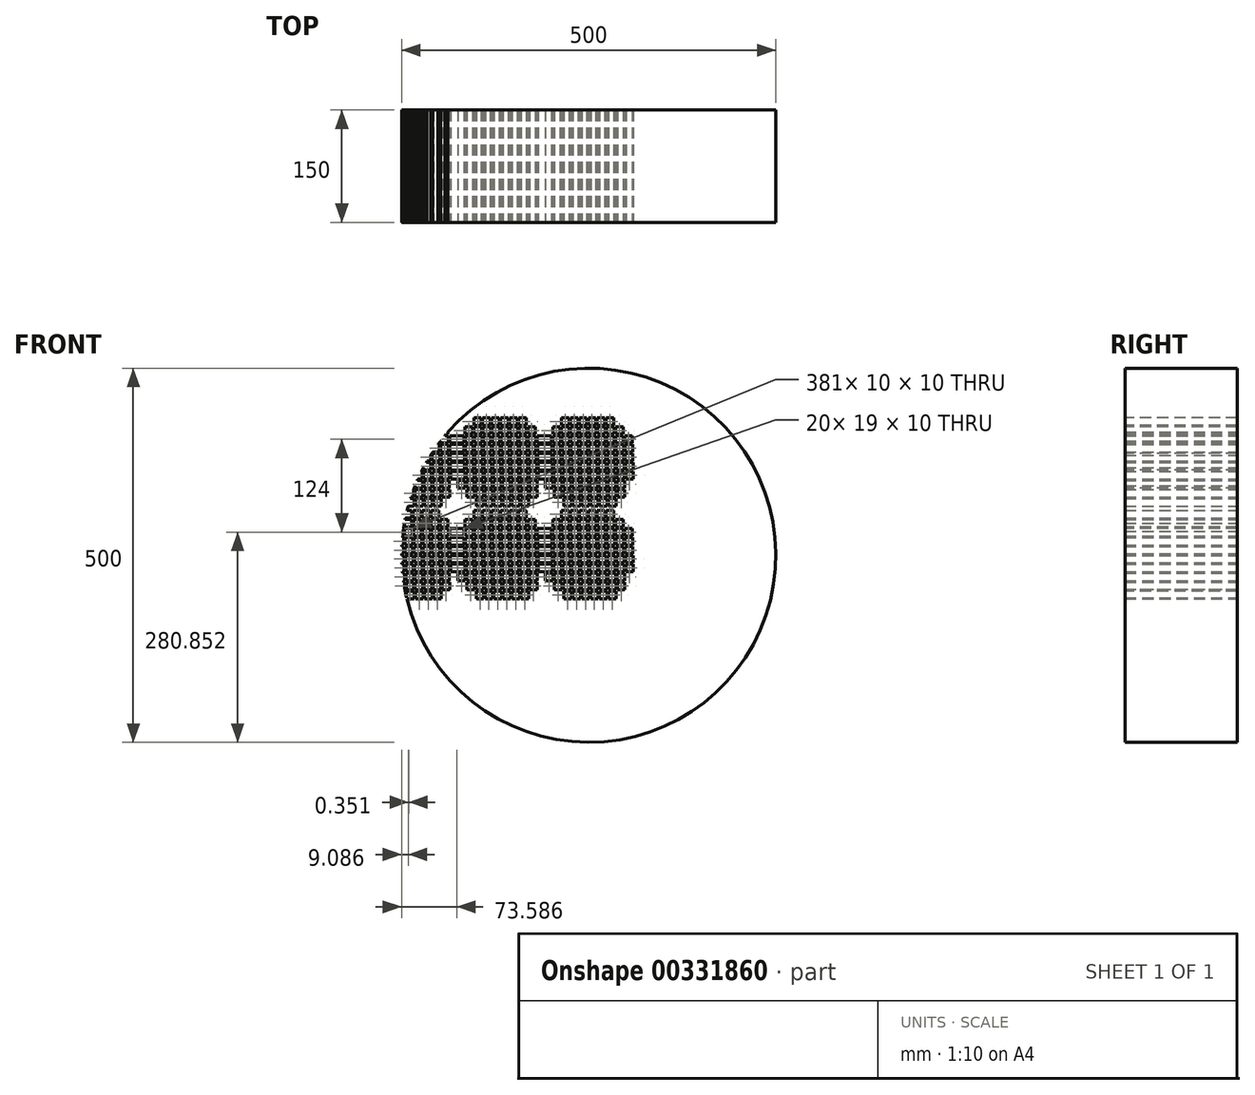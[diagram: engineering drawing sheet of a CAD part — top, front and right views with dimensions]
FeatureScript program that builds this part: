
annotation { "Feature Type Name" : "Feature", "Feature Type Description" : "" }
export const myFeature = defineFeature(function(context is Context, id is Id, definition is map)
    precondition{}
    {
        {
            var Q0;
            Q0=qCreatedBy(makeId("Front.planeOp"),FACE);
            var sketch = newSketch(context, id + "F0", { "sketchPlane" : qUnion([Q0])});
            skCircle(sketch, "E0", {"center": v(-42.34, 53.61) * mm, "radius": 250 * mm});
            skSolve(sketch);
        }
        {
            var Q0;
            Q0=makeQuery(id+"F0.imprint","IMPRINT",FACE,{"disambiguationData":[TD([[makeQuery(id+"F0.imprint","IMPRINT",EDGE,{"derivedFrom":sQuery(id+"F0.wireOp",EDGE,"E0")}),1.0]])]});
            extrude(context, id + "F1", {"entities" : qUnion([Q0]), "depth" : 150 * mm});
        }
        {
            var Q0;
            Q0=makeQuery(id+"F1.opExtrude","CAP_FACE",FACE,{"disambiguationData":[OSD([sQuery(id+"F0.wireOp",EDGE,"E0")])],"isStart":false});
            var sketch = newSketch(context, id + "F2", { "sketchPlane" : qUnion([Q0])});
            skLineSegment(sketch, "E1.0.2.0", {"start": v(-100.5, 19.49) * mm, "end": v(-90.5, 19.49) * mm});
            skLineSegment(sketch, "E1.0.2.1", {"start": v(-90.5, 19.49) * mm, "end": v(-90.5, 29.49) * mm});
            skLineSegment(sketch, "E1.0.2.2", {"start": v(-100.5, 29.49) * mm, "end": v(-90.5, 29.49) * mm});
            skLineSegment(sketch, "E1.0.2.3", {"start": v(-100.5, 19.49) * mm, "end": v(-100.5, 29.49) * mm});
            skLineSegment(sketch, "E1.0.3.0", {"start": v(-100.85, 31.48) * mm, "end": v(-90.85, 31.48) * mm});
            skLineSegment(sketch, "E1.0.3.1", {"start": v(-90.85, 31.48) * mm, "end": v(-90.85, 41.48) * mm});
            skLineSegment(sketch, "E1.0.3.2", {"start": v(-100.85, 41.48) * mm, "end": v(-90.85, 41.48) * mm});
            skLineSegment(sketch, "E1.0.3.3", {"start": v(-100.85, 31.48) * mm, "end": v(-100.85, 41.48) * mm});
            skLineSegment(sketch, "E1.0.4.0", {"start": v(-101.2, 43.48) * mm, "end": v(-91.2, 43.48) * mm});
            skLineSegment(sketch, "E1.0.4.1", {"start": v(-91.2, 43.48) * mm, "end": v(-91.2, 53.48) * mm});
            skLineSegment(sketch, "E1.0.4.2", {"start": v(-101.2, 53.48) * mm, "end": v(-91.2, 53.48) * mm});
            skLineSegment(sketch, "E1.0.4.3", {"start": v(-101.2, 43.48) * mm, "end": v(-101.2, 53.48) * mm});
            skLineSegment(sketch, "E1.0.5.0", {"start": v(-101.55, 55.47) * mm, "end": v(-91.55, 55.47) * mm});
            skLineSegment(sketch, "E1.0.5.1", {"start": v(-91.55, 55.47) * mm, "end": v(-91.55, 65.47) * mm});
            skLineSegment(sketch, "E1.0.5.2", {"start": v(-101.55, 65.47) * mm, "end": v(-91.55, 65.47) * mm});
            skLineSegment(sketch, "E1.0.5.3", {"start": v(-101.55, 55.47) * mm, "end": v(-101.55, 65.47) * mm});
            skLineSegment(sketch, "E1.0.6.0", {"start": v(-101.9, 67.47) * mm, "end": v(-91.9, 67.47) * mm});
            skLineSegment(sketch, "E1.0.6.1", {"start": v(-91.9, 67.47) * mm, "end": v(-91.9, 77.47) * mm});
            skLineSegment(sketch, "E1.0.6.2", {"start": v(-101.9, 77.47) * mm, "end": v(-91.9, 77.47) * mm});
            skLineSegment(sketch, "E1.0.6.3", {"start": v(-101.9, 67.47) * mm, "end": v(-101.9, 77.47) * mm});
            skLineSegment(sketch, "E1.0.7.0", {"start": v(-102.25, 79.46) * mm, "end": v(-92.25, 79.46) * mm});
            skLineSegment(sketch, "E1.0.7.1", {"start": v(-92.25, 79.46) * mm, "end": v(-92.25, 89.46) * mm});
            skLineSegment(sketch, "E1.0.7.2", {"start": v(-102.25, 89.46) * mm, "end": v(-92.25, 89.46) * mm});
            skLineSegment(sketch, "E1.0.7.3", {"start": v(-102.25, 79.46) * mm, "end": v(-102.25, 89.46) * mm});
            skLineSegment(sketch, "E1.1.1.0", {"start": v(-88.15, 7.5) * mm, "end": v(-78.15, 7.5) * mm});
            skLineSegment(sketch, "E1.1.1.1", {"start": v(-78.15, 7.5) * mm, "end": v(-78.15, 17.5) * mm});
            skLineSegment(sketch, "E1.1.1.2", {"start": v(-88.15, 17.5) * mm, "end": v(-78.15, 17.5) * mm});
            skLineSegment(sketch, "E1.1.1.3", {"start": v(-88.15, 7.5) * mm, "end": v(-88.15, 17.5) * mm});
            skLineSegment(sketch, "E1.1.2.0", {"start": v(-88.5, 19.49) * mm, "end": v(-78.5, 19.49) * mm});
            skLineSegment(sketch, "E1.1.2.1", {"start": v(-78.5, 19.49) * mm, "end": v(-78.5, 29.49) * mm});
            skLineSegment(sketch, "E1.1.2.2", {"start": v(-88.5, 29.49) * mm, "end": v(-78.5, 29.49) * mm});
            skLineSegment(sketch, "E1.1.2.3", {"start": v(-88.5, 19.49) * mm, "end": v(-88.5, 29.49) * mm});
            skLineSegment(sketch, "E1.1.3.0", {"start": v(-88.85, 31.48) * mm, "end": v(-78.85, 31.48) * mm});
            skLineSegment(sketch, "E1.1.3.1", {"start": v(-78.85, 31.48) * mm, "end": v(-78.85, 41.48) * mm});
            skLineSegment(sketch, "E1.1.3.2", {"start": v(-88.85, 41.48) * mm, "end": v(-78.85, 41.48) * mm});
            skLineSegment(sketch, "E1.1.3.3", {"start": v(-88.85, 31.48) * mm, "end": v(-88.85, 41.48) * mm});
            skLineSegment(sketch, "E1.1.4.0", {"start": v(-89.2, 43.48) * mm, "end": v(-79.2, 43.48) * mm});
            skLineSegment(sketch, "E1.1.4.1", {"start": v(-79.2, 43.48) * mm, "end": v(-79.2, 53.48) * mm});
            skLineSegment(sketch, "E1.1.4.2", {"start": v(-89.2, 53.48) * mm, "end": v(-79.2, 53.48) * mm});
            skLineSegment(sketch, "E1.1.4.3", {"start": v(-89.2, 43.48) * mm, "end": v(-89.2, 53.48) * mm});
            skLineSegment(sketch, "E1.1.5.0", {"start": v(-89.55, 55.47) * mm, "end": v(-79.55, 55.47) * mm});
            skLineSegment(sketch, "E1.1.5.1", {"start": v(-79.55, 55.47) * mm, "end": v(-79.55, 65.47) * mm});
            skLineSegment(sketch, "E1.1.5.2", {"start": v(-89.55, 65.47) * mm, "end": v(-79.55, 65.47) * mm});
            skLineSegment(sketch, "E1.1.5.3", {"start": v(-89.55, 55.47) * mm, "end": v(-89.55, 65.47) * mm});
            skLineSegment(sketch, "E1.1.6.0", {"start": v(-89.9, 67.47) * mm, "end": v(-79.9, 67.47) * mm});
            skLineSegment(sketch, "E1.1.6.1", {"start": v(-79.9, 67.47) * mm, "end": v(-79.9, 77.47) * mm});
            skLineSegment(sketch, "E1.1.6.2", {"start": v(-89.9, 77.47) * mm, "end": v(-79.9, 77.47) * mm});
            skLineSegment(sketch, "E1.1.6.3", {"start": v(-89.9, 67.47) * mm, "end": v(-89.9, 77.47) * mm});
            skLineSegment(sketch, "E1.1.7.0", {"start": v(-90.25, 79.46) * mm, "end": v(-80.25, 79.46) * mm});
            skLineSegment(sketch, "E1.1.7.1", {"start": v(-80.25, 79.46) * mm, "end": v(-80.25, 89.46) * mm});
            skLineSegment(sketch, "E1.1.7.2", {"start": v(-90.25, 89.46) * mm, "end": v(-80.25, 89.46) * mm});
            skLineSegment(sketch, "E1.1.7.3", {"start": v(-90.25, 79.46) * mm, "end": v(-90.25, 89.46) * mm});
            skLineSegment(sketch, "E1.1.8.0", {"start": v(-90.6, 91.46) * mm, "end": v(-80.6, 91.46) * mm});
            skLineSegment(sketch, "E1.1.8.1", {"start": v(-80.6, 91.46) * mm, "end": v(-80.6, 101.46) * mm});
            skLineSegment(sketch, "E1.1.8.2", {"start": v(-90.6, 101.46) * mm, "end": v(-80.6, 101.46) * mm});
            skLineSegment(sketch, "E1.1.8.3", {"start": v(-90.6, 91.46) * mm, "end": v(-90.6, 101.46) * mm});
            skLineSegment(sketch, "E1.2.0.0", {"start": v(-75.8, -4.5) * mm, "end": v(-65.8, -4.5) * mm});
            skLineSegment(sketch, "E1.2.0.1", {"start": v(-65.8, -4.5) * mm, "end": v(-65.8, 5.5) * mm});
            skLineSegment(sketch, "E1.2.0.2", {"start": v(-75.8, 5.5) * mm, "end": v(-65.8, 5.5) * mm});
            skLineSegment(sketch, "E1.2.0.3", {"start": v(-75.8, -4.5) * mm, "end": v(-75.8, 5.5) * mm});
            skLineSegment(sketch, "E1.2.1.0", {"start": v(-76.15, 7.5) * mm, "end": v(-66.15, 7.5) * mm});
            skLineSegment(sketch, "E1.2.1.1", {"start": v(-66.15, 7.5) * mm, "end": v(-66.15, 17.5) * mm});
            skLineSegment(sketch, "E1.2.1.2", {"start": v(-76.15, 17.5) * mm, "end": v(-66.15, 17.5) * mm});
            skLineSegment(sketch, "E1.2.1.3", {"start": v(-76.15, 7.5) * mm, "end": v(-76.15, 17.5) * mm});
            skLineSegment(sketch, "E1.2.2.0", {"start": v(-76.5, 19.49) * mm, "end": v(-66.5, 19.49) * mm});
            skLineSegment(sketch, "E1.2.2.1", {"start": v(-66.5, 19.49) * mm, "end": v(-66.5, 29.49) * mm});
            skLineSegment(sketch, "E1.2.2.2", {"start": v(-76.5, 29.49) * mm, "end": v(-66.5, 29.49) * mm});
            skLineSegment(sketch, "E1.2.2.3", {"start": v(-76.5, 19.49) * mm, "end": v(-76.5, 29.49) * mm});
            skLineSegment(sketch, "E1.2.3.0", {"start": v(-76.85, 31.48) * mm, "end": v(-66.85, 31.48) * mm});
            skLineSegment(sketch, "E1.2.3.1", {"start": v(-66.85, 31.48) * mm, "end": v(-66.85, 41.48) * mm});
            skLineSegment(sketch, "E1.2.3.2", {"start": v(-76.85, 41.48) * mm, "end": v(-66.85, 41.48) * mm});
            skLineSegment(sketch, "E1.2.3.3", {"start": v(-76.85, 31.48) * mm, "end": v(-76.85, 41.48) * mm});
            skLineSegment(sketch, "E1.2.4.0", {"start": v(-77.2, 43.48) * mm, "end": v(-67.2, 43.48) * mm});
            skLineSegment(sketch, "E1.2.4.1", {"start": v(-67.2, 43.48) * mm, "end": v(-67.2, 53.48) * mm});
            skLineSegment(sketch, "E1.2.4.2", {"start": v(-77.2, 53.48) * mm, "end": v(-67.2, 53.48) * mm});
            skLineSegment(sketch, "E1.2.4.3", {"start": v(-77.2, 43.48) * mm, "end": v(-77.2, 53.48) * mm});
            skLineSegment(sketch, "E1.2.5.0", {"start": v(-77.55, 55.47) * mm, "end": v(-67.55, 55.47) * mm});
            skLineSegment(sketch, "E1.2.5.1", {"start": v(-67.55, 55.47) * mm, "end": v(-67.55, 65.47) * mm});
            skLineSegment(sketch, "E1.2.5.2", {"start": v(-77.55, 65.47) * mm, "end": v(-67.55, 65.47) * mm});
            skLineSegment(sketch, "E1.2.5.3", {"start": v(-77.55, 55.47) * mm, "end": v(-77.55, 65.47) * mm});
            skLineSegment(sketch, "E1.2.6.0", {"start": v(-77.9, 67.47) * mm, "end": v(-67.9, 67.47) * mm});
            skLineSegment(sketch, "E1.2.6.1", {"start": v(-67.9, 67.47) * mm, "end": v(-67.9, 77.47) * mm});
            skLineSegment(sketch, "E1.2.6.2", {"start": v(-77.9, 77.47) * mm, "end": v(-67.9, 77.47) * mm});
            skLineSegment(sketch, "E1.2.6.3", {"start": v(-77.9, 67.47) * mm, "end": v(-77.9, 77.47) * mm});
            skLineSegment(sketch, "E1.2.7.0", {"start": v(-78.25, 79.46) * mm, "end": v(-68.25, 79.46) * mm});
            skLineSegment(sketch, "E1.2.7.1", {"start": v(-68.25, 79.46) * mm, "end": v(-68.25, 89.46) * mm});
            skLineSegment(sketch, "E1.2.7.2", {"start": v(-78.25, 89.46) * mm, "end": v(-68.25, 89.46) * mm});
            skLineSegment(sketch, "E1.2.7.3", {"start": v(-78.25, 79.46) * mm, "end": v(-78.25, 89.46) * mm});
            skLineSegment(sketch, "E1.2.8.0", {"start": v(-78.6, 91.46) * mm, "end": v(-68.6, 91.46) * mm});
            skLineSegment(sketch, "E1.2.8.1", {"start": v(-68.6, 91.46) * mm, "end": v(-68.6, 101.46) * mm});
            skLineSegment(sketch, "E1.2.8.2", {"start": v(-78.6, 101.46) * mm, "end": v(-68.6, 101.46) * mm});
            skLineSegment(sketch, "E1.2.8.3", {"start": v(-78.6, 91.46) * mm, "end": v(-78.6, 101.46) * mm});
            skLineSegment(sketch, "E1.2.9.0", {"start": v(-78.96, 103.45) * mm, "end": v(-68.96, 103.45) * mm});
            skLineSegment(sketch, "E1.2.9.1", {"start": v(-68.96, 103.45) * mm, "end": v(-68.96, 113.45) * mm});
            skLineSegment(sketch, "E1.2.9.2", {"start": v(-78.96, 113.45) * mm, "end": v(-68.96, 113.45) * mm});
            skLineSegment(sketch, "E1.2.9.3", {"start": v(-78.96, 103.45) * mm, "end": v(-78.96, 113.45) * mm});
            skLineSegment(sketch, "E1.3.0.0", {"start": v(-63.8, -4.5) * mm, "end": v(-53.8, -4.5) * mm});
            skLineSegment(sketch, "E1.3.0.1", {"start": v(-53.8, -4.5) * mm, "end": v(-53.8, 5.5) * mm});
            skLineSegment(sketch, "E1.3.0.2", {"start": v(-63.8, 5.5) * mm, "end": v(-53.8, 5.5) * mm});
            skLineSegment(sketch, "E1.3.0.3", {"start": v(-63.8, -4.5) * mm, "end": v(-63.8, 5.5) * mm});
            skLineSegment(sketch, "E1.3.1.0", {"start": v(-64.15, 7.5) * mm, "end": v(-54.15, 7.5) * mm});
            skLineSegment(sketch, "E1.3.1.1", {"start": v(-54.15, 7.5) * mm, "end": v(-54.15, 17.5) * mm});
            skLineSegment(sketch, "E1.3.1.2", {"start": v(-64.15, 17.5) * mm, "end": v(-54.15, 17.5) * mm});
            skLineSegment(sketch, "E1.3.1.3", {"start": v(-64.15, 7.5) * mm, "end": v(-64.15, 17.5) * mm});
            skLineSegment(sketch, "E1.3.2.0", {"start": v(-64.5, 19.49) * mm, "end": v(-54.5, 19.49) * mm});
            skLineSegment(sketch, "E1.3.2.1", {"start": v(-54.5, 19.49) * mm, "end": v(-54.5, 29.49) * mm});
            skLineSegment(sketch, "E1.3.2.2", {"start": v(-64.5, 29.49) * mm, "end": v(-54.5, 29.49) * mm});
            skLineSegment(sketch, "E1.3.2.3", {"start": v(-64.5, 19.49) * mm, "end": v(-64.5, 29.49) * mm});
            skLineSegment(sketch, "E1.3.3.0", {"start": v(-64.85, 31.48) * mm, "end": v(-54.85, 31.48) * mm});
            skLineSegment(sketch, "E1.3.3.1", {"start": v(-54.85, 31.48) * mm, "end": v(-54.85, 41.48) * mm});
            skLineSegment(sketch, "E1.3.3.2", {"start": v(-64.85, 41.48) * mm, "end": v(-54.85, 41.48) * mm});
            skLineSegment(sketch, "E1.3.3.3", {"start": v(-64.85, 31.48) * mm, "end": v(-64.85, 41.48) * mm});
            skLineSegment(sketch, "E1.3.4.0", {"start": v(-65.2, 43.48) * mm, "end": v(-55.2, 43.48) * mm});
            skLineSegment(sketch, "E1.3.4.1", {"start": v(-55.2, 43.48) * mm, "end": v(-55.2, 53.48) * mm});
            skLineSegment(sketch, "E1.3.4.2", {"start": v(-65.2, 53.48) * mm, "end": v(-55.2, 53.48) * mm});
            skLineSegment(sketch, "E1.3.4.3", {"start": v(-65.2, 43.48) * mm, "end": v(-65.2, 53.48) * mm});
            skLineSegment(sketch, "E1.3.5.0", {"start": v(-65.55, 55.47) * mm, "end": v(-55.55, 55.47) * mm});
            skLineSegment(sketch, "E1.3.5.1", {"start": v(-55.55, 55.47) * mm, "end": v(-55.55, 65.47) * mm});
            skLineSegment(sketch, "E1.3.5.2", {"start": v(-65.55, 65.47) * mm, "end": v(-55.55, 65.47) * mm});
            skLineSegment(sketch, "E1.3.5.3", {"start": v(-65.55, 55.47) * mm, "end": v(-65.55, 65.47) * mm});
            skLineSegment(sketch, "E1.3.6.0", {"start": v(-65.9, 67.47) * mm, "end": v(-55.9, 67.47) * mm});
            skLineSegment(sketch, "E1.3.6.1", {"start": v(-55.9, 67.47) * mm, "end": v(-55.9, 77.47) * mm});
            skLineSegment(sketch, "E1.3.6.2", {"start": v(-65.9, 77.47) * mm, "end": v(-55.9, 77.47) * mm});
            skLineSegment(sketch, "E1.3.6.3", {"start": v(-65.9, 67.47) * mm, "end": v(-65.9, 77.47) * mm});
            skLineSegment(sketch, "E1.3.7.0", {"start": v(-66.25, 79.46) * mm, "end": v(-56.25, 79.46) * mm});
            skLineSegment(sketch, "E1.3.7.1", {"start": v(-56.25, 79.46) * mm, "end": v(-56.25, 89.46) * mm});
            skLineSegment(sketch, "E1.3.7.2", {"start": v(-66.25, 89.46) * mm, "end": v(-56.25, 89.46) * mm});
            skLineSegment(sketch, "E1.3.7.3", {"start": v(-66.25, 79.46) * mm, "end": v(-66.25, 89.46) * mm});
            skLineSegment(sketch, "E1.3.8.0", {"start": v(-66.6, 91.46) * mm, "end": v(-56.6, 91.46) * mm});
            skLineSegment(sketch, "E1.3.8.1", {"start": v(-56.6, 91.46) * mm, "end": v(-56.6, 101.46) * mm});
            skLineSegment(sketch, "E1.3.8.2", {"start": v(-66.6, 101.46) * mm, "end": v(-56.6, 101.46) * mm});
            skLineSegment(sketch, "E1.3.8.3", {"start": v(-66.6, 91.46) * mm, "end": v(-66.6, 101.46) * mm});
            skLineSegment(sketch, "E1.3.9.0", {"start": v(-66.96, 103.45) * mm, "end": v(-56.96, 103.45) * mm});
            skLineSegment(sketch, "E1.3.9.1", {"start": v(-56.96, 103.45) * mm, "end": v(-56.96, 113.45) * mm});
            skLineSegment(sketch, "E1.3.9.2", {"start": v(-66.96, 113.45) * mm, "end": v(-56.96, 113.45) * mm});
            skLineSegment(sketch, "E1.3.9.3", {"start": v(-66.96, 103.45) * mm, "end": v(-66.96, 113.45) * mm});
            skLineSegment(sketch, "E1.4.0.0", {"start": v(-51.8, -4.5) * mm, "end": v(-41.8, -4.5) * mm});
            skLineSegment(sketch, "E1.4.0.1", {"start": v(-41.8, -4.5) * mm, "end": v(-41.8, 5.5) * mm});
            skLineSegment(sketch, "E1.4.0.2", {"start": v(-51.8, 5.5) * mm, "end": v(-41.8, 5.5) * mm});
            skLineSegment(sketch, "E1.4.0.3", {"start": v(-51.8, -4.5) * mm, "end": v(-51.8, 5.5) * mm});
            skLineSegment(sketch, "E1.4.1.0", {"start": v(-52.15, 7.5) * mm, "end": v(-42.15, 7.5) * mm});
            skLineSegment(sketch, "E1.4.1.1", {"start": v(-42.15, 7.5) * mm, "end": v(-42.15, 17.5) * mm});
            skLineSegment(sketch, "E1.4.1.2", {"start": v(-52.15, 17.5) * mm, "end": v(-42.15, 17.5) * mm});
            skLineSegment(sketch, "E1.4.1.3", {"start": v(-52.15, 7.5) * mm, "end": v(-52.15, 17.5) * mm});
            skLineSegment(sketch, "E1.4.2.0", {"start": v(-52.5, 19.49) * mm, "end": v(-42.5, 19.49) * mm});
            skLineSegment(sketch, "E1.4.2.1", {"start": v(-42.5, 19.49) * mm, "end": v(-42.5, 29.49) * mm});
            skLineSegment(sketch, "E1.4.2.2", {"start": v(-52.5, 29.49) * mm, "end": v(-42.5, 29.49) * mm});
            skLineSegment(sketch, "E1.4.2.3", {"start": v(-52.5, 19.49) * mm, "end": v(-52.5, 29.49) * mm});
            skLineSegment(sketch, "E1.4.3.0", {"start": v(-52.85, 31.48) * mm, "end": v(-42.85, 31.48) * mm});
            skLineSegment(sketch, "E1.4.3.1", {"start": v(-42.85, 31.48) * mm, "end": v(-42.85, 41.48) * mm});
            skLineSegment(sketch, "E1.4.3.2", {"start": v(-52.85, 41.48) * mm, "end": v(-42.85, 41.48) * mm});
            skLineSegment(sketch, "E1.4.3.3", {"start": v(-52.85, 31.48) * mm, "end": v(-52.85, 41.48) * mm});
            skLineSegment(sketch, "E1.4.4.0", {"start": v(-53.2, 43.48) * mm, "end": v(-43.2, 43.48) * mm});
            skLineSegment(sketch, "E1.4.4.1", {"start": v(-43.2, 43.48) * mm, "end": v(-43.2, 53.48) * mm});
            skLineSegment(sketch, "E1.4.4.2", {"start": v(-53.2, 53.48) * mm, "end": v(-43.2, 53.48) * mm});
            skLineSegment(sketch, "E1.4.4.3", {"start": v(-53.2, 43.48) * mm, "end": v(-53.2, 53.48) * mm});
            skLineSegment(sketch, "E1.4.5.0", {"start": v(-53.55, 55.47) * mm, "end": v(-43.55, 55.47) * mm});
            skLineSegment(sketch, "E1.4.5.1", {"start": v(-43.55, 55.47) * mm, "end": v(-43.55, 65.47) * mm});
            skLineSegment(sketch, "E1.4.5.2", {"start": v(-53.55, 65.47) * mm, "end": v(-43.55, 65.47) * mm});
            skLineSegment(sketch, "E1.4.5.3", {"start": v(-53.55, 55.47) * mm, "end": v(-53.55, 65.47) * mm});
            skLineSegment(sketch, "E1.4.6.0", {"start": v(-53.9, 67.47) * mm, "end": v(-43.9, 67.47) * mm});
            skLineSegment(sketch, "E1.4.6.1", {"start": v(-43.9, 67.47) * mm, "end": v(-43.9, 77.47) * mm});
            skLineSegment(sketch, "E1.4.6.2", {"start": v(-53.9, 77.47) * mm, "end": v(-43.9, 77.47) * mm});
            skLineSegment(sketch, "E1.4.6.3", {"start": v(-53.9, 67.47) * mm, "end": v(-53.9, 77.47) * mm});
            skLineSegment(sketch, "E1.4.7.0", {"start": v(-54.25, 79.46) * mm, "end": v(-44.25, 79.46) * mm});
            skLineSegment(sketch, "E1.4.7.1", {"start": v(-44.25, 79.46) * mm, "end": v(-44.25, 89.46) * mm});
            skLineSegment(sketch, "E1.4.7.2", {"start": v(-54.25, 89.46) * mm, "end": v(-44.25, 89.46) * mm});
            skLineSegment(sketch, "E1.4.7.3", {"start": v(-54.25, 79.46) * mm, "end": v(-54.25, 89.46) * mm});
            skLineSegment(sketch, "E1.4.8.0", {"start": v(-54.6, 91.46) * mm, "end": v(-44.6, 91.46) * mm});
            skLineSegment(sketch, "E1.4.8.1", {"start": v(-44.6, 91.46) * mm, "end": v(-44.6, 101.46) * mm});
            skLineSegment(sketch, "E1.4.8.2", {"start": v(-54.6, 101.46) * mm, "end": v(-44.6, 101.46) * mm});
            skLineSegment(sketch, "E1.4.8.3", {"start": v(-54.6, 91.46) * mm, "end": v(-54.6, 101.46) * mm});
            skLineSegment(sketch, "E1.4.9.0", {"start": v(-54.96, 103.45) * mm, "end": v(-44.96, 103.45) * mm});
            skLineSegment(sketch, "E1.4.9.1", {"start": v(-44.96, 103.45) * mm, "end": v(-44.96, 113.45) * mm});
            skLineSegment(sketch, "E1.4.9.2", {"start": v(-54.96, 113.45) * mm, "end": v(-44.96, 113.45) * mm});
            skLineSegment(sketch, "E1.4.9.3", {"start": v(-54.96, 103.45) * mm, "end": v(-54.96, 113.45) * mm});
            skLineSegment(sketch, "E1.5.0.0", {"start": v(-39.8, -4.5) * mm, "end": v(-29.8, -4.5) * mm});
            skLineSegment(sketch, "E1.5.0.1", {"start": v(-29.8, -4.5) * mm, "end": v(-29.8, 5.5) * mm});
            skLineSegment(sketch, "E1.5.0.2", {"start": v(-39.8, 5.5) * mm, "end": v(-29.8, 5.5) * mm});
            skLineSegment(sketch, "E1.5.0.3", {"start": v(-39.8, -4.5) * mm, "end": v(-39.8, 5.5) * mm});
            skLineSegment(sketch, "E1.5.1.0", {"start": v(-40.15, 7.5) * mm, "end": v(-30.15, 7.5) * mm});
            skLineSegment(sketch, "E1.5.1.1", {"start": v(-30.15, 7.5) * mm, "end": v(-30.15, 17.5) * mm});
            skLineSegment(sketch, "E1.5.1.2", {"start": v(-40.15, 17.5) * mm, "end": v(-30.15, 17.5) * mm});
            skLineSegment(sketch, "E1.5.1.3", {"start": v(-40.15, 7.5) * mm, "end": v(-40.15, 17.5) * mm});
            skLineSegment(sketch, "E1.5.2.0", {"start": v(-40.5, 19.49) * mm, "end": v(-30.5, 19.49) * mm});
            skLineSegment(sketch, "E1.5.2.1", {"start": v(-30.5, 19.49) * mm, "end": v(-30.5, 29.49) * mm});
            skLineSegment(sketch, "E1.5.2.2", {"start": v(-40.5, 29.49) * mm, "end": v(-30.5, 29.49) * mm});
            skLineSegment(sketch, "E1.5.2.3", {"start": v(-40.5, 19.49) * mm, "end": v(-40.5, 29.49) * mm});
            skLineSegment(sketch, "E1.5.3.0", {"start": v(-40.85, 31.48) * mm, "end": v(-30.85, 31.48) * mm});
            skLineSegment(sketch, "E1.5.3.1", {"start": v(-30.85, 31.48) * mm, "end": v(-30.85, 41.48) * mm});
            skLineSegment(sketch, "E1.5.3.2", {"start": v(-40.85, 41.48) * mm, "end": v(-30.85, 41.48) * mm});
            skLineSegment(sketch, "E1.5.3.3", {"start": v(-40.85, 31.48) * mm, "end": v(-40.85, 41.48) * mm});
            skLineSegment(sketch, "E1.5.4.0", {"start": v(-41.2, 43.48) * mm, "end": v(-31.2, 43.48) * mm});
            skLineSegment(sketch, "E1.5.4.1", {"start": v(-31.2, 43.48) * mm, "end": v(-31.2, 53.48) * mm});
            skLineSegment(sketch, "E1.5.4.2", {"start": v(-41.2, 53.48) * mm, "end": v(-31.2, 53.48) * mm});
            skLineSegment(sketch, "E1.5.4.3", {"start": v(-41.2, 43.48) * mm, "end": v(-41.2, 53.48) * mm});
            skLineSegment(sketch, "E1.5.5.0", {"start": v(-41.55, 55.47) * mm, "end": v(-31.55, 55.47) * mm});
            skLineSegment(sketch, "E1.5.5.1", {"start": v(-31.55, 55.47) * mm, "end": v(-31.55, 65.47) * mm});
            skLineSegment(sketch, "E1.5.5.2", {"start": v(-41.55, 65.47) * mm, "end": v(-31.55, 65.47) * mm});
            skLineSegment(sketch, "E1.5.5.3", {"start": v(-41.55, 55.47) * mm, "end": v(-41.55, 65.47) * mm});
            skLineSegment(sketch, "E1.5.6.0", {"start": v(-41.9, 67.47) * mm, "end": v(-31.9, 67.47) * mm});
            skLineSegment(sketch, "E1.5.6.1", {"start": v(-31.9, 67.47) * mm, "end": v(-31.9, 77.47) * mm});
            skLineSegment(sketch, "E1.5.6.2", {"start": v(-41.9, 77.47) * mm, "end": v(-31.9, 77.47) * mm});
            skLineSegment(sketch, "E1.5.6.3", {"start": v(-41.9, 67.47) * mm, "end": v(-41.9, 77.47) * mm});
            skLineSegment(sketch, "E1.5.7.0", {"start": v(-42.25, 79.46) * mm, "end": v(-32.25, 79.46) * mm});
            skLineSegment(sketch, "E1.5.7.1", {"start": v(-32.25, 79.46) * mm, "end": v(-32.25, 89.46) * mm});
            skLineSegment(sketch, "E1.5.7.2", {"start": v(-42.25, 89.46) * mm, "end": v(-32.25, 89.46) * mm});
            skLineSegment(sketch, "E1.5.7.3", {"start": v(-42.25, 79.46) * mm, "end": v(-42.25, 89.46) * mm});
            skLineSegment(sketch, "E1.5.8.0", {"start": v(-42.6, 91.46) * mm, "end": v(-32.6, 91.46) * mm});
            skLineSegment(sketch, "E1.5.8.1", {"start": v(-32.6, 91.46) * mm, "end": v(-32.6, 101.46) * mm});
            skLineSegment(sketch, "E1.5.8.2", {"start": v(-42.6, 101.46) * mm, "end": v(-32.6, 101.46) * mm});
            skLineSegment(sketch, "E1.5.8.3", {"start": v(-42.6, 91.46) * mm, "end": v(-42.6, 101.46) * mm});
            skLineSegment(sketch, "E1.5.9.0", {"start": v(-42.96, 103.45) * mm, "end": v(-32.96, 103.45) * mm});
            skLineSegment(sketch, "E1.5.9.1", {"start": v(-32.96, 103.45) * mm, "end": v(-32.96, 113.45) * mm});
            skLineSegment(sketch, "E1.5.9.2", {"start": v(-42.96, 113.45) * mm, "end": v(-32.96, 113.45) * mm});
            skLineSegment(sketch, "E1.5.9.3", {"start": v(-42.96, 103.45) * mm, "end": v(-42.96, 113.45) * mm});
            skLineSegment(sketch, "E1.6.0.0", {"start": v(-27.8, -4.5) * mm, "end": v(-17.8, -4.5) * mm});
            skLineSegment(sketch, "E1.6.0.1", {"start": v(-17.8, -4.5) * mm, "end": v(-17.8, 5.5) * mm});
            skLineSegment(sketch, "E1.6.0.2", {"start": v(-27.8, 5.5) * mm, "end": v(-17.8, 5.5) * mm});
            skLineSegment(sketch, "E1.6.0.3", {"start": v(-27.8, -4.5) * mm, "end": v(-27.8, 5.5) * mm});
            skLineSegment(sketch, "E1.6.1.0", {"start": v(-28.15, 7.5) * mm, "end": v(-18.15, 7.5) * mm});
            skLineSegment(sketch, "E1.6.1.1", {"start": v(-18.15, 7.5) * mm, "end": v(-18.15, 17.5) * mm});
            skLineSegment(sketch, "E1.6.1.2", {"start": v(-28.15, 17.5) * mm, "end": v(-18.15, 17.5) * mm});
            skLineSegment(sketch, "E1.6.1.3", {"start": v(-28.15, 7.5) * mm, "end": v(-28.15, 17.5) * mm});
            skLineSegment(sketch, "E1.6.2.0", {"start": v(-28.5, 19.49) * mm, "end": v(-18.5, 19.49) * mm});
            skLineSegment(sketch, "E1.6.2.1", {"start": v(-18.5, 19.49) * mm, "end": v(-18.5, 29.49) * mm});
            skLineSegment(sketch, "E1.6.2.2", {"start": v(-28.5, 29.49) * mm, "end": v(-18.5, 29.49) * mm});
            skLineSegment(sketch, "E1.6.2.3", {"start": v(-28.5, 19.49) * mm, "end": v(-28.5, 29.49) * mm});
            skLineSegment(sketch, "E1.6.3.0", {"start": v(-28.85, 31.48) * mm, "end": v(-18.85, 31.48) * mm});
            skLineSegment(sketch, "E1.6.3.1", {"start": v(-18.85, 31.48) * mm, "end": v(-18.85, 41.48) * mm});
            skLineSegment(sketch, "E1.6.3.2", {"start": v(-28.85, 41.48) * mm, "end": v(-18.85, 41.48) * mm});
            skLineSegment(sketch, "E1.6.3.3", {"start": v(-28.85, 31.48) * mm, "end": v(-28.85, 41.48) * mm});
            skLineSegment(sketch, "E1.6.4.0", {"start": v(-29.2, 43.48) * mm, "end": v(-19.2, 43.48) * mm});
            skLineSegment(sketch, "E1.6.4.1", {"start": v(-19.2, 43.48) * mm, "end": v(-19.2, 53.48) * mm});
            skLineSegment(sketch, "E1.6.4.2", {"start": v(-29.2, 53.48) * mm, "end": v(-19.2, 53.48) * mm});
            skLineSegment(sketch, "E1.6.4.3", {"start": v(-29.2, 43.48) * mm, "end": v(-29.2, 53.48) * mm});
            skLineSegment(sketch, "E1.6.5.0", {"start": v(-29.55, 55.47) * mm, "end": v(-19.55, 55.47) * mm});
            skLineSegment(sketch, "E1.6.5.1", {"start": v(-19.55, 55.47) * mm, "end": v(-19.55, 65.47) * mm});
            skLineSegment(sketch, "E1.6.5.2", {"start": v(-29.55, 65.47) * mm, "end": v(-19.55, 65.47) * mm});
            skLineSegment(sketch, "E1.6.5.3", {"start": v(-29.55, 55.47) * mm, "end": v(-29.55, 65.47) * mm});
            skLineSegment(sketch, "E1.6.6.0", {"start": v(-29.9, 67.47) * mm, "end": v(-19.9, 67.47) * mm});
            skLineSegment(sketch, "E1.6.6.1", {"start": v(-19.9, 67.47) * mm, "end": v(-19.9, 77.47) * mm});
            skLineSegment(sketch, "E1.6.6.2", {"start": v(-29.9, 77.47) * mm, "end": v(-19.9, 77.47) * mm});
            skLineSegment(sketch, "E1.6.6.3", {"start": v(-29.9, 67.47) * mm, "end": v(-29.9, 77.47) * mm});
            skLineSegment(sketch, "E1.6.7.0", {"start": v(-30.25, 79.46) * mm, "end": v(-20.25, 79.46) * mm});
            skLineSegment(sketch, "E1.6.7.1", {"start": v(-20.25, 79.46) * mm, "end": v(-20.25, 89.46) * mm});
            skLineSegment(sketch, "E1.6.7.2", {"start": v(-30.25, 89.46) * mm, "end": v(-20.25, 89.46) * mm});
            skLineSegment(sketch, "E1.6.7.3", {"start": v(-30.25, 79.46) * mm, "end": v(-30.25, 89.46) * mm});
            skLineSegment(sketch, "E1.6.8.0", {"start": v(-30.6, 91.46) * mm, "end": v(-20.6, 91.46) * mm});
            skLineSegment(sketch, "E1.6.8.1", {"start": v(-20.6, 91.46) * mm, "end": v(-20.6, 101.46) * mm});
            skLineSegment(sketch, "E1.6.8.2", {"start": v(-30.6, 101.46) * mm, "end": v(-20.6, 101.46) * mm});
            skLineSegment(sketch, "E1.6.8.3", {"start": v(-30.6, 91.46) * mm, "end": v(-30.6, 101.46) * mm});
            skLineSegment(sketch, "E1.6.9.0", {"start": v(-30.96, 103.45) * mm, "end": v(-20.96, 103.45) * mm});
            skLineSegment(sketch, "E1.6.9.1", {"start": v(-20.96, 103.45) * mm, "end": v(-20.96, 113.45) * mm});
            skLineSegment(sketch, "E1.6.9.2", {"start": v(-30.96, 113.45) * mm, "end": v(-20.96, 113.45) * mm});
            skLineSegment(sketch, "E1.6.9.3", {"start": v(-30.96, 103.45) * mm, "end": v(-30.96, 113.45) * mm});
            skLineSegment(sketch, "E1.7.0.0", {"start": v(-15.8, -4.5) * mm, "end": v(-5.8, -4.5) * mm});
            skLineSegment(sketch, "E1.7.0.1", {"start": v(-5.8, -4.5) * mm, "end": v(-5.8, 5.5) * mm});
            skLineSegment(sketch, "E1.7.0.2", {"start": v(-15.8, 5.5) * mm, "end": v(-5.8, 5.5) * mm});
            skLineSegment(sketch, "E1.7.0.3", {"start": v(-15.8, -4.5) * mm, "end": v(-15.8, 5.5) * mm});
            skLineSegment(sketch, "E1.7.1.0", {"start": v(-16.15, 7.5) * mm, "end": v(-6.15, 7.5) * mm});
            skLineSegment(sketch, "E1.7.1.1", {"start": v(-6.15, 7.5) * mm, "end": v(-6.15, 17.5) * mm});
            skLineSegment(sketch, "E1.7.1.2", {"start": v(-16.15, 17.5) * mm, "end": v(-6.15, 17.5) * mm});
            skLineSegment(sketch, "E1.7.1.3", {"start": v(-16.15, 7.5) * mm, "end": v(-16.15, 17.5) * mm});
            skLineSegment(sketch, "E1.7.2.0", {"start": v(-16.5, 19.49) * mm, "end": v(-6.5, 19.49) * mm});
            skLineSegment(sketch, "E1.7.2.1", {"start": v(-6.5, 19.49) * mm, "end": v(-6.5, 29.49) * mm});
            skLineSegment(sketch, "E1.7.2.2", {"start": v(-16.5, 29.49) * mm, "end": v(-6.5, 29.49) * mm});
            skLineSegment(sketch, "E1.7.2.3", {"start": v(-16.5, 19.49) * mm, "end": v(-16.5, 29.49) * mm});
            skLineSegment(sketch, "E1.7.3.0", {"start": v(-16.85, 31.48) * mm, "end": v(-6.85, 31.48) * mm});
            skLineSegment(sketch, "E1.7.3.1", {"start": v(-6.85, 31.48) * mm, "end": v(-6.85, 41.48) * mm});
            skLineSegment(sketch, "E1.7.3.2", {"start": v(-16.85, 41.48) * mm, "end": v(-6.85, 41.48) * mm});
            skLineSegment(sketch, "E1.7.3.3", {"start": v(-16.85, 31.48) * mm, "end": v(-16.85, 41.48) * mm});
            skLineSegment(sketch, "E1.7.4.0", {"start": v(-17.2, 43.48) * mm, "end": v(-7.2, 43.48) * mm});
            skLineSegment(sketch, "E1.7.4.1", {"start": v(-7.2, 43.48) * mm, "end": v(-7.2, 53.48) * mm});
            skLineSegment(sketch, "E1.7.4.2", {"start": v(-17.2, 53.48) * mm, "end": v(-7.2, 53.48) * mm});
            skLineSegment(sketch, "E1.7.4.3", {"start": v(-17.2, 43.48) * mm, "end": v(-17.2, 53.48) * mm});
            skLineSegment(sketch, "E1.7.5.0", {"start": v(-17.55, 55.47) * mm, "end": v(-7.55, 55.47) * mm});
            skLineSegment(sketch, "E1.7.5.1", {"start": v(-7.55, 55.47) * mm, "end": v(-7.55, 65.47) * mm});
            skLineSegment(sketch, "E1.7.5.2", {"start": v(-17.55, 65.47) * mm, "end": v(-7.55, 65.47) * mm});
            skLineSegment(sketch, "E1.7.5.3", {"start": v(-17.55, 55.47) * mm, "end": v(-17.55, 65.47) * mm});
            skLineSegment(sketch, "E1.7.6.0", {"start": v(-17.9, 67.47) * mm, "end": v(-7.9, 67.47) * mm});
            skLineSegment(sketch, "E1.7.6.1", {"start": v(-7.9, 67.47) * mm, "end": v(-7.9, 77.47) * mm});
            skLineSegment(sketch, "E1.7.6.2", {"start": v(-17.9, 77.47) * mm, "end": v(-7.9, 77.47) * mm});
            skLineSegment(sketch, "E1.7.6.3", {"start": v(-17.9, 67.47) * mm, "end": v(-17.9, 77.47) * mm});
            skLineSegment(sketch, "E1.7.7.0", {"start": v(-18.25, 79.46) * mm, "end": v(-8.25, 79.46) * mm});
            skLineSegment(sketch, "E1.7.7.1", {"start": v(-8.25, 79.46) * mm, "end": v(-8.25, 89.46) * mm});
            skLineSegment(sketch, "E1.7.7.2", {"start": v(-18.25, 89.46) * mm, "end": v(-8.25, 89.46) * mm});
            skLineSegment(sketch, "E1.7.7.3", {"start": v(-18.25, 79.46) * mm, "end": v(-18.25, 89.46) * mm});
            skLineSegment(sketch, "E1.7.8.0", {"start": v(-18.6, 91.46) * mm, "end": v(-8.6, 91.46) * mm});
            skLineSegment(sketch, "E1.7.8.1", {"start": v(-8.6, 91.46) * mm, "end": v(-8.6, 101.46) * mm});
            skLineSegment(sketch, "E1.7.8.2", {"start": v(-18.6, 101.46) * mm, "end": v(-8.6, 101.46) * mm});
            skLineSegment(sketch, "E1.7.8.3", {"start": v(-18.6, 91.46) * mm, "end": v(-18.6, 101.46) * mm});
            skLineSegment(sketch, "E1.7.9.0", {"start": v(-18.96, 103.45) * mm, "end": v(-8.96, 103.45) * mm});
            skLineSegment(sketch, "E1.7.9.1", {"start": v(-8.96, 103.45) * mm, "end": v(-8.96, 113.45) * mm});
            skLineSegment(sketch, "E1.7.9.2", {"start": v(-18.96, 113.45) * mm, "end": v(-8.96, 113.45) * mm});
            skLineSegment(sketch, "E1.7.9.3", {"start": v(-18.96, 103.45) * mm, "end": v(-18.96, 113.45) * mm});
            skLineSegment(sketch, "E1.8.1.0", {"start": v(-4.15, 7.5) * mm, "end": v(5.85, 7.5) * mm});
            skLineSegment(sketch, "E1.8.1.1", {"start": v(5.85, 7.5) * mm, "end": v(5.85, 17.5) * mm});
            skLineSegment(sketch, "E1.8.1.2", {"start": v(-4.15, 17.5) * mm, "end": v(5.85, 17.5) * mm});
            skLineSegment(sketch, "E1.8.1.3", {"start": v(-4.15, 7.5) * mm, "end": v(-4.15, 17.5) * mm});
            skLineSegment(sketch, "E1.8.2.0", {"start": v(-4.5, 19.49) * mm, "end": v(5.5, 19.49) * mm});
            skLineSegment(sketch, "E1.8.2.1", {"start": v(5.5, 19.49) * mm, "end": v(5.5, 29.49) * mm});
            skLineSegment(sketch, "E1.8.2.2", {"start": v(-4.5, 29.49) * mm, "end": v(5.5, 29.49) * mm});
            skLineSegment(sketch, "E1.8.2.3", {"start": v(-4.5, 19.49) * mm, "end": v(-4.5, 29.49) * mm});
            skLineSegment(sketch, "E1.8.3.0", {"start": v(-4.85, 31.48) * mm, "end": v(5.15, 31.48) * mm});
            skLineSegment(sketch, "E1.8.3.1", {"start": v(5.15, 31.48) * mm, "end": v(5.15, 41.48) * mm});
            skLineSegment(sketch, "E1.8.3.2", {"start": v(-4.85, 41.48) * mm, "end": v(5.15, 41.48) * mm});
            skLineSegment(sketch, "E1.8.3.3", {"start": v(-4.85, 31.48) * mm, "end": v(-4.85, 41.48) * mm});
            skLineSegment(sketch, "E1.8.4.0", {"start": v(-5.2, 43.48) * mm, "end": v(4.8, 43.48) * mm});
            skLineSegment(sketch, "E1.8.4.1", {"start": v(4.8, 43.48) * mm, "end": v(4.8, 53.48) * mm});
            skLineSegment(sketch, "E1.8.4.2", {"start": v(-5.2, 53.48) * mm, "end": v(4.8, 53.48) * mm});
            skLineSegment(sketch, "E1.8.4.3", {"start": v(-5.2, 43.48) * mm, "end": v(-5.2, 53.48) * mm});
            skLineSegment(sketch, "E1.8.5.0", {"start": v(-5.55, 55.47) * mm, "end": v(4.45, 55.47) * mm});
            skLineSegment(sketch, "E1.8.5.1", {"start": v(4.45, 55.47) * mm, "end": v(4.45, 65.47) * mm});
            skLineSegment(sketch, "E1.8.5.2", {"start": v(-5.55, 65.47) * mm, "end": v(4.45, 65.47) * mm});
            skLineSegment(sketch, "E1.8.5.3", {"start": v(-5.55, 55.47) * mm, "end": v(-5.55, 65.47) * mm});
            skLineSegment(sketch, "E1.8.6.0", {"start": v(-5.9, 67.47) * mm, "end": v(4.1, 67.47) * mm});
            skLineSegment(sketch, "E1.8.6.1", {"start": v(4.1, 67.47) * mm, "end": v(4.1, 77.47) * mm});
            skLineSegment(sketch, "E1.8.6.2", {"start": v(-5.9, 77.47) * mm, "end": v(4.1, 77.47) * mm});
            skLineSegment(sketch, "E1.8.6.3", {"start": v(-5.9, 67.47) * mm, "end": v(-5.9, 77.47) * mm});
            skLineSegment(sketch, "E1.8.7.0", {"start": v(-6.25, 79.46) * mm, "end": v(3.75, 79.46) * mm});
            skLineSegment(sketch, "E1.8.7.1", {"start": v(3.75, 79.46) * mm, "end": v(3.75, 89.46) * mm});
            skLineSegment(sketch, "E1.8.7.2", {"start": v(-6.25, 89.46) * mm, "end": v(3.75, 89.46) * mm});
            skLineSegment(sketch, "E1.8.7.3", {"start": v(-6.25, 79.46) * mm, "end": v(-6.25, 89.46) * mm});
            skLineSegment(sketch, "E1.8.8.0", {"start": v(-6.6, 91.46) * mm, "end": v(3.4, 91.46) * mm});
            skLineSegment(sketch, "E1.8.8.1", {"start": v(3.4, 91.46) * mm, "end": v(3.4, 101.46) * mm});
            skLineSegment(sketch, "E1.8.8.2", {"start": v(-6.6, 101.46) * mm, "end": v(3.4, 101.46) * mm});
            skLineSegment(sketch, "E1.8.8.3", {"start": v(-6.6, 91.46) * mm, "end": v(-6.6, 101.46) * mm});
            skLineSegment(sketch, "E1.9.3.0", {"start": v(7.15, 31.48) * mm, "end": v(17.15, 31.48) * mm});
            skLineSegment(sketch, "E1.9.3.1", {"start": v(17.15, 31.48) * mm, "end": v(17.15, 41.48) * mm});
            skLineSegment(sketch, "E1.9.3.2", {"start": v(7.15, 41.48) * mm, "end": v(17.15, 41.48) * mm});
            skLineSegment(sketch, "E1.9.3.3", {"start": v(7.15, 31.48) * mm, "end": v(7.15, 41.48) * mm});
            skLineSegment(sketch, "E1.9.4.0", {"start": v(6.8, 43.48) * mm, "end": v(16.8, 43.48) * mm});
            skLineSegment(sketch, "E1.9.4.1", {"start": v(16.8, 43.48) * mm, "end": v(16.8, 53.48) * mm});
            skLineSegment(sketch, "E1.9.4.2", {"start": v(6.8, 53.48) * mm, "end": v(16.8, 53.48) * mm});
            skLineSegment(sketch, "E1.9.4.3", {"start": v(6.8, 43.48) * mm, "end": v(6.8, 53.48) * mm});
            skLineSegment(sketch, "E1.9.5.0", {"start": v(6.45, 55.47) * mm, "end": v(16.45, 55.47) * mm});
            skLineSegment(sketch, "E1.9.5.1", {"start": v(16.45, 55.47) * mm, "end": v(16.45, 65.47) * mm});
            skLineSegment(sketch, "E1.9.5.2", {"start": v(6.45, 65.47) * mm, "end": v(16.45, 65.47) * mm});
            skLineSegment(sketch, "E1.9.5.3", {"start": v(6.45, 55.47) * mm, "end": v(6.45, 65.47) * mm});
            skLineSegment(sketch, "E1.9.6.0", {"start": v(6.1, 67.47) * mm, "end": v(16.1, 67.47) * mm});
            skLineSegment(sketch, "E1.9.6.1", {"start": v(16.1, 67.47) * mm, "end": v(16.1, 77.47) * mm});
            skLineSegment(sketch, "E1.9.6.2", {"start": v(6.1, 77.47) * mm, "end": v(16.1, 77.47) * mm});
            skLineSegment(sketch, "E1.9.6.3", {"start": v(6.1, 67.47) * mm, "end": v(6.1, 77.47) * mm});
            skLineSegment(sketch, "E1.9.7.0", {"start": v(5.75, 79.46) * mm, "end": v(15.75, 79.46) * mm});
            skLineSegment(sketch, "E1.9.7.1", {"start": v(15.75, 79.46) * mm, "end": v(15.75, 89.46) * mm});
            skLineSegment(sketch, "E1.9.7.2", {"start": v(5.75, 89.46) * mm, "end": v(15.75, 89.46) * mm});
            skLineSegment(sketch, "E1.9.7.3", {"start": v(5.75, 79.46) * mm, "end": v(5.75, 89.46) * mm});
            skLineSegment(sketch, "E2.0.0.1", {"start": v(-101.55, 179.47) * mm, "end": v(-101.55, 189.47) * mm});
            skLineSegment(sketch, "E2.1.0.1", {"start": v(-91.55, 179.47) * mm, "end": v(-91.55, 189.47) * mm});
            skLineSegment(sketch, "E2.2.0.1", {"start": v(-101.55, 189.47) * mm, "end": v(-91.55, 189.47) * mm});
            skLineSegment(sketch, "E2.3.0.1", {"start": v(-100.5, 143.49) * mm, "end": v(-90.5, 143.49) * mm});
            skLineSegment(sketch, "E2.4.0.1", {"start": v(-90.5, 143.49) * mm, "end": v(-90.5, 153.49) * mm});
            skLineSegment(sketch, "E2.5.0.1", {"start": v(-100.5, 153.49) * mm, "end": v(-90.5, 153.49) * mm});
            skLineSegment(sketch, "E2.6.0.1", {"start": v(-100.5, 143.49) * mm, "end": v(-100.5, 153.49) * mm});
            skLineSegment(sketch, "E2.7.0.1", {"start": v(-100.85, 155.48) * mm, "end": v(-90.85, 155.48) * mm});
            skLineSegment(sketch, "E2.8.0.1", {"start": v(-90.85, 155.48) * mm, "end": v(-90.85, 165.48) * mm});
            skLineSegment(sketch, "E2.9.0.1", {"start": v(-100.85, 165.48) * mm, "end": v(-90.85, 165.48) * mm});
            skLineSegment(sketch, "E2.10.0.1", {"start": v(-100.85, 155.48) * mm, "end": v(-100.85, 165.48) * mm});
            skLineSegment(sketch, "E2.11.0.1", {"start": v(-101.2, 167.48) * mm, "end": v(-91.2, 167.48) * mm});
            skLineSegment(sketch, "E2.12.0.1", {"start": v(-91.2, 167.48) * mm, "end": v(-91.2, 177.48) * mm});
            skLineSegment(sketch, "E2.13.0.1", {"start": v(-101.2, 177.48) * mm, "end": v(-91.2, 177.48) * mm});
            skLineSegment(sketch, "E2.14.0.1", {"start": v(-101.2, 167.48) * mm, "end": v(-101.2, 177.48) * mm});
            skLineSegment(sketch, "E2.15.0.1", {"start": v(-101.55, 179.47) * mm, "end": v(-91.55, 179.47) * mm});
            skLineSegment(sketch, "E2.16.0.1", {"start": v(-88.5, 143.49) * mm, "end": v(-88.5, 153.49) * mm});
            skLineSegment(sketch, "E2.17.0.1", {"start": v(-89.9, 191.47) * mm, "end": v(-89.9, 201.47) * mm});
            skLineSegment(sketch, "E2.18.0.1", {"start": v(-76.15, 131.5) * mm, "end": v(-76.15, 141.5) * mm});
            skLineSegment(sketch, "E2.19.0.1", {"start": v(-77.55, 179.47) * mm, "end": v(-77.55, 189.47) * mm});
            skLineSegment(sketch, "E2.20.0.1", {"start": v(-78.96, 227.45) * mm, "end": v(-78.96, 237.45) * mm});
            skLineSegment(sketch, "E2.21.0.1", {"start": v(-64.85, 155.48) * mm, "end": v(-64.85, 165.48) * mm});
            skLineSegment(sketch, "E2.22.0.1", {"start": v(-66.25, 203.46) * mm, "end": v(-66.25, 213.46) * mm});
            skLineSegment(sketch, "E2.23.0.1", {"start": v(-52.15, 131.5) * mm, "end": v(-52.15, 141.5) * mm});
            skLineSegment(sketch, "E2.24.0.1", {"start": v(-53.55, 179.47) * mm, "end": v(-53.55, 189.47) * mm});
            skLineSegment(sketch, "E2.25.0.1", {"start": v(-54.96, 227.45) * mm, "end": v(-54.96, 237.45) * mm});
            skLineSegment(sketch, "E2.26.0.1", {"start": v(-40.85, 155.48) * mm, "end": v(-40.85, 165.48) * mm});
            skLineSegment(sketch, "E2.27.0.1", {"start": v(-42.25, 203.46) * mm, "end": v(-42.25, 213.46) * mm});
            skLineSegment(sketch, "E2.28.0.1", {"start": v(-28.15, 131.5) * mm, "end": v(-28.15, 141.5) * mm});
            skLineSegment(sketch, "E2.29.0.1", {"start": v(-29.55, 179.47) * mm, "end": v(-29.55, 189.47) * mm});
            skLineSegment(sketch, "E2.30.0.1", {"start": v(-30.96, 227.45) * mm, "end": v(-30.96, 237.45) * mm});
            skLineSegment(sketch, "E2.31.0.1", {"start": v(-16.85, 155.48) * mm, "end": v(-16.85, 165.48) * mm});
            skLineSegment(sketch, "E2.32.0.1", {"start": v(-18.25, 203.46) * mm, "end": v(-18.25, 213.46) * mm});
            skLineSegment(sketch, "E2.33.0.1", {"start": v(-4.5, 143.49) * mm, "end": v(-4.5, 153.49) * mm});
            skLineSegment(sketch, "E2.34.0.1", {"start": v(-5.9, 191.47) * mm, "end": v(-5.9, 201.47) * mm});
            skLineSegment(sketch, "E2.35.0.1", {"start": v(6.8, 167.48) * mm, "end": v(6.8, 177.48) * mm});
            skLineSegment(sketch, "E2.36.0.1", {"start": v(-78.5, 143.49) * mm, "end": v(-78.5, 153.49) * mm});
            skLineSegment(sketch, "E2.37.0.1", {"start": v(-79.9, 191.47) * mm, "end": v(-79.9, 201.47) * mm});
            skLineSegment(sketch, "E2.38.0.1", {"start": v(-66.15, 131.5) * mm, "end": v(-66.15, 141.5) * mm});
            skLineSegment(sketch, "E2.39.0.1", {"start": v(-67.55, 179.47) * mm, "end": v(-67.55, 189.47) * mm});
            skLineSegment(sketch, "E2.40.0.1", {"start": v(-68.96, 227.45) * mm, "end": v(-68.96, 237.45) * mm});
            skLineSegment(sketch, "E2.41.0.1", {"start": v(-54.85, 155.48) * mm, "end": v(-54.85, 165.48) * mm});
            skLineSegment(sketch, "E2.42.0.1", {"start": v(-56.25, 203.46) * mm, "end": v(-56.25, 213.46) * mm});
            skLineSegment(sketch, "E2.43.0.1", {"start": v(-42.15, 131.5) * mm, "end": v(-42.15, 141.5) * mm});
            skLineSegment(sketch, "E2.44.0.1", {"start": v(-43.55, 179.47) * mm, "end": v(-43.55, 189.47) * mm});
            skLineSegment(sketch, "E2.45.0.1", {"start": v(-44.96, 227.45) * mm, "end": v(-44.96, 237.45) * mm});
            skLineSegment(sketch, "E2.46.0.1", {"start": v(-30.85, 155.48) * mm, "end": v(-30.85, 165.48) * mm});
            skLineSegment(sketch, "E2.47.0.1", {"start": v(-32.25, 203.46) * mm, "end": v(-32.25, 213.46) * mm});
            skLineSegment(sketch, "E2.48.0.1", {"start": v(-18.15, 131.5) * mm, "end": v(-18.15, 141.5) * mm});
            skLineSegment(sketch, "E2.49.0.1", {"start": v(-19.55, 179.47) * mm, "end": v(-19.55, 189.47) * mm});
            skLineSegment(sketch, "E2.50.0.1", {"start": v(-20.96, 227.45) * mm, "end": v(-20.96, 237.45) * mm});
            skLineSegment(sketch, "E2.51.0.1", {"start": v(-6.85, 155.48) * mm, "end": v(-6.85, 165.48) * mm});
            skLineSegment(sketch, "E2.52.0.1", {"start": v(-8.25, 203.46) * mm, "end": v(-8.25, 213.46) * mm});
            skLineSegment(sketch, "E2.53.0.1", {"start": v(5.5, 143.49) * mm, "end": v(5.5, 153.49) * mm});
            skLineSegment(sketch, "E2.54.0.1", {"start": v(4.1, 191.47) * mm, "end": v(4.1, 201.47) * mm});
            skLineSegment(sketch, "E2.55.0.1", {"start": v(16.8, 167.48) * mm, "end": v(16.8, 177.48) * mm});
            skLineSegment(sketch, "E2.56.0.1", {"start": v(-88.5, 153.49) * mm, "end": v(-78.5, 153.49) * mm});
            skLineSegment(sketch, "E2.57.0.1", {"start": v(-89.9, 201.47) * mm, "end": v(-79.9, 201.47) * mm});
            skLineSegment(sketch, "E2.58.0.1", {"start": v(-76.15, 141.5) * mm, "end": v(-66.15, 141.5) * mm});
            skLineSegment(sketch, "E2.59.0.1", {"start": v(-77.55, 189.47) * mm, "end": v(-67.55, 189.47) * mm});
            skLineSegment(sketch, "E2.60.0.1", {"start": v(-78.96, 237.45) * mm, "end": v(-68.96, 237.45) * mm});
            skLineSegment(sketch, "E2.61.0.1", {"start": v(-64.85, 165.48) * mm, "end": v(-54.85, 165.48) * mm});
            skLineSegment(sketch, "E2.62.0.1", {"start": v(-66.25, 213.46) * mm, "end": v(-56.25, 213.46) * mm});
            skLineSegment(sketch, "E2.63.0.1", {"start": v(-52.15, 141.5) * mm, "end": v(-42.15, 141.5) * mm});
            skLineSegment(sketch, "E2.64.0.1", {"start": v(-53.55, 189.47) * mm, "end": v(-43.55, 189.47) * mm});
            skLineSegment(sketch, "E2.65.0.1", {"start": v(-54.96, 237.45) * mm, "end": v(-44.96, 237.45) * mm});
            skLineSegment(sketch, "E2.66.0.1", {"start": v(-40.85, 165.48) * mm, "end": v(-30.85, 165.48) * mm});
            skLineSegment(sketch, "E2.67.0.1", {"start": v(-42.25, 213.46) * mm, "end": v(-32.25, 213.46) * mm});
            skLineSegment(sketch, "E2.68.0.1", {"start": v(-28.15, 141.5) * mm, "end": v(-18.15, 141.5) * mm});
            skLineSegment(sketch, "E2.69.0.1", {"start": v(-29.55, 189.47) * mm, "end": v(-19.55, 189.47) * mm});
            skLineSegment(sketch, "E2.70.0.1", {"start": v(-30.96, 237.45) * mm, "end": v(-20.96, 237.45) * mm});
            skLineSegment(sketch, "E2.71.0.1", {"start": v(-18.25, 213.46) * mm, "end": v(-8.25, 213.46) * mm});
            skLineSegment(sketch, "E2.72.0.1", {"start": v(-4.5, 153.49) * mm, "end": v(5.5, 153.49) * mm});
            skLineSegment(sketch, "E2.73.0.1", {"start": v(-5.9, 201.47) * mm, "end": v(4.1, 201.47) * mm});
            skLineSegment(sketch, "E2.74.0.1", {"start": v(6.8, 177.48) * mm, "end": v(16.8, 177.48) * mm});
            skLineSegment(sketch, "E2.75.0.1", {"start": v(-101.9, 191.47) * mm, "end": v(-91.9, 191.47) * mm});
            skLineSegment(sketch, "E2.76.0.1", {"start": v(-88.85, 155.48) * mm, "end": v(-78.85, 155.48) * mm});
            skLineSegment(sketch, "E2.77.0.1", {"start": v(-90.25, 203.46) * mm, "end": v(-80.25, 203.46) * mm});
            skLineSegment(sketch, "E2.78.0.1", {"start": v(-76.5, 143.49) * mm, "end": v(-66.5, 143.49) * mm});
            skLineSegment(sketch, "E2.79.0.1", {"start": v(-77.9, 191.47) * mm, "end": v(-67.9, 191.47) * mm});
            skLineSegment(sketch, "E2.80.0.1", {"start": v(-63.8, 119.5) * mm, "end": v(-53.8, 119.5) * mm});
            skLineSegment(sketch, "E2.81.0.1", {"start": v(-65.2, 167.48) * mm, "end": v(-55.2, 167.48) * mm});
            skLineSegment(sketch, "E2.82.0.1", {"start": v(-66.6, 215.46) * mm, "end": v(-56.6, 215.46) * mm});
            skLineSegment(sketch, "E2.83.0.1", {"start": v(-52.5, 143.49) * mm, "end": v(-42.5, 143.49) * mm});
            skLineSegment(sketch, "E2.84.0.1", {"start": v(-53.9, 191.47) * mm, "end": v(-43.9, 191.47) * mm});
            skLineSegment(sketch, "E2.85.0.1", {"start": v(-39.8, 119.5) * mm, "end": v(-29.8, 119.5) * mm});
            skLineSegment(sketch, "E2.86.0.1", {"start": v(-41.2, 167.48) * mm, "end": v(-31.2, 167.48) * mm});
            skLineSegment(sketch, "E2.87.0.1", {"start": v(-42.6, 215.46) * mm, "end": v(-32.6, 215.46) * mm});
            skLineSegment(sketch, "E2.88.0.1", {"start": v(-28.5, 143.49) * mm, "end": v(-18.5, 143.49) * mm});
            skLineSegment(sketch, "E2.89.0.1", {"start": v(-29.9, 191.47) * mm, "end": v(-19.9, 191.47) * mm});
            skLineSegment(sketch, "E2.90.0.1", {"start": v(-15.8, 119.5) * mm, "end": v(-5.8, 119.5) * mm});
            skLineSegment(sketch, "E2.91.0.1", {"start": v(-18.6, 215.46) * mm, "end": v(-8.6, 215.46) * mm});
            skLineSegment(sketch, "E2.92.0.1", {"start": v(-4.85, 155.48) * mm, "end": v(5.15, 155.48) * mm});
            skLineSegment(sketch, "E2.93.0.1", {"start": v(-6.25, 203.46) * mm, "end": v(3.75, 203.46) * mm});
            skLineSegment(sketch, "E2.94.0.1", {"start": v(6.45, 179.47) * mm, "end": v(16.45, 179.47) * mm});
            skLineSegment(sketch, "E2.95.0.1", {"start": v(-91.9, 191.47) * mm, "end": v(-91.9, 201.47) * mm});
            skLineSegment(sketch, "E2.96.0.1", {"start": v(-78.85, 155.48) * mm, "end": v(-78.85, 165.48) * mm});
            skLineSegment(sketch, "E2.97.0.1", {"start": v(-80.25, 203.46) * mm, "end": v(-80.25, 213.46) * mm});
            skLineSegment(sketch, "E2.98.0.1", {"start": v(-66.5, 143.49) * mm, "end": v(-66.5, 153.49) * mm});
            skLineSegment(sketch, "E2.99.0.1", {"start": v(-67.9, 191.47) * mm, "end": v(-67.9, 201.47) * mm});
            skLineSegment(sketch, "E2.100.0.1", {"start": v(-53.8, 119.5) * mm, "end": v(-53.8, 129.5) * mm});
            skLineSegment(sketch, "E2.101.0.1", {"start": v(-55.2, 167.48) * mm, "end": v(-55.2, 177.48) * mm});
            skLineSegment(sketch, "E2.102.0.1", {"start": v(-56.6, 215.46) * mm, "end": v(-56.6, 225.46) * mm});
            skLineSegment(sketch, "E2.103.0.1", {"start": v(-42.5, 143.49) * mm, "end": v(-42.5, 153.49) * mm});
            skLineSegment(sketch, "E2.104.0.1", {"start": v(-43.9, 191.47) * mm, "end": v(-43.9, 201.47) * mm});
            skLineSegment(sketch, "E2.105.0.1", {"start": v(-29.8, 119.5) * mm, "end": v(-29.8, 129.5) * mm});
            skLineSegment(sketch, "E2.106.0.1", {"start": v(-31.2, 167.48) * mm, "end": v(-31.2, 177.48) * mm});
            skLineSegment(sketch, "E2.107.0.1", {"start": v(-32.6, 215.46) * mm, "end": v(-32.6, 225.46) * mm});
            skLineSegment(sketch, "E2.108.0.1", {"start": v(-18.5, 143.49) * mm, "end": v(-18.5, 153.49) * mm});
            skLineSegment(sketch, "E2.109.0.1", {"start": v(-19.9, 191.47) * mm, "end": v(-19.9, 201.47) * mm});
            skLineSegment(sketch, "E2.110.0.1", {"start": v(-5.8, 119.5) * mm, "end": v(-5.8, 129.5) * mm});
            skLineSegment(sketch, "E2.111.0.1", {"start": v(-7.2, 167.48) * mm, "end": v(-7.2, 177.48) * mm});
            skLineSegment(sketch, "E2.112.0.1", {"start": v(-8.6, 215.46) * mm, "end": v(-8.6, 225.46) * mm});
            skLineSegment(sketch, "E2.113.0.1", {"start": v(5.15, 155.48) * mm, "end": v(5.15, 165.48) * mm});
            skLineSegment(sketch, "E2.114.0.1", {"start": v(3.75, 203.46) * mm, "end": v(3.75, 213.46) * mm});
            skLineSegment(sketch, "E2.115.0.1", {"start": v(16.45, 179.47) * mm, "end": v(16.45, 189.47) * mm});
            skLineSegment(sketch, "E2.116.0.1", {"start": v(-101.9, 201.47) * mm, "end": v(-91.9, 201.47) * mm});
            skLineSegment(sketch, "E2.117.0.1", {"start": v(-88.85, 165.48) * mm, "end": v(-78.85, 165.48) * mm});
            skLineSegment(sketch, "E2.118.0.1", {"start": v(-90.25, 213.46) * mm, "end": v(-80.25, 213.46) * mm});
            skLineSegment(sketch, "E2.119.0.1", {"start": v(-76.5, 153.49) * mm, "end": v(-66.5, 153.49) * mm});
            skLineSegment(sketch, "E2.120.0.1", {"start": v(-77.9, 201.47) * mm, "end": v(-67.9, 201.47) * mm});
            skLineSegment(sketch, "E2.121.0.1", {"start": v(-63.8, 129.5) * mm, "end": v(-53.8, 129.5) * mm});
            skLineSegment(sketch, "E2.122.0.1", {"start": v(-65.2, 177.48) * mm, "end": v(-55.2, 177.48) * mm});
            skLineSegment(sketch, "E2.123.0.1", {"start": v(-66.6, 225.46) * mm, "end": v(-56.6, 225.46) * mm});
            skLineSegment(sketch, "E2.124.0.1", {"start": v(-52.5, 153.49) * mm, "end": v(-42.5, 153.49) * mm});
            skLineSegment(sketch, "E2.125.0.1", {"start": v(-53.9, 201.47) * mm, "end": v(-43.9, 201.47) * mm});
            skLineSegment(sketch, "E2.126.0.1", {"start": v(-39.8, 129.5) * mm, "end": v(-29.8, 129.5) * mm});
            skLineSegment(sketch, "E2.127.0.1", {"start": v(-41.2, 177.48) * mm, "end": v(-31.2, 177.48) * mm});
            skLineSegment(sketch, "E2.128.0.1", {"start": v(-42.6, 225.46) * mm, "end": v(-32.6, 225.46) * mm});
            skLineSegment(sketch, "E2.129.0.1", {"start": v(-28.5, 153.49) * mm, "end": v(-18.5, 153.49) * mm});
            skLineSegment(sketch, "E2.130.0.1", {"start": v(-29.9, 201.47) * mm, "end": v(-19.9, 201.47) * mm});
            skLineSegment(sketch, "E2.131.0.1", {"start": v(-15.8, 129.5) * mm, "end": v(-5.8, 129.5) * mm});
            skLineSegment(sketch, "E2.132.0.1", {"start": v(-17.2, 177.48) * mm, "end": v(-7.2, 177.48) * mm});
            skLineSegment(sketch, "E2.133.0.1", {"start": v(-18.6, 225.46) * mm, "end": v(-8.6, 225.46) * mm});
            skLineSegment(sketch, "E2.134.0.1", {"start": v(-4.85, 165.48) * mm, "end": v(5.15, 165.48) * mm});
            skLineSegment(sketch, "E2.135.0.1", {"start": v(-6.25, 213.46) * mm, "end": v(3.75, 213.46) * mm});
            skLineSegment(sketch, "E2.136.0.1", {"start": v(6.45, 189.47) * mm, "end": v(16.45, 189.47) * mm});
            skLineSegment(sketch, "E2.137.0.1", {"start": v(-101.9, 191.47) * mm, "end": v(-101.9, 201.47) * mm});
            skLineSegment(sketch, "E2.138.0.1", {"start": v(-88.85, 155.48) * mm, "end": v(-88.85, 165.48) * mm});
            skLineSegment(sketch, "E2.139.0.1", {"start": v(-90.25, 203.46) * mm, "end": v(-90.25, 213.46) * mm});
            skLineSegment(sketch, "E2.140.0.1", {"start": v(-76.5, 143.49) * mm, "end": v(-76.5, 153.49) * mm});
            skLineSegment(sketch, "E2.141.0.1", {"start": v(-77.9, 191.47) * mm, "end": v(-77.9, 201.47) * mm});
            skLineSegment(sketch, "E2.142.0.1", {"start": v(-63.8, 119.5) * mm, "end": v(-63.8, 129.5) * mm});
            skLineSegment(sketch, "E2.143.0.1", {"start": v(-65.2, 167.48) * mm, "end": v(-65.2, 177.48) * mm});
            skLineSegment(sketch, "E2.144.0.1", {"start": v(-66.6, 215.46) * mm, "end": v(-66.6, 225.46) * mm});
            skLineSegment(sketch, "E2.145.0.1", {"start": v(-52.5, 143.49) * mm, "end": v(-52.5, 153.49) * mm});
            skLineSegment(sketch, "E2.146.0.1", {"start": v(-53.9, 191.47) * mm, "end": v(-53.9, 201.47) * mm});
            skLineSegment(sketch, "E2.147.0.1", {"start": v(-39.8, 119.5) * mm, "end": v(-39.8, 129.5) * mm});
            skLineSegment(sketch, "E2.148.0.1", {"start": v(-41.2, 167.48) * mm, "end": v(-41.2, 177.48) * mm});
            skLineSegment(sketch, "E2.149.0.1", {"start": v(-42.6, 215.46) * mm, "end": v(-42.6, 225.46) * mm});
            skLineSegment(sketch, "E2.150.0.1", {"start": v(-28.5, 143.49) * mm, "end": v(-28.5, 153.49) * mm});
            skLineSegment(sketch, "E2.151.0.1", {"start": v(-29.9, 191.47) * mm, "end": v(-29.9, 201.47) * mm});
            skLineSegment(sketch, "E2.152.0.1", {"start": v(-15.8, 119.5) * mm, "end": v(-15.8, 129.5) * mm});
            skLineSegment(sketch, "E2.153.0.1", {"start": v(-17.2, 167.48) * mm, "end": v(-17.2, 177.48) * mm});
            skLineSegment(sketch, "E2.154.0.1", {"start": v(-18.6, 215.46) * mm, "end": v(-18.6, 225.46) * mm});
            skLineSegment(sketch, "E2.155.0.1", {"start": v(-4.85, 155.48) * mm, "end": v(-4.85, 165.48) * mm});
            skLineSegment(sketch, "E2.156.0.1", {"start": v(-6.25, 203.46) * mm, "end": v(-6.25, 213.46) * mm});
            skLineSegment(sketch, "E2.157.0.1", {"start": v(6.45, 179.47) * mm, "end": v(6.45, 189.47) * mm});
            skLineSegment(sketch, "E2.158.0.1", {"start": v(-102.25, 203.46) * mm, "end": v(-92.25, 203.46) * mm});
            skLineSegment(sketch, "E2.159.0.1", {"start": v(-89.2, 167.48) * mm, "end": v(-79.2, 167.48) * mm});
            skLineSegment(sketch, "E2.160.0.1", {"start": v(-90.6, 215.46) * mm, "end": v(-80.6, 215.46) * mm});
            skLineSegment(sketch, "E2.161.0.1", {"start": v(-76.85, 155.48) * mm, "end": v(-66.85, 155.48) * mm});
            skLineSegment(sketch, "E2.162.0.1", {"start": v(-78.25, 203.46) * mm, "end": v(-68.25, 203.46) * mm});
            skLineSegment(sketch, "E2.163.0.1", {"start": v(-64.15, 131.5) * mm, "end": v(-54.15, 131.5) * mm});
            skLineSegment(sketch, "E2.164.0.1", {"start": v(-65.55, 179.47) * mm, "end": v(-55.55, 179.47) * mm});
            skLineSegment(sketch, "E2.165.0.1", {"start": v(-66.96, 227.45) * mm, "end": v(-56.96, 227.45) * mm});
            skLineSegment(sketch, "E2.166.0.1", {"start": v(-52.85, 155.48) * mm, "end": v(-42.85, 155.48) * mm});
            skLineSegment(sketch, "E2.167.0.1", {"start": v(-54.25, 203.46) * mm, "end": v(-44.25, 203.46) * mm});
            skLineSegment(sketch, "E2.168.0.1", {"start": v(-40.15, 131.5) * mm, "end": v(-30.15, 131.5) * mm});
            skLineSegment(sketch, "E2.169.0.1", {"start": v(-41.55, 179.47) * mm, "end": v(-31.55, 179.47) * mm});
            skLineSegment(sketch, "E2.170.0.1", {"start": v(-42.96, 227.45) * mm, "end": v(-32.96, 227.45) * mm});
            skLineSegment(sketch, "E2.171.0.1", {"start": v(-28.85, 155.48) * mm, "end": v(-18.85, 155.48) * mm});
            skLineSegment(sketch, "E2.172.0.1", {"start": v(-30.25, 203.46) * mm, "end": v(-20.25, 203.46) * mm});
            skLineSegment(sketch, "E2.173.0.1", {"start": v(-16.15, 131.5) * mm, "end": v(-6.15, 131.5) * mm});
            skLineSegment(sketch, "E2.174.0.1", {"start": v(-17.55, 179.47) * mm, "end": v(-7.55, 179.47) * mm});
            skLineSegment(sketch, "E2.175.0.1", {"start": v(-18.96, 227.45) * mm, "end": v(-8.96, 227.45) * mm});
            skLineSegment(sketch, "E2.176.0.1", {"start": v(-5.2, 167.48) * mm, "end": v(4.8, 167.48) * mm});
            skLineSegment(sketch, "E2.177.0.1", {"start": v(-6.6, 215.46) * mm, "end": v(3.4, 215.46) * mm});
            skLineSegment(sketch, "E2.178.0.1", {"start": v(6.1, 191.47) * mm, "end": v(16.1, 191.47) * mm});
            skLineSegment(sketch, "E2.179.0.1", {"start": v(-92.25, 203.46) * mm, "end": v(-92.25, 213.46) * mm});
            skLineSegment(sketch, "E2.180.0.1", {"start": v(-79.2, 167.48) * mm, "end": v(-79.2, 177.48) * mm});
            skLineSegment(sketch, "E2.181.0.1", {"start": v(-80.6, 215.46) * mm, "end": v(-80.6, 225.46) * mm});
            skLineSegment(sketch, "E2.182.0.1", {"start": v(-66.85, 155.48) * mm, "end": v(-66.85, 165.48) * mm});
            skLineSegment(sketch, "E2.183.0.1", {"start": v(-68.25, 203.46) * mm, "end": v(-68.25, 213.46) * mm});
            skLineSegment(sketch, "E2.184.0.1", {"start": v(-54.15, 131.5) * mm, "end": v(-54.15, 141.5) * mm});
            skLineSegment(sketch, "E2.185.0.1", {"start": v(-55.55, 179.47) * mm, "end": v(-55.55, 189.47) * mm});
            skLineSegment(sketch, "E2.186.0.1", {"start": v(-56.96, 227.45) * mm, "end": v(-56.96, 237.45) * mm});
            skLineSegment(sketch, "E2.187.0.1", {"start": v(-42.85, 155.48) * mm, "end": v(-42.85, 165.48) * mm});
            skLineSegment(sketch, "E2.188.0.1", {"start": v(-44.25, 203.46) * mm, "end": v(-44.25, 213.46) * mm});
            skLineSegment(sketch, "E2.189.0.1", {"start": v(-30.15, 131.5) * mm, "end": v(-30.15, 141.5) * mm});
            skLineSegment(sketch, "E2.190.0.1", {"start": v(-31.55, 179.47) * mm, "end": v(-31.55, 189.47) * mm});
            skLineSegment(sketch, "E2.191.0.1", {"start": v(-32.96, 227.45) * mm, "end": v(-32.96, 237.45) * mm});
            skLineSegment(sketch, "E2.192.0.1", {"start": v(-18.85, 155.48) * mm, "end": v(-18.85, 165.48) * mm});
            skLineSegment(sketch, "E2.193.0.1", {"start": v(-20.25, 203.46) * mm, "end": v(-20.25, 213.46) * mm});
            skLineSegment(sketch, "E2.194.0.1", {"start": v(-6.15, 131.5) * mm, "end": v(-6.15, 141.5) * mm});
            skLineSegment(sketch, "E2.195.0.1", {"start": v(-7.55, 179.47) * mm, "end": v(-7.55, 189.47) * mm});
            skLineSegment(sketch, "E2.196.0.1", {"start": v(-8.96, 227.45) * mm, "end": v(-8.96, 237.45) * mm});
            skLineSegment(sketch, "E2.197.0.1", {"start": v(4.8, 167.48) * mm, "end": v(4.8, 177.48) * mm});
            skLineSegment(sketch, "E2.198.0.1", {"start": v(3.4, 215.46) * mm, "end": v(3.4, 225.46) * mm});
            skLineSegment(sketch, "E2.199.0.1", {"start": v(16.1, 191.47) * mm, "end": v(16.1, 201.47) * mm});
            skLineSegment(sketch, "E2.200.0.1", {"start": v(-102.25, 213.46) * mm, "end": v(-92.25, 213.46) * mm});
            skLineSegment(sketch, "E2.201.0.1", {"start": v(-89.2, 177.48) * mm, "end": v(-79.2, 177.48) * mm});
            skLineSegment(sketch, "E2.202.0.1", {"start": v(-90.6, 225.46) * mm, "end": v(-80.6, 225.46) * mm});
            skLineSegment(sketch, "E2.203.0.1", {"start": v(-76.85, 165.48) * mm, "end": v(-66.85, 165.48) * mm});
            skLineSegment(sketch, "E2.204.0.1", {"start": v(-78.25, 213.46) * mm, "end": v(-68.25, 213.46) * mm});
            skLineSegment(sketch, "E2.205.0.1", {"start": v(-64.15, 141.5) * mm, "end": v(-54.15, 141.5) * mm});
            skLineSegment(sketch, "E2.206.0.1", {"start": v(-65.55, 189.47) * mm, "end": v(-55.55, 189.47) * mm});
            skLineSegment(sketch, "E2.207.0.1", {"start": v(-66.96, 237.45) * mm, "end": v(-56.96, 237.45) * mm});
            skLineSegment(sketch, "E2.208.0.1", {"start": v(-52.85, 165.48) * mm, "end": v(-42.85, 165.48) * mm});
            skLineSegment(sketch, "E2.209.0.1", {"start": v(-54.25, 213.46) * mm, "end": v(-44.25, 213.46) * mm});
            skLineSegment(sketch, "E2.210.0.1", {"start": v(-40.15, 141.5) * mm, "end": v(-30.15, 141.5) * mm});
            skLineSegment(sketch, "E2.211.0.1", {"start": v(-41.55, 189.47) * mm, "end": v(-31.55, 189.47) * mm});
            skLineSegment(sketch, "E2.212.0.1", {"start": v(-42.96, 237.45) * mm, "end": v(-32.96, 237.45) * mm});
            skLineSegment(sketch, "E2.213.0.1", {"start": v(-28.85, 165.48) * mm, "end": v(-18.85, 165.48) * mm});
            skLineSegment(sketch, "E2.214.0.1", {"start": v(-30.25, 213.46) * mm, "end": v(-20.25, 213.46) * mm});
            skLineSegment(sketch, "E2.215.0.1", {"start": v(-16.15, 141.5) * mm, "end": v(-6.15, 141.5) * mm});
            skLineSegment(sketch, "E2.216.0.1", {"start": v(-17.55, 189.47) * mm, "end": v(-7.55, 189.47) * mm});
            skLineSegment(sketch, "E2.217.0.1", {"start": v(-18.96, 237.45) * mm, "end": v(-8.96, 237.45) * mm});
            skLineSegment(sketch, "E2.218.0.1", {"start": v(-5.2, 177.48) * mm, "end": v(4.8, 177.48) * mm});
            skLineSegment(sketch, "E2.219.0.1", {"start": v(-6.6, 225.46) * mm, "end": v(3.4, 225.46) * mm});
            skLineSegment(sketch, "E2.220.0.1", {"start": v(6.1, 201.47) * mm, "end": v(16.1, 201.47) * mm});
            skLineSegment(sketch, "E2.221.0.1", {"start": v(-102.25, 203.46) * mm, "end": v(-102.25, 213.46) * mm});
            skLineSegment(sketch, "E2.222.0.1", {"start": v(-89.2, 167.48) * mm, "end": v(-89.2, 177.48) * mm});
            skLineSegment(sketch, "E2.223.0.1", {"start": v(-90.6, 215.46) * mm, "end": v(-90.6, 225.46) * mm});
            skLineSegment(sketch, "E2.224.0.1", {"start": v(-76.85, 155.48) * mm, "end": v(-76.85, 165.48) * mm});
            skLineSegment(sketch, "E2.225.0.1", {"start": v(-78.25, 203.46) * mm, "end": v(-78.25, 213.46) * mm});
            skLineSegment(sketch, "E2.226.0.1", {"start": v(-64.15, 131.5) * mm, "end": v(-64.15, 141.5) * mm});
            skLineSegment(sketch, "E2.227.0.1", {"start": v(-65.55, 179.47) * mm, "end": v(-65.55, 189.47) * mm});
            skLineSegment(sketch, "E2.228.0.1", {"start": v(-66.96, 227.45) * mm, "end": v(-66.96, 237.45) * mm});
            skLineSegment(sketch, "E2.229.0.1", {"start": v(-52.85, 155.48) * mm, "end": v(-52.85, 165.48) * mm});
            skLineSegment(sketch, "E2.230.0.1", {"start": v(-54.25, 203.46) * mm, "end": v(-54.25, 213.46) * mm});
            skLineSegment(sketch, "E2.231.0.1", {"start": v(-40.15, 131.5) * mm, "end": v(-40.15, 141.5) * mm});
            skLineSegment(sketch, "E2.232.0.1", {"start": v(-41.55, 179.47) * mm, "end": v(-41.55, 189.47) * mm});
            skLineSegment(sketch, "E2.233.0.1", {"start": v(-42.96, 227.45) * mm, "end": v(-42.96, 237.45) * mm});
            skLineSegment(sketch, "E2.234.0.1", {"start": v(-28.85, 155.48) * mm, "end": v(-28.85, 165.48) * mm});
            skLineSegment(sketch, "E2.235.0.1", {"start": v(-30.25, 203.46) * mm, "end": v(-30.25, 213.46) * mm});
            skLineSegment(sketch, "E2.236.0.1", {"start": v(-16.15, 131.5) * mm, "end": v(-16.15, 141.5) * mm});
            skLineSegment(sketch, "E2.237.0.1", {"start": v(-17.55, 179.47) * mm, "end": v(-17.55, 189.47) * mm});
            skLineSegment(sketch, "E2.238.0.1", {"start": v(-18.96, 227.45) * mm, "end": v(-18.96, 237.45) * mm});
            skLineSegment(sketch, "E2.239.0.1", {"start": v(-5.2, 167.48) * mm, "end": v(-5.2, 177.48) * mm});
            skLineSegment(sketch, "E2.240.0.1", {"start": v(-6.6, 215.46) * mm, "end": v(-6.6, 225.46) * mm});
            skLineSegment(sketch, "E2.241.0.1", {"start": v(6.1, 191.47) * mm, "end": v(6.1, 201.47) * mm});
            skLineSegment(sketch, "E2.242.0.1", {"start": v(-88.15, 131.5) * mm, "end": v(-78.15, 131.5) * mm});
            skLineSegment(sketch, "E2.243.0.1", {"start": v(-89.55, 179.47) * mm, "end": v(-79.55, 179.47) * mm});
            skLineSegment(sketch, "E2.244.0.1", {"start": v(-75.8, 119.5) * mm, "end": v(-65.8, 119.5) * mm});
            skLineSegment(sketch, "E2.245.0.1", {"start": v(-77.2, 167.48) * mm, "end": v(-67.2, 167.48) * mm});
            skLineSegment(sketch, "E2.246.0.1", {"start": v(-78.6, 215.46) * mm, "end": v(-68.6, 215.46) * mm});
            skLineSegment(sketch, "E2.247.0.1", {"start": v(-64.5, 143.49) * mm, "end": v(-54.5, 143.49) * mm});
            skLineSegment(sketch, "E2.248.0.1", {"start": v(-65.9, 191.47) * mm, "end": v(-55.9, 191.47) * mm});
            skLineSegment(sketch, "E2.249.0.1", {"start": v(-51.8, 119.5) * mm, "end": v(-41.8, 119.5) * mm});
            skLineSegment(sketch, "E2.250.0.1", {"start": v(-53.2, 167.48) * mm, "end": v(-43.2, 167.48) * mm});
            skLineSegment(sketch, "E2.251.0.1", {"start": v(-54.6, 215.46) * mm, "end": v(-44.6, 215.46) * mm});
            skLineSegment(sketch, "E2.252.0.1", {"start": v(-40.5, 143.49) * mm, "end": v(-30.5, 143.49) * mm});
            skLineSegment(sketch, "E2.253.0.1", {"start": v(-41.9, 191.47) * mm, "end": v(-31.9, 191.47) * mm});
            skLineSegment(sketch, "E2.254.0.1", {"start": v(-27.8, 119.5) * mm, "end": v(-17.8, 119.5) * mm});
            skLineSegment(sketch, "E2.255.0.1", {"start": v(-29.2, 167.48) * mm, "end": v(-19.2, 167.48) * mm});
            skLineSegment(sketch, "E2.256.0.1", {"start": v(-30.6, 215.46) * mm, "end": v(-20.6, 215.46) * mm});
            skLineSegment(sketch, "E2.257.0.1", {"start": v(-16.5, 143.49) * mm, "end": v(-6.5, 143.49) * mm});
            skLineSegment(sketch, "E2.258.0.1", {"start": v(-17.9, 191.47) * mm, "end": v(-7.9, 191.47) * mm});
            skLineSegment(sketch, "E2.259.0.1", {"start": v(-4.15, 131.5) * mm, "end": v(5.85, 131.5) * mm});
            skLineSegment(sketch, "E2.260.0.1", {"start": v(-5.55, 179.47) * mm, "end": v(4.45, 179.47) * mm});
            skLineSegment(sketch, "E2.261.0.1", {"start": v(7.15, 155.48) * mm, "end": v(17.15, 155.48) * mm});
            skLineSegment(sketch, "E2.262.0.1", {"start": v(5.75, 203.46) * mm, "end": v(15.75, 203.46) * mm});
            skLineSegment(sketch, "E2.263.0.1", {"start": v(-78.15, 131.5) * mm, "end": v(-78.15, 141.5) * mm});
            skLineSegment(sketch, "E2.264.0.1", {"start": v(-79.55, 179.47) * mm, "end": v(-79.55, 189.47) * mm});
            skLineSegment(sketch, "E2.265.0.1", {"start": v(-65.8, 119.5) * mm, "end": v(-65.8, 129.5) * mm});
            skLineSegment(sketch, "E2.266.0.1", {"start": v(-67.2, 167.48) * mm, "end": v(-67.2, 177.48) * mm});
            skLineSegment(sketch, "E2.267.0.1", {"start": v(-68.6, 215.46) * mm, "end": v(-68.6, 225.46) * mm});
            skLineSegment(sketch, "E2.268.0.1", {"start": v(-54.5, 143.49) * mm, "end": v(-54.5, 153.49) * mm});
            skLineSegment(sketch, "E2.269.0.1", {"start": v(-55.9, 191.47) * mm, "end": v(-55.9, 201.47) * mm});
            skLineSegment(sketch, "E2.270.0.1", {"start": v(-41.8, 119.5) * mm, "end": v(-41.8, 129.5) * mm});
            skLineSegment(sketch, "E2.271.0.1", {"start": v(-43.2, 167.48) * mm, "end": v(-43.2, 177.48) * mm});
            skLineSegment(sketch, "E2.272.0.1", {"start": v(-44.6, 215.46) * mm, "end": v(-44.6, 225.46) * mm});
            skLineSegment(sketch, "E2.273.0.1", {"start": v(-30.5, 143.49) * mm, "end": v(-30.5, 153.49) * mm});
            skLineSegment(sketch, "E2.274.0.1", {"start": v(-31.9, 191.47) * mm, "end": v(-31.9, 201.47) * mm});
            skLineSegment(sketch, "E2.275.0.1", {"start": v(-17.8, 119.5) * mm, "end": v(-17.8, 129.5) * mm});
            skLineSegment(sketch, "E2.276.0.1", {"start": v(-19.2, 167.48) * mm, "end": v(-19.2, 177.48) * mm});
            skLineSegment(sketch, "E2.277.0.1", {"start": v(-20.6, 215.46) * mm, "end": v(-20.6, 225.46) * mm});
            skLineSegment(sketch, "E2.278.0.1", {"start": v(-6.5, 143.49) * mm, "end": v(-6.5, 153.49) * mm});
            skLineSegment(sketch, "E2.279.0.1", {"start": v(-7.9, 191.47) * mm, "end": v(-7.9, 201.47) * mm});
            skLineSegment(sketch, "E2.280.0.1", {"start": v(5.85, 131.5) * mm, "end": v(5.85, 141.5) * mm});
            skLineSegment(sketch, "E2.281.0.1", {"start": v(4.45, 179.47) * mm, "end": v(4.45, 189.47) * mm});
            skLineSegment(sketch, "E2.282.0.1", {"start": v(17.15, 155.48) * mm, "end": v(17.15, 165.48) * mm});
            skLineSegment(sketch, "E2.283.0.1", {"start": v(15.75, 203.46) * mm, "end": v(15.75, 213.46) * mm});
            skLineSegment(sketch, "E2.284.0.1", {"start": v(-88.15, 141.5) * mm, "end": v(-78.15, 141.5) * mm});
            skLineSegment(sketch, "E2.285.0.1", {"start": v(-89.55, 189.47) * mm, "end": v(-79.55, 189.47) * mm});
            skLineSegment(sketch, "E2.286.0.1", {"start": v(-75.8, 129.5) * mm, "end": v(-65.8, 129.5) * mm});
            skLineSegment(sketch, "E2.287.0.1", {"start": v(-77.2, 177.48) * mm, "end": v(-67.2, 177.48) * mm});
            skLineSegment(sketch, "E2.288.0.1", {"start": v(-78.6, 225.46) * mm, "end": v(-68.6, 225.46) * mm});
            skLineSegment(sketch, "E2.289.0.1", {"start": v(-64.5, 153.49) * mm, "end": v(-54.5, 153.49) * mm});
            skLineSegment(sketch, "E2.290.0.1", {"start": v(-65.9, 201.47) * mm, "end": v(-55.9, 201.47) * mm});
            skLineSegment(sketch, "E2.291.0.1", {"start": v(-51.8, 129.5) * mm, "end": v(-41.8, 129.5) * mm});
            skLineSegment(sketch, "E2.292.0.1", {"start": v(-53.2, 177.48) * mm, "end": v(-43.2, 177.48) * mm});
            skLineSegment(sketch, "E2.293.0.1", {"start": v(-54.6, 225.46) * mm, "end": v(-44.6, 225.46) * mm});
            skLineSegment(sketch, "E2.294.0.1", {"start": v(-40.5, 153.49) * mm, "end": v(-30.5, 153.49) * mm});
            skLineSegment(sketch, "E2.295.0.1", {"start": v(-41.9, 201.47) * mm, "end": v(-31.9, 201.47) * mm});
            skLineSegment(sketch, "E2.296.0.1", {"start": v(-27.8, 129.5) * mm, "end": v(-17.8, 129.5) * mm});
            skLineSegment(sketch, "E2.297.0.1", {"start": v(-29.2, 177.48) * mm, "end": v(-19.2, 177.48) * mm});
            skLineSegment(sketch, "E2.298.0.1", {"start": v(-30.6, 225.46) * mm, "end": v(-20.6, 225.46) * mm});
            skLineSegment(sketch, "E2.299.0.1", {"start": v(-16.5, 153.49) * mm, "end": v(-6.5, 153.49) * mm});
            skLineSegment(sketch, "E2.300.0.1", {"start": v(-17.9, 201.47) * mm, "end": v(-7.9, 201.47) * mm});
            skLineSegment(sketch, "E2.301.0.1", {"start": v(-4.15, 141.5) * mm, "end": v(5.85, 141.5) * mm});
            skLineSegment(sketch, "E2.302.0.1", {"start": v(-5.55, 189.47) * mm, "end": v(4.45, 189.47) * mm});
            skLineSegment(sketch, "E2.303.0.1", {"start": v(7.15, 165.48) * mm, "end": v(17.15, 165.48) * mm});
            skLineSegment(sketch, "E2.304.0.1", {"start": v(5.75, 213.46) * mm, "end": v(15.75, 213.46) * mm});
            skLineSegment(sketch, "E2.305.0.1", {"start": v(-88.15, 131.5) * mm, "end": v(-88.15, 141.5) * mm});
            skLineSegment(sketch, "E2.306.0.1", {"start": v(-89.55, 179.47) * mm, "end": v(-89.55, 189.47) * mm});
            skLineSegment(sketch, "E2.307.0.1", {"start": v(-75.8, 119.5) * mm, "end": v(-75.8, 129.5) * mm});
            skLineSegment(sketch, "E2.308.0.1", {"start": v(-77.2, 167.48) * mm, "end": v(-77.2, 177.48) * mm});
            skLineSegment(sketch, "E2.309.0.1", {"start": v(-78.6, 215.46) * mm, "end": v(-78.6, 225.46) * mm});
            skLineSegment(sketch, "E2.310.0.1", {"start": v(-64.5, 143.49) * mm, "end": v(-64.5, 153.49) * mm});
            skLineSegment(sketch, "E2.311.0.1", {"start": v(-65.9, 191.47) * mm, "end": v(-65.9, 201.47) * mm});
            skLineSegment(sketch, "E2.312.0.1", {"start": v(-51.8, 119.5) * mm, "end": v(-51.8, 129.5) * mm});
            skLineSegment(sketch, "E2.313.0.1", {"start": v(-53.2, 167.48) * mm, "end": v(-53.2, 177.48) * mm});
            skLineSegment(sketch, "E2.314.0.1", {"start": v(-54.6, 215.46) * mm, "end": v(-54.6, 225.46) * mm});
            skLineSegment(sketch, "E2.315.0.1", {"start": v(-40.5, 143.49) * mm, "end": v(-40.5, 153.49) * mm});
            skLineSegment(sketch, "E2.316.0.1", {"start": v(-41.9, 191.47) * mm, "end": v(-41.9, 201.47) * mm});
            skLineSegment(sketch, "E2.317.0.1", {"start": v(-27.8, 119.5) * mm, "end": v(-27.8, 129.5) * mm});
            skLineSegment(sketch, "E2.318.0.1", {"start": v(-29.2, 167.48) * mm, "end": v(-29.2, 177.48) * mm});
            skLineSegment(sketch, "E2.319.0.1", {"start": v(-30.6, 215.46) * mm, "end": v(-30.6, 225.46) * mm});
            skLineSegment(sketch, "E2.320.0.1", {"start": v(-16.5, 143.49) * mm, "end": v(-16.5, 153.49) * mm});
            skLineSegment(sketch, "E2.321.0.1", {"start": v(-17.9, 191.47) * mm, "end": v(-17.9, 201.47) * mm});
            skLineSegment(sketch, "E2.322.0.1", {"start": v(-4.15, 131.5) * mm, "end": v(-4.15, 141.5) * mm});
            skLineSegment(sketch, "E2.323.0.1", {"start": v(-5.55, 179.47) * mm, "end": v(-5.55, 189.47) * mm});
            skLineSegment(sketch, "E2.324.0.1", {"start": v(7.15, 155.48) * mm, "end": v(7.15, 165.48) * mm});
            skLineSegment(sketch, "E2.325.0.1", {"start": v(5.75, 203.46) * mm, "end": v(5.75, 213.46) * mm});
            skLineSegment(sketch, "E2.326.0.1", {"start": v(-88.5, 143.49) * mm, "end": v(-78.5, 143.49) * mm});
            skLineSegment(sketch, "E2.327.0.1", {"start": v(-89.9, 191.47) * mm, "end": v(-79.9, 191.47) * mm});
            skLineSegment(sketch, "E2.328.0.1", {"start": v(-76.15, 131.5) * mm, "end": v(-66.15, 131.5) * mm});
            skLineSegment(sketch, "E2.329.0.1", {"start": v(-77.55, 179.47) * mm, "end": v(-67.55, 179.47) * mm});
            skLineSegment(sketch, "E2.330.0.1", {"start": v(-78.96, 227.45) * mm, "end": v(-68.96, 227.45) * mm});
            skLineSegment(sketch, "E2.331.0.1", {"start": v(-64.85, 155.48) * mm, "end": v(-54.85, 155.48) * mm});
            skLineSegment(sketch, "E2.332.0.1", {"start": v(-66.25, 203.46) * mm, "end": v(-56.25, 203.46) * mm});
            skLineSegment(sketch, "E2.333.0.1", {"start": v(-52.15, 131.5) * mm, "end": v(-42.15, 131.5) * mm});
            skLineSegment(sketch, "E2.334.0.1", {"start": v(-53.55, 179.47) * mm, "end": v(-43.55, 179.47) * mm});
            skLineSegment(sketch, "E2.335.0.1", {"start": v(-54.96, 227.45) * mm, "end": v(-44.96, 227.45) * mm});
            skLineSegment(sketch, "E2.336.0.1", {"start": v(-40.85, 155.48) * mm, "end": v(-30.85, 155.48) * mm});
            skLineSegment(sketch, "E2.337.0.1", {"start": v(-42.25, 203.46) * mm, "end": v(-32.25, 203.46) * mm});
            skLineSegment(sketch, "E2.338.0.1", {"start": v(-28.15, 131.5) * mm, "end": v(-18.15, 131.5) * mm});
            skLineSegment(sketch, "E2.339.0.1", {"start": v(-29.55, 179.47) * mm, "end": v(-19.55, 179.47) * mm});
            skLineSegment(sketch, "E2.340.0.1", {"start": v(-30.96, 227.45) * mm, "end": v(-20.96, 227.45) * mm});
            skLineSegment(sketch, "E2.341.0.1", {"start": v(-16.85, 155.48) * mm, "end": v(-6.85, 155.48) * mm});
            skLineSegment(sketch, "E2.342.0.1", {"start": v(-18.25, 203.46) * mm, "end": v(-8.25, 203.46) * mm});
            skLineSegment(sketch, "E2.343.0.1", {"start": v(-4.5, 143.49) * mm, "end": v(5.5, 143.49) * mm});
            skLineSegment(sketch, "E2.344.0.1", {"start": v(-5.9, 191.47) * mm, "end": v(4.1, 191.47) * mm});
            skLineSegment(sketch, "E2.345.0.1", {"start": v(6.8, 167.48) * mm, "end": v(16.8, 167.48) * mm});
            skLineSegment(sketch, "E2.346.0.1", {"start": v(-16.85, 165.48) * mm, "end": v(-6.85, 165.48) * mm});
            skLineSegment(sketch, "E2.347.0.1", {"start": v(-17.2, 167.48) * mm, "end": v(-7.2, 167.48) * mm});
            skLineSegment(sketch, "E2.0.1.0", {"start": v(-218.55, 55.47) * mm, "end": v(-218.55, 65.47) * mm});
            skLineSegment(sketch, "E2.1.1.0", {"start": v(-208.55, 55.47) * mm, "end": v(-208.55, 65.47) * mm});
            skLineSegment(sketch, "E2.2.1.0", {"start": v(-218.55, 65.47) * mm, "end": v(-208.55, 65.47) * mm});
            skLineSegment(sketch, "E2.3.1.0", {"start": v(-217.5, 19.49) * mm, "end": v(-207.5, 19.49) * mm});
            skLineSegment(sketch, "E2.4.1.0", {"start": v(-207.5, 19.49) * mm, "end": v(-207.5, 29.49) * mm});
            skLineSegment(sketch, "E2.5.1.0", {"start": v(-217.5, 29.49) * mm, "end": v(-207.5, 29.49) * mm});
            skLineSegment(sketch, "E2.6.1.0", {"start": v(-217.5, 19.49) * mm, "end": v(-217.5, 29.49) * mm});
            skLineSegment(sketch, "E2.7.1.0", {"start": v(-217.85, 31.48) * mm, "end": v(-207.85, 31.48) * mm});
            skLineSegment(sketch, "E2.8.1.0", {"start": v(-207.85, 31.48) * mm, "end": v(-207.85, 41.48) * mm});
            skLineSegment(sketch, "E2.9.1.0", {"start": v(-217.85, 41.48) * mm, "end": v(-207.85, 41.48) * mm});
            skLineSegment(sketch, "E2.10.1.0", {"start": v(-217.85, 31.48) * mm, "end": v(-217.85, 41.48) * mm});
            skLineSegment(sketch, "E2.11.1.0", {"start": v(-218.2, 43.48) * mm, "end": v(-208.2, 43.48) * mm});
            skLineSegment(sketch, "E2.12.1.0", {"start": v(-208.2, 43.48) * mm, "end": v(-208.2, 53.48) * mm});
            skLineSegment(sketch, "E2.13.1.0", {"start": v(-218.2, 53.48) * mm, "end": v(-208.2, 53.48) * mm});
            skLineSegment(sketch, "E2.14.1.0", {"start": v(-218.2, 43.48) * mm, "end": v(-218.2, 53.48) * mm});
            skLineSegment(sketch, "E2.15.1.0", {"start": v(-218.55, 55.47) * mm, "end": v(-208.55, 55.47) * mm});
            skLineSegment(sketch, "E2.16.1.0", {"start": v(-205.5, 19.49) * mm, "end": v(-205.5, 29.49) * mm});
            skLineSegment(sketch, "E2.17.1.0", {"start": v(-206.9, 67.47) * mm, "end": v(-206.9, 77.47) * mm});
            skLineSegment(sketch, "E2.18.1.0", {"start": v(-193.15, 7.5) * mm, "end": v(-193.15, 17.5) * mm});
            skLineSegment(sketch, "E2.19.1.0", {"start": v(-194.55, 55.47) * mm, "end": v(-194.55, 65.47) * mm});
            skLineSegment(sketch, "E2.20.1.0", {"start": v(-195.96, 103.45) * mm, "end": v(-195.96, 113.45) * mm});
            skLineSegment(sketch, "E2.21.1.0", {"start": v(-181.85, 31.48) * mm, "end": v(-181.85, 41.48) * mm});
            skLineSegment(sketch, "E2.22.1.0", {"start": v(-183.25, 79.46) * mm, "end": v(-183.25, 89.46) * mm});
            skLineSegment(sketch, "E2.23.1.0", {"start": v(-169.15, 7.5) * mm, "end": v(-169.15, 17.5) * mm});
            skLineSegment(sketch, "E2.24.1.0", {"start": v(-170.55, 55.47) * mm, "end": v(-170.55, 65.47) * mm});
            skLineSegment(sketch, "E2.25.1.0", {"start": v(-171.96, 103.45) * mm, "end": v(-171.96, 113.45) * mm});
            skLineSegment(sketch, "E2.26.1.0", {"start": v(-157.85, 31.48) * mm, "end": v(-157.85, 41.48) * mm});
            skLineSegment(sketch, "E2.27.1.0", {"start": v(-159.25, 79.46) * mm, "end": v(-159.25, 89.46) * mm});
            skLineSegment(sketch, "E2.28.1.0", {"start": v(-145.15, 7.5) * mm, "end": v(-145.15, 17.5) * mm});
            skLineSegment(sketch, "E2.29.1.0", {"start": v(-146.55, 55.47) * mm, "end": v(-146.55, 65.47) * mm});
            skLineSegment(sketch, "E2.30.1.0", {"start": v(-147.96, 103.45) * mm, "end": v(-147.96, 113.45) * mm});
            skLineSegment(sketch, "E2.31.1.0", {"start": v(-133.85, 31.48) * mm, "end": v(-133.85, 41.48) * mm});
            skLineSegment(sketch, "E2.32.1.0", {"start": v(-135.25, 79.46) * mm, "end": v(-135.25, 89.46) * mm});
            skLineSegment(sketch, "E2.33.1.0", {"start": v(-121.5, 19.49) * mm, "end": v(-121.5, 29.49) * mm});
            skLineSegment(sketch, "E2.34.1.0", {"start": v(-122.9, 67.47) * mm, "end": v(-122.9, 77.47) * mm});
            skLineSegment(sketch, "E2.35.1.0", {"start": v(-110.2, 43.48) * mm, "end": v(-110.2, 53.48) * mm});
            skLineSegment(sketch, "E2.36.1.0", {"start": v(-195.5, 19.49) * mm, "end": v(-195.5, 29.49) * mm});
            skLineSegment(sketch, "E2.37.1.0", {"start": v(-196.9, 67.47) * mm, "end": v(-196.9, 77.47) * mm});
            skLineSegment(sketch, "E2.38.1.0", {"start": v(-183.15, 7.5) * mm, "end": v(-183.15, 17.5) * mm});
            skLineSegment(sketch, "E2.39.1.0", {"start": v(-184.55, 55.47) * mm, "end": v(-184.55, 65.47) * mm});
            skLineSegment(sketch, "E2.40.1.0", {"start": v(-185.96, 103.45) * mm, "end": v(-185.96, 113.45) * mm});
            skLineSegment(sketch, "E2.41.1.0", {"start": v(-171.85, 31.48) * mm, "end": v(-171.85, 41.48) * mm});
            skLineSegment(sketch, "E2.42.1.0", {"start": v(-173.25, 79.46) * mm, "end": v(-173.25, 89.46) * mm});
            skLineSegment(sketch, "E2.43.1.0", {"start": v(-159.15, 7.5) * mm, "end": v(-159.15, 17.5) * mm});
            skLineSegment(sketch, "E2.44.1.0", {"start": v(-160.55, 55.47) * mm, "end": v(-160.55, 65.47) * mm});
            skLineSegment(sketch, "E2.45.1.0", {"start": v(-161.96, 103.45) * mm, "end": v(-161.96, 113.45) * mm});
            skLineSegment(sketch, "E2.46.1.0", {"start": v(-147.85, 31.48) * mm, "end": v(-147.85, 41.48) * mm});
            skLineSegment(sketch, "E2.47.1.0", {"start": v(-149.25, 79.46) * mm, "end": v(-149.25, 89.46) * mm});
            skLineSegment(sketch, "E2.48.1.0", {"start": v(-135.15, 7.5) * mm, "end": v(-135.15, 17.5) * mm});
            skLineSegment(sketch, "E2.49.1.0", {"start": v(-136.55, 55.47) * mm, "end": v(-136.55, 65.47) * mm});
            skLineSegment(sketch, "E2.50.1.0", {"start": v(-137.96, 103.45) * mm, "end": v(-137.96, 113.45) * mm});
            skLineSegment(sketch, "E2.51.1.0", {"start": v(-123.85, 31.48) * mm, "end": v(-123.85, 41.48) * mm});
            skLineSegment(sketch, "E2.52.1.0", {"start": v(-125.25, 79.46) * mm, "end": v(-125.25, 89.46) * mm});
            skLineSegment(sketch, "E2.53.1.0", {"start": v(-111.5, 19.49) * mm, "end": v(-111.5, 29.49) * mm});
            skLineSegment(sketch, "E2.54.1.0", {"start": v(-112.9, 67.47) * mm, "end": v(-112.9, 77.47) * mm});
            skLineSegment(sketch, "E2.55.1.0", {"start": v(-100.2, 43.48) * mm, "end": v(-100.2, 53.48) * mm});
            skLineSegment(sketch, "E2.56.1.0", {"start": v(-205.5, 29.49) * mm, "end": v(-195.5, 29.49) * mm});
            skLineSegment(sketch, "E2.57.1.0", {"start": v(-206.9, 77.47) * mm, "end": v(-196.9, 77.47) * mm});
            skLineSegment(sketch, "E2.58.1.0", {"start": v(-193.15, 17.5) * mm, "end": v(-183.15, 17.5) * mm});
            skLineSegment(sketch, "E2.59.1.0", {"start": v(-194.55, 65.47) * mm, "end": v(-184.55, 65.47) * mm});
            skLineSegment(sketch, "E2.60.1.0", {"start": v(-195.96, 113.45) * mm, "end": v(-185.96, 113.45) * mm});
            skLineSegment(sketch, "E2.61.1.0", {"start": v(-181.85, 41.48) * mm, "end": v(-171.85, 41.48) * mm});
            skLineSegment(sketch, "E2.62.1.0", {"start": v(-183.25, 89.46) * mm, "end": v(-173.25, 89.46) * mm});
            skLineSegment(sketch, "E2.63.1.0", {"start": v(-169.15, 17.5) * mm, "end": v(-159.15, 17.5) * mm});
            skLineSegment(sketch, "E2.64.1.0", {"start": v(-170.55, 65.47) * mm, "end": v(-160.55, 65.47) * mm});
            skLineSegment(sketch, "E2.65.1.0", {"start": v(-171.96, 113.45) * mm, "end": v(-161.96, 113.45) * mm});
            skLineSegment(sketch, "E2.66.1.0", {"start": v(-157.85, 41.48) * mm, "end": v(-147.85, 41.48) * mm});
            skLineSegment(sketch, "E2.67.1.0", {"start": v(-159.25, 89.46) * mm, "end": v(-149.25, 89.46) * mm});
            skLineSegment(sketch, "E2.68.1.0", {"start": v(-145.15, 17.5) * mm, "end": v(-135.15, 17.5) * mm});
            skLineSegment(sketch, "E2.69.1.0", {"start": v(-146.55, 65.47) * mm, "end": v(-136.55, 65.47) * mm});
            skLineSegment(sketch, "E2.70.1.0", {"start": v(-147.96, 113.45) * mm, "end": v(-137.96, 113.45) * mm});
            skLineSegment(sketch, "E2.71.1.0", {"start": v(-135.25, 89.46) * mm, "end": v(-125.25, 89.46) * mm});
            skLineSegment(sketch, "E2.72.1.0", {"start": v(-121.5, 29.49) * mm, "end": v(-111.5, 29.49) * mm});
            skLineSegment(sketch, "E2.73.1.0", {"start": v(-122.9, 77.47) * mm, "end": v(-112.9, 77.47) * mm});
            skLineSegment(sketch, "E2.74.1.0", {"start": v(-110.2, 53.48) * mm, "end": v(-100.2, 53.48) * mm});
            skLineSegment(sketch, "E2.75.1.0", {"start": v(-218.9, 67.47) * mm, "end": v(-208.9, 67.47) * mm});
            skLineSegment(sketch, "E2.76.1.0", {"start": v(-205.85, 31.48) * mm, "end": v(-195.85, 31.48) * mm});
            skLineSegment(sketch, "E2.77.1.0", {"start": v(-207.25, 79.46) * mm, "end": v(-197.25, 79.46) * mm});
            skLineSegment(sketch, "E2.78.1.0", {"start": v(-193.5, 19.49) * mm, "end": v(-183.5, 19.49) * mm});
            skLineSegment(sketch, "E2.79.1.0", {"start": v(-194.9, 67.47) * mm, "end": v(-184.9, 67.47) * mm});
            skLineSegment(sketch, "E2.80.1.0", {"start": v(-180.8, -4.5) * mm, "end": v(-170.8, -4.5) * mm});
            skLineSegment(sketch, "E2.81.1.0", {"start": v(-182.2, 43.48) * mm, "end": v(-172.2, 43.48) * mm});
            skLineSegment(sketch, "E2.82.1.0", {"start": v(-183.6, 91.46) * mm, "end": v(-173.6, 91.46) * mm});
            skLineSegment(sketch, "E2.83.1.0", {"start": v(-169.5, 19.49) * mm, "end": v(-159.5, 19.49) * mm});
            skLineSegment(sketch, "E2.84.1.0", {"start": v(-170.9, 67.47) * mm, "end": v(-160.9, 67.47) * mm});
            skLineSegment(sketch, "E2.85.1.0", {"start": v(-156.8, -4.5) * mm, "end": v(-146.8, -4.5) * mm});
            skLineSegment(sketch, "E2.86.1.0", {"start": v(-158.2, 43.48) * mm, "end": v(-148.2, 43.48) * mm});
            skLineSegment(sketch, "E2.87.1.0", {"start": v(-159.6, 91.46) * mm, "end": v(-149.6, 91.46) * mm});
            skLineSegment(sketch, "E2.88.1.0", {"start": v(-145.5, 19.49) * mm, "end": v(-135.5, 19.49) * mm});
            skLineSegment(sketch, "E2.89.1.0", {"start": v(-146.9, 67.47) * mm, "end": v(-136.9, 67.47) * mm});
            skLineSegment(sketch, "E2.90.1.0", {"start": v(-132.8, -4.5) * mm, "end": v(-122.8, -4.5) * mm});
            skLineSegment(sketch, "E2.91.1.0", {"start": v(-135.6, 91.46) * mm, "end": v(-125.6, 91.46) * mm});
            skLineSegment(sketch, "E2.92.1.0", {"start": v(-121.85, 31.48) * mm, "end": v(-111.85, 31.48) * mm});
            skLineSegment(sketch, "E2.93.1.0", {"start": v(-123.25, 79.46) * mm, "end": v(-113.25, 79.46) * mm});
            skLineSegment(sketch, "E2.94.1.0", {"start": v(-110.55, 55.47) * mm, "end": v(-100.55, 55.47) * mm});
            skLineSegment(sketch, "E2.95.1.0", {"start": v(-208.9, 67.47) * mm, "end": v(-208.9, 77.47) * mm});
            skLineSegment(sketch, "E2.96.1.0", {"start": v(-195.85, 31.48) * mm, "end": v(-195.85, 41.48) * mm});
            skLineSegment(sketch, "E2.97.1.0", {"start": v(-197.25, 79.46) * mm, "end": v(-197.25, 89.46) * mm});
            skLineSegment(sketch, "E2.98.1.0", {"start": v(-183.5, 19.49) * mm, "end": v(-183.5, 29.49) * mm});
            skLineSegment(sketch, "E2.99.1.0", {"start": v(-184.9, 67.47) * mm, "end": v(-184.9, 77.47) * mm});
            skLineSegment(sketch, "E2.100.1.0", {"start": v(-170.8, -4.5) * mm, "end": v(-170.8, 5.5) * mm});
            skLineSegment(sketch, "E2.101.1.0", {"start": v(-172.2, 43.48) * mm, "end": v(-172.2, 53.48) * mm});
            skLineSegment(sketch, "E2.102.1.0", {"start": v(-173.6, 91.46) * mm, "end": v(-173.6, 101.46) * mm});
            skLineSegment(sketch, "E2.103.1.0", {"start": v(-159.5, 19.49) * mm, "end": v(-159.5, 29.49) * mm});
            skLineSegment(sketch, "E2.104.1.0", {"start": v(-160.9, 67.47) * mm, "end": v(-160.9, 77.47) * mm});
            skLineSegment(sketch, "E2.105.1.0", {"start": v(-146.8, -4.5) * mm, "end": v(-146.8, 5.5) * mm});
            skLineSegment(sketch, "E2.106.1.0", {"start": v(-148.2, 43.48) * mm, "end": v(-148.2, 53.48) * mm});
            skLineSegment(sketch, "E2.107.1.0", {"start": v(-149.6, 91.46) * mm, "end": v(-149.6, 101.46) * mm});
            skLineSegment(sketch, "E2.108.1.0", {"start": v(-135.5, 19.49) * mm, "end": v(-135.5, 29.49) * mm});
            skLineSegment(sketch, "E2.109.1.0", {"start": v(-136.9, 67.47) * mm, "end": v(-136.9, 77.47) * mm});
            skLineSegment(sketch, "E2.110.1.0", {"start": v(-122.8, -4.5) * mm, "end": v(-122.8, 5.5) * mm});
            skLineSegment(sketch, "E2.111.1.0", {"start": v(-124.2, 43.48) * mm, "end": v(-124.2, 53.48) * mm});
            skLineSegment(sketch, "E2.112.1.0", {"start": v(-125.6, 91.46) * mm, "end": v(-125.6, 101.46) * mm});
            skLineSegment(sketch, "E2.113.1.0", {"start": v(-111.85, 31.48) * mm, "end": v(-111.85, 41.48) * mm});
            skLineSegment(sketch, "E2.114.1.0", {"start": v(-113.25, 79.46) * mm, "end": v(-113.25, 89.46) * mm});
            skLineSegment(sketch, "E2.115.1.0", {"start": v(-100.55, 55.47) * mm, "end": v(-100.55, 65.47) * mm});
            skLineSegment(sketch, "E2.116.1.0", {"start": v(-218.9, 77.47) * mm, "end": v(-208.9, 77.47) * mm});
            skLineSegment(sketch, "E2.117.1.0", {"start": v(-205.85, 41.48) * mm, "end": v(-195.85, 41.48) * mm});
            skLineSegment(sketch, "E2.118.1.0", {"start": v(-207.25, 89.46) * mm, "end": v(-197.25, 89.46) * mm});
            skLineSegment(sketch, "E2.119.1.0", {"start": v(-193.5, 29.49) * mm, "end": v(-183.5, 29.49) * mm});
            skLineSegment(sketch, "E2.120.1.0", {"start": v(-194.9, 77.47) * mm, "end": v(-184.9, 77.47) * mm});
            skLineSegment(sketch, "E2.121.1.0", {"start": v(-180.8, 5.5) * mm, "end": v(-170.8, 5.5) * mm});
            skLineSegment(sketch, "E2.122.1.0", {"start": v(-182.2, 53.48) * mm, "end": v(-172.2, 53.48) * mm});
            skLineSegment(sketch, "E2.123.1.0", {"start": v(-183.6, 101.46) * mm, "end": v(-173.6, 101.46) * mm});
            skLineSegment(sketch, "E2.124.1.0", {"start": v(-169.5, 29.49) * mm, "end": v(-159.5, 29.49) * mm});
            skLineSegment(sketch, "E2.125.1.0", {"start": v(-170.9, 77.47) * mm, "end": v(-160.9, 77.47) * mm});
            skLineSegment(sketch, "E2.126.1.0", {"start": v(-156.8, 5.5) * mm, "end": v(-146.8, 5.5) * mm});
            skLineSegment(sketch, "E2.127.1.0", {"start": v(-158.2, 53.48) * mm, "end": v(-148.2, 53.48) * mm});
            skLineSegment(sketch, "E2.128.1.0", {"start": v(-159.6, 101.46) * mm, "end": v(-149.6, 101.46) * mm});
            skLineSegment(sketch, "E2.129.1.0", {"start": v(-145.5, 29.49) * mm, "end": v(-135.5, 29.49) * mm});
            skLineSegment(sketch, "E2.130.1.0", {"start": v(-146.9, 77.47) * mm, "end": v(-136.9, 77.47) * mm});
            skLineSegment(sketch, "E2.131.1.0", {"start": v(-132.8, 5.5) * mm, "end": v(-122.8, 5.5) * mm});
            skLineSegment(sketch, "E2.132.1.0", {"start": v(-134.2, 53.48) * mm, "end": v(-124.2, 53.48) * mm});
            skLineSegment(sketch, "E2.133.1.0", {"start": v(-135.6, 101.46) * mm, "end": v(-125.6, 101.46) * mm});
            skLineSegment(sketch, "E2.134.1.0", {"start": v(-121.85, 41.48) * mm, "end": v(-111.85, 41.48) * mm});
            skLineSegment(sketch, "E2.135.1.0", {"start": v(-123.25, 89.46) * mm, "end": v(-113.25, 89.46) * mm});
            skLineSegment(sketch, "E2.136.1.0", {"start": v(-110.55, 65.47) * mm, "end": v(-100.55, 65.47) * mm});
            skLineSegment(sketch, "E2.137.1.0", {"start": v(-218.9, 67.47) * mm, "end": v(-218.9, 77.47) * mm});
            skLineSegment(sketch, "E2.138.1.0", {"start": v(-205.85, 31.48) * mm, "end": v(-205.85, 41.48) * mm});
            skLineSegment(sketch, "E2.139.1.0", {"start": v(-207.25, 79.46) * mm, "end": v(-207.25, 89.46) * mm});
            skLineSegment(sketch, "E2.140.1.0", {"start": v(-193.5, 19.49) * mm, "end": v(-193.5, 29.49) * mm});
            skLineSegment(sketch, "E2.141.1.0", {"start": v(-194.9, 67.47) * mm, "end": v(-194.9, 77.47) * mm});
            skLineSegment(sketch, "E2.142.1.0", {"start": v(-180.8, -4.5) * mm, "end": v(-180.8, 5.5) * mm});
            skLineSegment(sketch, "E2.143.1.0", {"start": v(-182.2, 43.48) * mm, "end": v(-182.2, 53.48) * mm});
            skLineSegment(sketch, "E2.144.1.0", {"start": v(-183.6, 91.46) * mm, "end": v(-183.6, 101.46) * mm});
            skLineSegment(sketch, "E2.145.1.0", {"start": v(-169.5, 19.49) * mm, "end": v(-169.5, 29.49) * mm});
            skLineSegment(sketch, "E2.146.1.0", {"start": v(-170.9, 67.47) * mm, "end": v(-170.9, 77.47) * mm});
            skLineSegment(sketch, "E2.147.1.0", {"start": v(-156.8, -4.5) * mm, "end": v(-156.8, 5.5) * mm});
            skLineSegment(sketch, "E2.148.1.0", {"start": v(-158.2, 43.48) * mm, "end": v(-158.2, 53.48) * mm});
            skLineSegment(sketch, "E2.149.1.0", {"start": v(-159.6, 91.46) * mm, "end": v(-159.6, 101.46) * mm});
            skLineSegment(sketch, "E2.150.1.0", {"start": v(-145.5, 19.49) * mm, "end": v(-145.5, 29.49) * mm});
            skLineSegment(sketch, "E2.151.1.0", {"start": v(-146.9, 67.47) * mm, "end": v(-146.9, 77.47) * mm});
            skLineSegment(sketch, "E2.152.1.0", {"start": v(-132.8, -4.5) * mm, "end": v(-132.8, 5.5) * mm});
            skLineSegment(sketch, "E2.153.1.0", {"start": v(-134.2, 43.48) * mm, "end": v(-134.2, 53.48) * mm});
            skLineSegment(sketch, "E2.154.1.0", {"start": v(-135.6, 91.46) * mm, "end": v(-135.6, 101.46) * mm});
            skLineSegment(sketch, "E2.155.1.0", {"start": v(-121.85, 31.48) * mm, "end": v(-121.85, 41.48) * mm});
            skLineSegment(sketch, "E2.156.1.0", {"start": v(-123.25, 79.46) * mm, "end": v(-123.25, 89.46) * mm});
            skLineSegment(sketch, "E2.157.1.0", {"start": v(-110.55, 55.47) * mm, "end": v(-110.55, 65.47) * mm});
            skLineSegment(sketch, "E2.158.1.0", {"start": v(-219.25, 79.46) * mm, "end": v(-209.25, 79.46) * mm});
            skLineSegment(sketch, "E2.159.1.0", {"start": v(-206.2, 43.48) * mm, "end": v(-196.2, 43.48) * mm});
            skLineSegment(sketch, "E2.160.1.0", {"start": v(-207.6, 91.46) * mm, "end": v(-197.6, 91.46) * mm});
            skLineSegment(sketch, "E2.161.1.0", {"start": v(-193.85, 31.48) * mm, "end": v(-183.85, 31.48) * mm});
            skLineSegment(sketch, "E2.162.1.0", {"start": v(-195.25, 79.46) * mm, "end": v(-185.25, 79.46) * mm});
            skLineSegment(sketch, "E2.163.1.0", {"start": v(-181.15, 7.5) * mm, "end": v(-171.15, 7.5) * mm});
            skLineSegment(sketch, "E2.164.1.0", {"start": v(-182.55, 55.47) * mm, "end": v(-172.55, 55.47) * mm});
            skLineSegment(sketch, "E2.165.1.0", {"start": v(-183.96, 103.45) * mm, "end": v(-173.96, 103.45) * mm});
            skLineSegment(sketch, "E2.166.1.0", {"start": v(-169.85, 31.48) * mm, "end": v(-159.85, 31.48) * mm});
            skLineSegment(sketch, "E2.167.1.0", {"start": v(-171.25, 79.46) * mm, "end": v(-161.25, 79.46) * mm});
            skLineSegment(sketch, "E2.168.1.0", {"start": v(-157.15, 7.5) * mm, "end": v(-147.15, 7.5) * mm});
            skLineSegment(sketch, "E2.169.1.0", {"start": v(-158.55, 55.47) * mm, "end": v(-148.55, 55.47) * mm});
            skLineSegment(sketch, "E2.170.1.0", {"start": v(-159.96, 103.45) * mm, "end": v(-149.96, 103.45) * mm});
            skLineSegment(sketch, "E2.171.1.0", {"start": v(-145.85, 31.48) * mm, "end": v(-135.85, 31.48) * mm});
            skLineSegment(sketch, "E2.172.1.0", {"start": v(-147.25, 79.46) * mm, "end": v(-137.25, 79.46) * mm});
            skLineSegment(sketch, "E2.173.1.0", {"start": v(-133.15, 7.5) * mm, "end": v(-123.15, 7.5) * mm});
            skLineSegment(sketch, "E2.174.1.0", {"start": v(-134.55, 55.47) * mm, "end": v(-124.55, 55.47) * mm});
            skLineSegment(sketch, "E2.175.1.0", {"start": v(-135.96, 103.45) * mm, "end": v(-125.96, 103.45) * mm});
            skLineSegment(sketch, "E2.176.1.0", {"start": v(-122.2, 43.48) * mm, "end": v(-112.2, 43.48) * mm});
            skLineSegment(sketch, "E2.177.1.0", {"start": v(-123.6, 91.46) * mm, "end": v(-113.6, 91.46) * mm});
            skLineSegment(sketch, "E2.178.1.0", {"start": v(-110.9, 67.47) * mm, "end": v(-100.9, 67.47) * mm});
            skLineSegment(sketch, "E2.179.1.0", {"start": v(-209.25, 79.46) * mm, "end": v(-209.25, 89.46) * mm});
            skLineSegment(sketch, "E2.180.1.0", {"start": v(-196.2, 43.48) * mm, "end": v(-196.2, 53.48) * mm});
            skLineSegment(sketch, "E2.181.1.0", {"start": v(-197.6, 91.46) * mm, "end": v(-197.6, 101.46) * mm});
            skLineSegment(sketch, "E2.182.1.0", {"start": v(-183.85, 31.48) * mm, "end": v(-183.85, 41.48) * mm});
            skLineSegment(sketch, "E2.183.1.0", {"start": v(-185.25, 79.46) * mm, "end": v(-185.25, 89.46) * mm});
            skLineSegment(sketch, "E2.184.1.0", {"start": v(-171.15, 7.5) * mm, "end": v(-171.15, 17.5) * mm});
            skLineSegment(sketch, "E2.185.1.0", {"start": v(-172.55, 55.47) * mm, "end": v(-172.55, 65.47) * mm});
            skLineSegment(sketch, "E2.186.1.0", {"start": v(-173.96, 103.45) * mm, "end": v(-173.96, 113.45) * mm});
            skLineSegment(sketch, "E2.187.1.0", {"start": v(-159.85, 31.48) * mm, "end": v(-159.85, 41.48) * mm});
            skLineSegment(sketch, "E2.188.1.0", {"start": v(-161.25, 79.46) * mm, "end": v(-161.25, 89.46) * mm});
            skLineSegment(sketch, "E2.189.1.0", {"start": v(-147.15, 7.5) * mm, "end": v(-147.15, 17.5) * mm});
            skLineSegment(sketch, "E2.190.1.0", {"start": v(-148.55, 55.47) * mm, "end": v(-148.55, 65.47) * mm});
            skLineSegment(sketch, "E2.191.1.0", {"start": v(-149.96, 103.45) * mm, "end": v(-149.96, 113.45) * mm});
            skLineSegment(sketch, "E2.192.1.0", {"start": v(-135.85, 31.48) * mm, "end": v(-135.85, 41.48) * mm});
            skLineSegment(sketch, "E2.193.1.0", {"start": v(-137.25, 79.46) * mm, "end": v(-137.25, 89.46) * mm});
            skLineSegment(sketch, "E2.194.1.0", {"start": v(-123.15, 7.5) * mm, "end": v(-123.15, 17.5) * mm});
            skLineSegment(sketch, "E2.195.1.0", {"start": v(-124.55, 55.47) * mm, "end": v(-124.55, 65.47) * mm});
            skLineSegment(sketch, "E2.196.1.0", {"start": v(-125.96, 103.45) * mm, "end": v(-125.96, 113.45) * mm});
            skLineSegment(sketch, "E2.197.1.0", {"start": v(-112.2, 43.48) * mm, "end": v(-112.2, 53.48) * mm});
            skLineSegment(sketch, "E2.198.1.0", {"start": v(-113.6, 91.46) * mm, "end": v(-113.6, 101.46) * mm});
            skLineSegment(sketch, "E2.199.1.0", {"start": v(-100.9, 67.47) * mm, "end": v(-100.9, 77.47) * mm});
            skLineSegment(sketch, "E2.200.1.0", {"start": v(-219.25, 89.46) * mm, "end": v(-209.25, 89.46) * mm});
            skLineSegment(sketch, "E2.201.1.0", {"start": v(-206.2, 53.48) * mm, "end": v(-196.2, 53.48) * mm});
            skLineSegment(sketch, "E2.202.1.0", {"start": v(-207.6, 101.46) * mm, "end": v(-197.6, 101.46) * mm});
            skLineSegment(sketch, "E2.203.1.0", {"start": v(-193.85, 41.48) * mm, "end": v(-183.85, 41.48) * mm});
            skLineSegment(sketch, "E2.204.1.0", {"start": v(-195.25, 89.46) * mm, "end": v(-185.25, 89.46) * mm});
            skLineSegment(sketch, "E2.205.1.0", {"start": v(-181.15, 17.5) * mm, "end": v(-171.15, 17.5) * mm});
            skLineSegment(sketch, "E2.206.1.0", {"start": v(-182.55, 65.47) * mm, "end": v(-172.55, 65.47) * mm});
            skLineSegment(sketch, "E2.207.1.0", {"start": v(-183.96, 113.45) * mm, "end": v(-173.96, 113.45) * mm});
            skLineSegment(sketch, "E2.208.1.0", {"start": v(-169.85, 41.48) * mm, "end": v(-159.85, 41.48) * mm});
            skLineSegment(sketch, "E2.209.1.0", {"start": v(-171.25, 89.46) * mm, "end": v(-161.25, 89.46) * mm});
            skLineSegment(sketch, "E2.210.1.0", {"start": v(-157.15, 17.5) * mm, "end": v(-147.15, 17.5) * mm});
            skLineSegment(sketch, "E2.211.1.0", {"start": v(-158.55, 65.47) * mm, "end": v(-148.55, 65.47) * mm});
            skLineSegment(sketch, "E2.212.1.0", {"start": v(-159.96, 113.45) * mm, "end": v(-149.96, 113.45) * mm});
            skLineSegment(sketch, "E2.213.1.0", {"start": v(-145.85, 41.48) * mm, "end": v(-135.85, 41.48) * mm});
            skLineSegment(sketch, "E2.214.1.0", {"start": v(-147.25, 89.46) * mm, "end": v(-137.25, 89.46) * mm});
            skLineSegment(sketch, "E2.215.1.0", {"start": v(-133.15, 17.5) * mm, "end": v(-123.15, 17.5) * mm});
            skLineSegment(sketch, "E2.216.1.0", {"start": v(-134.55, 65.47) * mm, "end": v(-124.55, 65.47) * mm});
            skLineSegment(sketch, "E2.217.1.0", {"start": v(-135.96, 113.45) * mm, "end": v(-125.96, 113.45) * mm});
            skLineSegment(sketch, "E2.218.1.0", {"start": v(-122.2, 53.48) * mm, "end": v(-112.2, 53.48) * mm});
            skLineSegment(sketch, "E2.219.1.0", {"start": v(-123.6, 101.46) * mm, "end": v(-113.6, 101.46) * mm});
            skLineSegment(sketch, "E2.220.1.0", {"start": v(-110.9, 77.47) * mm, "end": v(-100.9, 77.47) * mm});
            skLineSegment(sketch, "E2.221.1.0", {"start": v(-219.25, 79.46) * mm, "end": v(-219.25, 89.46) * mm});
            skLineSegment(sketch, "E2.222.1.0", {"start": v(-206.2, 43.48) * mm, "end": v(-206.2, 53.48) * mm});
            skLineSegment(sketch, "E2.223.1.0", {"start": v(-207.6, 91.46) * mm, "end": v(-207.6, 101.46) * mm});
            skLineSegment(sketch, "E2.224.1.0", {"start": v(-193.85, 31.48) * mm, "end": v(-193.85, 41.48) * mm});
            skLineSegment(sketch, "E2.225.1.0", {"start": v(-195.25, 79.46) * mm, "end": v(-195.25, 89.46) * mm});
            skLineSegment(sketch, "E2.226.1.0", {"start": v(-181.15, 7.5) * mm, "end": v(-181.15, 17.5) * mm});
            skLineSegment(sketch, "E2.227.1.0", {"start": v(-182.55, 55.47) * mm, "end": v(-182.55, 65.47) * mm});
            skLineSegment(sketch, "E2.228.1.0", {"start": v(-183.96, 103.45) * mm, "end": v(-183.96, 113.45) * mm});
            skLineSegment(sketch, "E2.229.1.0", {"start": v(-169.85, 31.48) * mm, "end": v(-169.85, 41.48) * mm});
            skLineSegment(sketch, "E2.230.1.0", {"start": v(-171.25, 79.46) * mm, "end": v(-171.25, 89.46) * mm});
            skLineSegment(sketch, "E2.231.1.0", {"start": v(-157.15, 7.5) * mm, "end": v(-157.15, 17.5) * mm});
            skLineSegment(sketch, "E2.232.1.0", {"start": v(-158.55, 55.47) * mm, "end": v(-158.55, 65.47) * mm});
            skLineSegment(sketch, "E2.233.1.0", {"start": v(-159.96, 103.45) * mm, "end": v(-159.96, 113.45) * mm});
            skLineSegment(sketch, "E2.234.1.0", {"start": v(-145.85, 31.48) * mm, "end": v(-145.85, 41.48) * mm});
            skLineSegment(sketch, "E2.235.1.0", {"start": v(-147.25, 79.46) * mm, "end": v(-147.25, 89.46) * mm});
            skLineSegment(sketch, "E2.236.1.0", {"start": v(-133.15, 7.5) * mm, "end": v(-133.15, 17.5) * mm});
            skLineSegment(sketch, "E2.237.1.0", {"start": v(-134.55, 55.47) * mm, "end": v(-134.55, 65.47) * mm});
            skLineSegment(sketch, "E2.238.1.0", {"start": v(-135.96, 103.45) * mm, "end": v(-135.96, 113.45) * mm});
            skLineSegment(sketch, "E2.239.1.0", {"start": v(-122.2, 43.48) * mm, "end": v(-122.2, 53.48) * mm});
            skLineSegment(sketch, "E2.240.1.0", {"start": v(-123.6, 91.46) * mm, "end": v(-123.6, 101.46) * mm});
            skLineSegment(sketch, "E2.241.1.0", {"start": v(-110.9, 67.47) * mm, "end": v(-110.9, 77.47) * mm});
            skLineSegment(sketch, "E2.242.1.0", {"start": v(-205.15, 7.5) * mm, "end": v(-195.15, 7.5) * mm});
            skLineSegment(sketch, "E2.243.1.0", {"start": v(-206.55, 55.47) * mm, "end": v(-196.55, 55.47) * mm});
            skLineSegment(sketch, "E2.244.1.0", {"start": v(-192.8, -4.5) * mm, "end": v(-182.8, -4.5) * mm});
            skLineSegment(sketch, "E2.245.1.0", {"start": v(-194.2, 43.48) * mm, "end": v(-184.2, 43.48) * mm});
            skLineSegment(sketch, "E2.246.1.0", {"start": v(-195.6, 91.46) * mm, "end": v(-185.6, 91.46) * mm});
            skLineSegment(sketch, "E2.247.1.0", {"start": v(-181.5, 19.49) * mm, "end": v(-171.5, 19.49) * mm});
            skLineSegment(sketch, "E2.248.1.0", {"start": v(-182.9, 67.47) * mm, "end": v(-172.9, 67.47) * mm});
            skLineSegment(sketch, "E2.249.1.0", {"start": v(-168.8, -4.5) * mm, "end": v(-158.8, -4.5) * mm});
            skLineSegment(sketch, "E2.250.1.0", {"start": v(-170.2, 43.48) * mm, "end": v(-160.2, 43.48) * mm});
            skLineSegment(sketch, "E2.251.1.0", {"start": v(-171.6, 91.46) * mm, "end": v(-161.6, 91.46) * mm});
            skLineSegment(sketch, "E2.252.1.0", {"start": v(-157.5, 19.49) * mm, "end": v(-147.5, 19.49) * mm});
            skLineSegment(sketch, "E2.253.1.0", {"start": v(-158.9, 67.47) * mm, "end": v(-148.9, 67.47) * mm});
            skLineSegment(sketch, "E2.254.1.0", {"start": v(-144.8, -4.5) * mm, "end": v(-134.8, -4.5) * mm});
            skLineSegment(sketch, "E2.255.1.0", {"start": v(-146.2, 43.48) * mm, "end": v(-136.2, 43.48) * mm});
            skLineSegment(sketch, "E2.256.1.0", {"start": v(-147.6, 91.46) * mm, "end": v(-137.6, 91.46) * mm});
            skLineSegment(sketch, "E2.257.1.0", {"start": v(-133.5, 19.49) * mm, "end": v(-123.5, 19.49) * mm});
            skLineSegment(sketch, "E2.258.1.0", {"start": v(-134.9, 67.47) * mm, "end": v(-124.9, 67.47) * mm});
            skLineSegment(sketch, "E2.259.1.0", {"start": v(-121.15, 7.5) * mm, "end": v(-111.15, 7.5) * mm});
            skLineSegment(sketch, "E2.260.1.0", {"start": v(-122.55, 55.47) * mm, "end": v(-112.55, 55.47) * mm});
            skLineSegment(sketch, "E2.261.1.0", {"start": v(-109.85, 31.48) * mm, "end": v(-99.85, 31.48) * mm});
            skLineSegment(sketch, "E2.262.1.0", {"start": v(-111.25, 79.46) * mm, "end": v(-101.25, 79.46) * mm});
            skLineSegment(sketch, "E2.263.1.0", {"start": v(-195.15, 7.5) * mm, "end": v(-195.15, 17.5) * mm});
            skLineSegment(sketch, "E2.264.1.0", {"start": v(-196.55, 55.47) * mm, "end": v(-196.55, 65.47) * mm});
            skLineSegment(sketch, "E2.265.1.0", {"start": v(-182.8, -4.5) * mm, "end": v(-182.8, 5.5) * mm});
            skLineSegment(sketch, "E2.266.1.0", {"start": v(-184.2, 43.48) * mm, "end": v(-184.2, 53.48) * mm});
            skLineSegment(sketch, "E2.267.1.0", {"start": v(-185.6, 91.46) * mm, "end": v(-185.6, 101.46) * mm});
            skLineSegment(sketch, "E2.268.1.0", {"start": v(-171.5, 19.49) * mm, "end": v(-171.5, 29.49) * mm});
            skLineSegment(sketch, "E2.269.1.0", {"start": v(-172.9, 67.47) * mm, "end": v(-172.9, 77.47) * mm});
            skLineSegment(sketch, "E2.270.1.0", {"start": v(-158.8, -4.5) * mm, "end": v(-158.8, 5.5) * mm});
            skLineSegment(sketch, "E2.271.1.0", {"start": v(-160.2, 43.48) * mm, "end": v(-160.2, 53.48) * mm});
            skLineSegment(sketch, "E2.272.1.0", {"start": v(-161.6, 91.46) * mm, "end": v(-161.6, 101.46) * mm});
            skLineSegment(sketch, "E2.273.1.0", {"start": v(-147.5, 19.49) * mm, "end": v(-147.5, 29.49) * mm});
            skLineSegment(sketch, "E2.274.1.0", {"start": v(-148.9, 67.47) * mm, "end": v(-148.9, 77.47) * mm});
            skLineSegment(sketch, "E2.275.1.0", {"start": v(-134.8, -4.5) * mm, "end": v(-134.8, 5.5) * mm});
            skLineSegment(sketch, "E2.276.1.0", {"start": v(-136.2, 43.48) * mm, "end": v(-136.2, 53.48) * mm});
            skLineSegment(sketch, "E2.277.1.0", {"start": v(-137.6, 91.46) * mm, "end": v(-137.6, 101.46) * mm});
            skLineSegment(sketch, "E2.278.1.0", {"start": v(-123.5, 19.49) * mm, "end": v(-123.5, 29.49) * mm});
            skLineSegment(sketch, "E2.279.1.0", {"start": v(-124.9, 67.47) * mm, "end": v(-124.9, 77.47) * mm});
            skLineSegment(sketch, "E2.280.1.0", {"start": v(-111.15, 7.5) * mm, "end": v(-111.15, 17.5) * mm});
            skLineSegment(sketch, "E2.281.1.0", {"start": v(-112.55, 55.47) * mm, "end": v(-112.55, 65.47) * mm});
            skLineSegment(sketch, "E2.282.1.0", {"start": v(-99.85, 31.48) * mm, "end": v(-99.85, 41.48) * mm});
            skLineSegment(sketch, "E2.283.1.0", {"start": v(-101.25, 79.46) * mm, "end": v(-101.25, 89.46) * mm});
            skLineSegment(sketch, "E2.284.1.0", {"start": v(-205.15, 17.5) * mm, "end": v(-195.15, 17.5) * mm});
            skLineSegment(sketch, "E2.285.1.0", {"start": v(-206.55, 65.47) * mm, "end": v(-196.55, 65.47) * mm});
            skLineSegment(sketch, "E2.286.1.0", {"start": v(-192.8, 5.5) * mm, "end": v(-182.8, 5.5) * mm});
            skLineSegment(sketch, "E2.287.1.0", {"start": v(-194.2, 53.48) * mm, "end": v(-184.2, 53.48) * mm});
            skLineSegment(sketch, "E2.288.1.0", {"start": v(-195.6, 101.46) * mm, "end": v(-185.6, 101.46) * mm});
            skLineSegment(sketch, "E2.289.1.0", {"start": v(-181.5, 29.49) * mm, "end": v(-171.5, 29.49) * mm});
            skLineSegment(sketch, "E2.290.1.0", {"start": v(-182.9, 77.47) * mm, "end": v(-172.9, 77.47) * mm});
            skLineSegment(sketch, "E2.291.1.0", {"start": v(-168.8, 5.5) * mm, "end": v(-158.8, 5.5) * mm});
            skLineSegment(sketch, "E2.292.1.0", {"start": v(-170.2, 53.48) * mm, "end": v(-160.2, 53.48) * mm});
            skLineSegment(sketch, "E2.293.1.0", {"start": v(-171.6, 101.46) * mm, "end": v(-161.6, 101.46) * mm});
            skLineSegment(sketch, "E2.294.1.0", {"start": v(-157.5, 29.49) * mm, "end": v(-147.5, 29.49) * mm});
            skLineSegment(sketch, "E2.295.1.0", {"start": v(-158.9, 77.47) * mm, "end": v(-148.9, 77.47) * mm});
            skLineSegment(sketch, "E2.296.1.0", {"start": v(-144.8, 5.5) * mm, "end": v(-134.8, 5.5) * mm});
            skLineSegment(sketch, "E2.297.1.0", {"start": v(-146.2, 53.48) * mm, "end": v(-136.2, 53.48) * mm});
            skLineSegment(sketch, "E2.298.1.0", {"start": v(-147.6, 101.46) * mm, "end": v(-137.6, 101.46) * mm});
            skLineSegment(sketch, "E2.299.1.0", {"start": v(-133.5, 29.49) * mm, "end": v(-123.5, 29.49) * mm});
            skLineSegment(sketch, "E2.300.1.0", {"start": v(-134.9, 77.47) * mm, "end": v(-124.9, 77.47) * mm});
            skLineSegment(sketch, "E2.301.1.0", {"start": v(-121.15, 17.5) * mm, "end": v(-111.15, 17.5) * mm});
            skLineSegment(sketch, "E2.302.1.0", {"start": v(-122.55, 65.47) * mm, "end": v(-112.55, 65.47) * mm});
            skLineSegment(sketch, "E2.303.1.0", {"start": v(-109.85, 41.48) * mm, "end": v(-99.85, 41.48) * mm});
            skLineSegment(sketch, "E2.304.1.0", {"start": v(-111.25, 89.46) * mm, "end": v(-101.25, 89.46) * mm});
            skLineSegment(sketch, "E2.305.1.0", {"start": v(-205.15, 7.5) * mm, "end": v(-205.15, 17.5) * mm});
            skLineSegment(sketch, "E2.306.1.0", {"start": v(-206.55, 55.47) * mm, "end": v(-206.55, 65.47) * mm});
            skLineSegment(sketch, "E2.307.1.0", {"start": v(-192.8, -4.5) * mm, "end": v(-192.8, 5.5) * mm});
            skLineSegment(sketch, "E2.308.1.0", {"start": v(-194.2, 43.48) * mm, "end": v(-194.2, 53.48) * mm});
            skLineSegment(sketch, "E2.309.1.0", {"start": v(-195.6, 91.46) * mm, "end": v(-195.6, 101.46) * mm});
            skLineSegment(sketch, "E2.310.1.0", {"start": v(-181.5, 19.49) * mm, "end": v(-181.5, 29.49) * mm});
            skLineSegment(sketch, "E2.311.1.0", {"start": v(-182.9, 67.47) * mm, "end": v(-182.9, 77.47) * mm});
            skLineSegment(sketch, "E2.312.1.0", {"start": v(-168.8, -4.5) * mm, "end": v(-168.8, 5.5) * mm});
            skLineSegment(sketch, "E2.313.1.0", {"start": v(-170.2, 43.48) * mm, "end": v(-170.2, 53.48) * mm});
            skLineSegment(sketch, "E2.314.1.0", {"start": v(-171.6, 91.46) * mm, "end": v(-171.6, 101.46) * mm});
            skLineSegment(sketch, "E2.315.1.0", {"start": v(-157.5, 19.49) * mm, "end": v(-157.5, 29.49) * mm});
            skLineSegment(sketch, "E2.316.1.0", {"start": v(-158.9, 67.47) * mm, "end": v(-158.9, 77.47) * mm});
            skLineSegment(sketch, "E2.317.1.0", {"start": v(-144.8, -4.5) * mm, "end": v(-144.8, 5.5) * mm});
            skLineSegment(sketch, "E2.318.1.0", {"start": v(-146.2, 43.48) * mm, "end": v(-146.2, 53.48) * mm});
            skLineSegment(sketch, "E2.319.1.0", {"start": v(-147.6, 91.46) * mm, "end": v(-147.6, 101.46) * mm});
            skLineSegment(sketch, "E2.320.1.0", {"start": v(-133.5, 19.49) * mm, "end": v(-133.5, 29.49) * mm});
            skLineSegment(sketch, "E2.321.1.0", {"start": v(-134.9, 67.47) * mm, "end": v(-134.9, 77.47) * mm});
            skLineSegment(sketch, "E2.322.1.0", {"start": v(-121.15, 7.5) * mm, "end": v(-121.15, 17.5) * mm});
            skLineSegment(sketch, "E2.323.1.0", {"start": v(-122.55, 55.47) * mm, "end": v(-122.55, 65.47) * mm});
            skLineSegment(sketch, "E2.324.1.0", {"start": v(-109.85, 31.48) * mm, "end": v(-109.85, 41.48) * mm});
            skLineSegment(sketch, "E2.325.1.0", {"start": v(-111.25, 79.46) * mm, "end": v(-111.25, 89.46) * mm});
            skLineSegment(sketch, "E2.326.1.0", {"start": v(-205.5, 19.49) * mm, "end": v(-195.5, 19.49) * mm});
            skLineSegment(sketch, "E2.327.1.0", {"start": v(-206.9, 67.47) * mm, "end": v(-196.9, 67.47) * mm});
            skLineSegment(sketch, "E2.328.1.0", {"start": v(-193.15, 7.5) * mm, "end": v(-183.15, 7.5) * mm});
            skLineSegment(sketch, "E2.329.1.0", {"start": v(-194.55, 55.47) * mm, "end": v(-184.55, 55.47) * mm});
            skLineSegment(sketch, "E2.330.1.0", {"start": v(-195.96, 103.45) * mm, "end": v(-185.96, 103.45) * mm});
            skLineSegment(sketch, "E2.331.1.0", {"start": v(-181.85, 31.48) * mm, "end": v(-171.85, 31.48) * mm});
            skLineSegment(sketch, "E2.332.1.0", {"start": v(-183.25, 79.46) * mm, "end": v(-173.25, 79.46) * mm});
            skLineSegment(sketch, "E2.333.1.0", {"start": v(-169.15, 7.5) * mm, "end": v(-159.15, 7.5) * mm});
            skLineSegment(sketch, "E2.334.1.0", {"start": v(-170.55, 55.47) * mm, "end": v(-160.55, 55.47) * mm});
            skLineSegment(sketch, "E2.335.1.0", {"start": v(-171.96, 103.45) * mm, "end": v(-161.96, 103.45) * mm});
            skLineSegment(sketch, "E2.336.1.0", {"start": v(-157.85, 31.48) * mm, "end": v(-147.85, 31.48) * mm});
            skLineSegment(sketch, "E2.337.1.0", {"start": v(-159.25, 79.46) * mm, "end": v(-149.25, 79.46) * mm});
            skLineSegment(sketch, "E2.338.1.0", {"start": v(-145.15, 7.5) * mm, "end": v(-135.15, 7.5) * mm});
            skLineSegment(sketch, "E2.339.1.0", {"start": v(-146.55, 55.47) * mm, "end": v(-136.55, 55.47) * mm});
            skLineSegment(sketch, "E2.340.1.0", {"start": v(-147.96, 103.45) * mm, "end": v(-137.96, 103.45) * mm});
            skLineSegment(sketch, "E2.341.1.0", {"start": v(-133.85, 31.48) * mm, "end": v(-123.85, 31.48) * mm});
            skLineSegment(sketch, "E2.342.1.0", {"start": v(-135.25, 79.46) * mm, "end": v(-125.25, 79.46) * mm});
            skLineSegment(sketch, "E2.343.1.0", {"start": v(-121.5, 19.49) * mm, "end": v(-111.5, 19.49) * mm});
            skLineSegment(sketch, "E2.344.1.0", {"start": v(-122.9, 67.47) * mm, "end": v(-112.9, 67.47) * mm});
            skLineSegment(sketch, "E2.345.1.0", {"start": v(-110.2, 43.48) * mm, "end": v(-100.2, 43.48) * mm});
            skLineSegment(sketch, "E2.346.1.0", {"start": v(-133.85, 41.48) * mm, "end": v(-123.85, 41.48) * mm});
            skLineSegment(sketch, "E2.347.1.0", {"start": v(-134.2, 43.48) * mm, "end": v(-124.2, 43.48) * mm});
            skLineSegment(sketch, "E2.0.1.1", {"start": v(-218.55, 179.47) * mm, "end": v(-218.55, 189.47) * mm});
            skLineSegment(sketch, "E2.1.1.1", {"start": v(-208.55, 179.47) * mm, "end": v(-208.55, 189.47) * mm});
            skLineSegment(sketch, "E2.2.1.1", {"start": v(-218.55, 189.47) * mm, "end": v(-208.55, 189.47) * mm});
            skLineSegment(sketch, "E2.3.1.1", {"start": v(-217.5, 143.49) * mm, "end": v(-207.5, 143.49) * mm});
            skLineSegment(sketch, "E2.4.1.1", {"start": v(-207.5, 143.49) * mm, "end": v(-207.5, 153.49) * mm});
            skLineSegment(sketch, "E2.5.1.1", {"start": v(-217.5, 153.49) * mm, "end": v(-207.5, 153.49) * mm});
            skLineSegment(sketch, "E2.6.1.1", {"start": v(-217.5, 143.49) * mm, "end": v(-217.5, 153.49) * mm});
            skLineSegment(sketch, "E2.7.1.1", {"start": v(-217.85, 155.48) * mm, "end": v(-207.85, 155.48) * mm});
            skLineSegment(sketch, "E2.8.1.1", {"start": v(-207.85, 155.48) * mm, "end": v(-207.85, 165.48) * mm});
            skLineSegment(sketch, "E2.9.1.1", {"start": v(-217.85, 165.48) * mm, "end": v(-207.85, 165.48) * mm});
            skLineSegment(sketch, "E2.10.1.1", {"start": v(-217.85, 155.48) * mm, "end": v(-217.85, 165.48) * mm});
            skLineSegment(sketch, "E2.11.1.1", {"start": v(-218.2, 167.48) * mm, "end": v(-208.2, 167.48) * mm});
            skLineSegment(sketch, "E2.12.1.1", {"start": v(-208.2, 167.48) * mm, "end": v(-208.2, 177.48) * mm});
            skLineSegment(sketch, "E2.13.1.1", {"start": v(-218.2, 177.48) * mm, "end": v(-208.2, 177.48) * mm});
            skLineSegment(sketch, "E2.14.1.1", {"start": v(-218.2, 167.48) * mm, "end": v(-218.2, 177.48) * mm});
            skLineSegment(sketch, "E2.15.1.1", {"start": v(-218.55, 179.47) * mm, "end": v(-208.55, 179.47) * mm});
            skLineSegment(sketch, "E2.16.1.1", {"start": v(-205.5, 143.49) * mm, "end": v(-205.5, 153.49) * mm});
            skLineSegment(sketch, "E2.17.1.1", {"start": v(-206.9, 191.47) * mm, "end": v(-206.9, 201.47) * mm});
            skLineSegment(sketch, "E2.18.1.1", {"start": v(-193.15, 131.5) * mm, "end": v(-193.15, 141.5) * mm});
            skLineSegment(sketch, "E2.19.1.1", {"start": v(-194.55, 179.47) * mm, "end": v(-194.55, 189.47) * mm});
            skLineSegment(sketch, "E2.20.1.1", {"start": v(-195.96, 227.45) * mm, "end": v(-195.96, 237.45) * mm});
            skLineSegment(sketch, "E2.21.1.1", {"start": v(-181.85, 155.48) * mm, "end": v(-181.85, 165.48) * mm});
            skLineSegment(sketch, "E2.22.1.1", {"start": v(-183.25, 203.46) * mm, "end": v(-183.25, 213.46) * mm});
            skLineSegment(sketch, "E2.23.1.1", {"start": v(-169.15, 131.5) * mm, "end": v(-169.15, 141.5) * mm});
            skLineSegment(sketch, "E2.24.1.1", {"start": v(-170.55, 179.47) * mm, "end": v(-170.55, 189.47) * mm});
            skLineSegment(sketch, "E2.25.1.1", {"start": v(-171.96, 227.45) * mm, "end": v(-171.96, 237.45) * mm});
            skLineSegment(sketch, "E2.26.1.1", {"start": v(-157.85, 155.48) * mm, "end": v(-157.85, 165.48) * mm});
            skLineSegment(sketch, "E2.27.1.1", {"start": v(-159.25, 203.46) * mm, "end": v(-159.25, 213.46) * mm});
            skLineSegment(sketch, "E2.28.1.1", {"start": v(-145.15, 131.5) * mm, "end": v(-145.15, 141.5) * mm});
            skLineSegment(sketch, "E2.29.1.1", {"start": v(-146.55, 179.47) * mm, "end": v(-146.55, 189.47) * mm});
            skLineSegment(sketch, "E2.30.1.1", {"start": v(-147.96, 227.45) * mm, "end": v(-147.96, 237.45) * mm});
            skLineSegment(sketch, "E2.31.1.1", {"start": v(-133.85, 155.48) * mm, "end": v(-133.85, 165.48) * mm});
            skLineSegment(sketch, "E2.32.1.1", {"start": v(-135.25, 203.46) * mm, "end": v(-135.25, 213.46) * mm});
            skLineSegment(sketch, "E2.33.1.1", {"start": v(-121.5, 143.49) * mm, "end": v(-121.5, 153.49) * mm});
            skLineSegment(sketch, "E2.34.1.1", {"start": v(-122.9, 191.47) * mm, "end": v(-122.9, 201.47) * mm});
            skLineSegment(sketch, "E2.35.1.1", {"start": v(-110.2, 167.48) * mm, "end": v(-110.2, 177.48) * mm});
            skLineSegment(sketch, "E2.36.1.1", {"start": v(-195.5, 143.49) * mm, "end": v(-195.5, 153.49) * mm});
            skLineSegment(sketch, "E2.37.1.1", {"start": v(-196.9, 191.47) * mm, "end": v(-196.9, 201.47) * mm});
            skLineSegment(sketch, "E2.38.1.1", {"start": v(-183.15, 131.5) * mm, "end": v(-183.15, 141.5) * mm});
            skLineSegment(sketch, "E2.39.1.1", {"start": v(-184.55, 179.47) * mm, "end": v(-184.55, 189.47) * mm});
            skLineSegment(sketch, "E2.40.1.1", {"start": v(-185.96, 227.45) * mm, "end": v(-185.96, 237.45) * mm});
            skLineSegment(sketch, "E2.41.1.1", {"start": v(-171.85, 155.48) * mm, "end": v(-171.85, 165.48) * mm});
            skLineSegment(sketch, "E2.42.1.1", {"start": v(-173.25, 203.46) * mm, "end": v(-173.25, 213.46) * mm});
            skLineSegment(sketch, "E2.43.1.1", {"start": v(-159.15, 131.5) * mm, "end": v(-159.15, 141.5) * mm});
            skLineSegment(sketch, "E2.44.1.1", {"start": v(-160.55, 179.47) * mm, "end": v(-160.55, 189.47) * mm});
            skLineSegment(sketch, "E2.45.1.1", {"start": v(-161.96, 227.45) * mm, "end": v(-161.96, 237.45) * mm});
            skLineSegment(sketch, "E2.46.1.1", {"start": v(-147.85, 155.48) * mm, "end": v(-147.85, 165.48) * mm});
            skLineSegment(sketch, "E2.47.1.1", {"start": v(-149.25, 203.46) * mm, "end": v(-149.25, 213.46) * mm});
            skLineSegment(sketch, "E2.48.1.1", {"start": v(-135.15, 131.5) * mm, "end": v(-135.15, 141.5) * mm});
            skLineSegment(sketch, "E2.49.1.1", {"start": v(-136.55, 179.47) * mm, "end": v(-136.55, 189.47) * mm});
            skLineSegment(sketch, "E2.50.1.1", {"start": v(-137.96, 227.45) * mm, "end": v(-137.96, 237.45) * mm});
            skLineSegment(sketch, "E2.51.1.1", {"start": v(-123.85, 155.48) * mm, "end": v(-123.85, 165.48) * mm});
            skLineSegment(sketch, "E2.52.1.1", {"start": v(-125.25, 203.46) * mm, "end": v(-125.25, 213.46) * mm});
            skLineSegment(sketch, "E2.53.1.1", {"start": v(-111.5, 143.49) * mm, "end": v(-111.5, 153.49) * mm});
            skLineSegment(sketch, "E2.54.1.1", {"start": v(-112.9, 191.47) * mm, "end": v(-112.9, 201.47) * mm});
            skLineSegment(sketch, "E2.55.1.1", {"start": v(-100.2, 167.48) * mm, "end": v(-100.2, 177.48) * mm});
            skLineSegment(sketch, "E2.56.1.1", {"start": v(-205.5, 153.49) * mm, "end": v(-195.5, 153.49) * mm});
            skLineSegment(sketch, "E2.57.1.1", {"start": v(-206.9, 201.47) * mm, "end": v(-196.9, 201.47) * mm});
            skLineSegment(sketch, "E2.58.1.1", {"start": v(-193.15, 141.5) * mm, "end": v(-183.15, 141.5) * mm});
            skLineSegment(sketch, "E2.59.1.1", {"start": v(-194.55, 189.47) * mm, "end": v(-184.55, 189.47) * mm});
            skLineSegment(sketch, "E2.60.1.1", {"start": v(-195.96, 237.45) * mm, "end": v(-185.96, 237.45) * mm});
            skLineSegment(sketch, "E2.61.1.1", {"start": v(-181.85, 165.48) * mm, "end": v(-171.85, 165.48) * mm});
            skLineSegment(sketch, "E2.62.1.1", {"start": v(-183.25, 213.46) * mm, "end": v(-173.25, 213.46) * mm});
            skLineSegment(sketch, "E2.63.1.1", {"start": v(-169.15, 141.5) * mm, "end": v(-159.15, 141.5) * mm});
            skLineSegment(sketch, "E2.64.1.1", {"start": v(-170.55, 189.47) * mm, "end": v(-160.55, 189.47) * mm});
            skLineSegment(sketch, "E2.65.1.1", {"start": v(-171.96, 237.45) * mm, "end": v(-161.96, 237.45) * mm});
            skLineSegment(sketch, "E2.66.1.1", {"start": v(-157.85, 165.48) * mm, "end": v(-147.85, 165.48) * mm});
            skLineSegment(sketch, "E2.67.1.1", {"start": v(-159.25, 213.46) * mm, "end": v(-149.25, 213.46) * mm});
            skLineSegment(sketch, "E2.68.1.1", {"start": v(-145.15, 141.5) * mm, "end": v(-135.15, 141.5) * mm});
            skLineSegment(sketch, "E2.69.1.1", {"start": v(-146.55, 189.47) * mm, "end": v(-136.55, 189.47) * mm});
            skLineSegment(sketch, "E2.70.1.1", {"start": v(-147.96, 237.45) * mm, "end": v(-137.96, 237.45) * mm});
            skLineSegment(sketch, "E2.71.1.1", {"start": v(-135.25, 213.46) * mm, "end": v(-125.25, 213.46) * mm});
            skLineSegment(sketch, "E2.72.1.1", {"start": v(-121.5, 153.49) * mm, "end": v(-111.5, 153.49) * mm});
            skLineSegment(sketch, "E2.73.1.1", {"start": v(-122.9, 201.47) * mm, "end": v(-112.9, 201.47) * mm});
            skLineSegment(sketch, "E2.74.1.1", {"start": v(-110.2, 177.48) * mm, "end": v(-100.2, 177.48) * mm});
            skLineSegment(sketch, "E2.75.1.1", {"start": v(-218.9, 191.47) * mm, "end": v(-208.9, 191.47) * mm});
            skLineSegment(sketch, "E2.76.1.1", {"start": v(-205.85, 155.48) * mm, "end": v(-195.85, 155.48) * mm});
            skLineSegment(sketch, "E2.77.1.1", {"start": v(-207.25, 203.46) * mm, "end": v(-197.25, 203.46) * mm});
            skLineSegment(sketch, "E2.78.1.1", {"start": v(-193.5, 143.49) * mm, "end": v(-183.5, 143.49) * mm});
            skLineSegment(sketch, "E2.79.1.1", {"start": v(-194.9, 191.47) * mm, "end": v(-184.9, 191.47) * mm});
            skLineSegment(sketch, "E2.80.1.1", {"start": v(-180.8, 119.5) * mm, "end": v(-170.8, 119.5) * mm});
            skLineSegment(sketch, "E2.81.1.1", {"start": v(-182.2, 167.48) * mm, "end": v(-172.2, 167.48) * mm});
            skLineSegment(sketch, "E2.82.1.1", {"start": v(-183.6, 215.46) * mm, "end": v(-173.6, 215.46) * mm});
            skLineSegment(sketch, "E2.83.1.1", {"start": v(-169.5, 143.49) * mm, "end": v(-159.5, 143.49) * mm});
            skLineSegment(sketch, "E2.84.1.1", {"start": v(-170.9, 191.47) * mm, "end": v(-160.9, 191.47) * mm});
            skLineSegment(sketch, "E2.85.1.1", {"start": v(-156.8, 119.5) * mm, "end": v(-146.8, 119.5) * mm});
            skLineSegment(sketch, "E2.86.1.1", {"start": v(-158.2, 167.48) * mm, "end": v(-148.2, 167.48) * mm});
            skLineSegment(sketch, "E2.87.1.1", {"start": v(-159.6, 215.46) * mm, "end": v(-149.6, 215.46) * mm});
            skLineSegment(sketch, "E2.88.1.1", {"start": v(-145.5, 143.49) * mm, "end": v(-135.5, 143.49) * mm});
            skLineSegment(sketch, "E2.89.1.1", {"start": v(-146.9, 191.47) * mm, "end": v(-136.9, 191.47) * mm});
            skLineSegment(sketch, "E2.90.1.1", {"start": v(-132.8, 119.5) * mm, "end": v(-122.8, 119.5) * mm});
            skLineSegment(sketch, "E2.91.1.1", {"start": v(-135.6, 215.46) * mm, "end": v(-125.6, 215.46) * mm});
            skLineSegment(sketch, "E2.92.1.1", {"start": v(-121.85, 155.48) * mm, "end": v(-111.85, 155.48) * mm});
            skLineSegment(sketch, "E2.93.1.1", {"start": v(-123.25, 203.46) * mm, "end": v(-113.25, 203.46) * mm});
            skLineSegment(sketch, "E2.94.1.1", {"start": v(-110.55, 179.47) * mm, "end": v(-100.55, 179.47) * mm});
            skLineSegment(sketch, "E2.95.1.1", {"start": v(-208.9, 191.47) * mm, "end": v(-208.9, 201.47) * mm});
            skLineSegment(sketch, "E2.96.1.1", {"start": v(-195.85, 155.48) * mm, "end": v(-195.85, 165.48) * mm});
            skLineSegment(sketch, "E2.97.1.1", {"start": v(-197.25, 203.46) * mm, "end": v(-197.25, 213.46) * mm});
            skLineSegment(sketch, "E2.98.1.1", {"start": v(-183.5, 143.49) * mm, "end": v(-183.5, 153.49) * mm});
            skLineSegment(sketch, "E2.99.1.1", {"start": v(-184.9, 191.47) * mm, "end": v(-184.9, 201.47) * mm});
            skLineSegment(sketch, "E2.100.1.1", {"start": v(-170.8, 119.5) * mm, "end": v(-170.8, 129.5) * mm});
            skLineSegment(sketch, "E2.101.1.1", {"start": v(-172.2, 167.48) * mm, "end": v(-172.2, 177.48) * mm});
            skLineSegment(sketch, "E2.102.1.1", {"start": v(-173.6, 215.46) * mm, "end": v(-173.6, 225.46) * mm});
            skLineSegment(sketch, "E2.103.1.1", {"start": v(-159.5, 143.49) * mm, "end": v(-159.5, 153.49) * mm});
            skLineSegment(sketch, "E2.104.1.1", {"start": v(-160.9, 191.47) * mm, "end": v(-160.9, 201.47) * mm});
            skLineSegment(sketch, "E2.105.1.1", {"start": v(-146.8, 119.5) * mm, "end": v(-146.8, 129.5) * mm});
            skLineSegment(sketch, "E2.106.1.1", {"start": v(-148.2, 167.48) * mm, "end": v(-148.2, 177.48) * mm});
            skLineSegment(sketch, "E2.107.1.1", {"start": v(-149.6, 215.46) * mm, "end": v(-149.6, 225.46) * mm});
            skLineSegment(sketch, "E2.108.1.1", {"start": v(-135.5, 143.49) * mm, "end": v(-135.5, 153.49) * mm});
            skLineSegment(sketch, "E2.109.1.1", {"start": v(-136.9, 191.47) * mm, "end": v(-136.9, 201.47) * mm});
            skLineSegment(sketch, "E2.110.1.1", {"start": v(-122.8, 119.5) * mm, "end": v(-122.8, 129.5) * mm});
            skLineSegment(sketch, "E2.111.1.1", {"start": v(-124.2, 167.48) * mm, "end": v(-124.2, 177.48) * mm});
            skLineSegment(sketch, "E2.112.1.1", {"start": v(-125.6, 215.46) * mm, "end": v(-125.6, 225.46) * mm});
            skLineSegment(sketch, "E2.113.1.1", {"start": v(-111.85, 155.48) * mm, "end": v(-111.85, 165.48) * mm});
            skLineSegment(sketch, "E2.114.1.1", {"start": v(-113.25, 203.46) * mm, "end": v(-113.25, 213.46) * mm});
            skLineSegment(sketch, "E2.115.1.1", {"start": v(-100.55, 179.47) * mm, "end": v(-100.55, 189.47) * mm});
            skLineSegment(sketch, "E2.116.1.1", {"start": v(-218.9, 201.47) * mm, "end": v(-208.9, 201.47) * mm});
            skLineSegment(sketch, "E2.117.1.1", {"start": v(-205.85, 165.48) * mm, "end": v(-195.85, 165.48) * mm});
            skLineSegment(sketch, "E2.118.1.1", {"start": v(-207.25, 213.46) * mm, "end": v(-197.25, 213.46) * mm});
            skLineSegment(sketch, "E2.119.1.1", {"start": v(-193.5, 153.49) * mm, "end": v(-183.5, 153.49) * mm});
            skLineSegment(sketch, "E2.120.1.1", {"start": v(-194.9, 201.47) * mm, "end": v(-184.9, 201.47) * mm});
            skLineSegment(sketch, "E2.121.1.1", {"start": v(-180.8, 129.5) * mm, "end": v(-170.8, 129.5) * mm});
            skLineSegment(sketch, "E2.122.1.1", {"start": v(-182.2, 177.48) * mm, "end": v(-172.2, 177.48) * mm});
            skLineSegment(sketch, "E2.123.1.1", {"start": v(-183.6, 225.46) * mm, "end": v(-173.6, 225.46) * mm});
            skLineSegment(sketch, "E2.124.1.1", {"start": v(-169.5, 153.49) * mm, "end": v(-159.5, 153.49) * mm});
            skLineSegment(sketch, "E2.125.1.1", {"start": v(-170.9, 201.47) * mm, "end": v(-160.9, 201.47) * mm});
            skLineSegment(sketch, "E2.126.1.1", {"start": v(-156.8, 129.5) * mm, "end": v(-146.8, 129.5) * mm});
            skLineSegment(sketch, "E2.127.1.1", {"start": v(-158.2, 177.48) * mm, "end": v(-148.2, 177.48) * mm});
            skLineSegment(sketch, "E2.128.1.1", {"start": v(-159.6, 225.46) * mm, "end": v(-149.6, 225.46) * mm});
            skLineSegment(sketch, "E2.129.1.1", {"start": v(-145.5, 153.49) * mm, "end": v(-135.5, 153.49) * mm});
            skLineSegment(sketch, "E2.130.1.1", {"start": v(-146.9, 201.47) * mm, "end": v(-136.9, 201.47) * mm});
            skLineSegment(sketch, "E2.131.1.1", {"start": v(-132.8, 129.5) * mm, "end": v(-122.8, 129.5) * mm});
            skLineSegment(sketch, "E2.132.1.1", {"start": v(-134.2, 177.48) * mm, "end": v(-124.2, 177.48) * mm});
            skLineSegment(sketch, "E2.133.1.1", {"start": v(-135.6, 225.46) * mm, "end": v(-125.6, 225.46) * mm});
            skLineSegment(sketch, "E2.134.1.1", {"start": v(-121.85, 165.48) * mm, "end": v(-111.85, 165.48) * mm});
            skLineSegment(sketch, "E2.135.1.1", {"start": v(-123.25, 213.46) * mm, "end": v(-113.25, 213.46) * mm});
            skLineSegment(sketch, "E2.136.1.1", {"start": v(-110.55, 189.47) * mm, "end": v(-100.55, 189.47) * mm});
            skLineSegment(sketch, "E2.137.1.1", {"start": v(-218.9, 191.47) * mm, "end": v(-218.9, 201.47) * mm});
            skLineSegment(sketch, "E2.138.1.1", {"start": v(-205.85, 155.48) * mm, "end": v(-205.85, 165.48) * mm});
            skLineSegment(sketch, "E2.139.1.1", {"start": v(-207.25, 203.46) * mm, "end": v(-207.25, 213.46) * mm});
            skLineSegment(sketch, "E2.140.1.1", {"start": v(-193.5, 143.49) * mm, "end": v(-193.5, 153.49) * mm});
            skLineSegment(sketch, "E2.141.1.1", {"start": v(-194.9, 191.47) * mm, "end": v(-194.9, 201.47) * mm});
            skLineSegment(sketch, "E2.142.1.1", {"start": v(-180.8, 119.5) * mm, "end": v(-180.8, 129.5) * mm});
            skLineSegment(sketch, "E2.143.1.1", {"start": v(-182.2, 167.48) * mm, "end": v(-182.2, 177.48) * mm});
            skLineSegment(sketch, "E2.144.1.1", {"start": v(-183.6, 215.46) * mm, "end": v(-183.6, 225.46) * mm});
            skLineSegment(sketch, "E2.145.1.1", {"start": v(-169.5, 143.49) * mm, "end": v(-169.5, 153.49) * mm});
            skLineSegment(sketch, "E2.146.1.1", {"start": v(-170.9, 191.47) * mm, "end": v(-170.9, 201.47) * mm});
            skLineSegment(sketch, "E2.147.1.1", {"start": v(-156.8, 119.5) * mm, "end": v(-156.8, 129.5) * mm});
            skLineSegment(sketch, "E2.148.1.1", {"start": v(-158.2, 167.48) * mm, "end": v(-158.2, 177.48) * mm});
            skLineSegment(sketch, "E2.149.1.1", {"start": v(-159.6, 215.46) * mm, "end": v(-159.6, 225.46) * mm});
            skLineSegment(sketch, "E2.150.1.1", {"start": v(-145.5, 143.49) * mm, "end": v(-145.5, 153.49) * mm});
            skLineSegment(sketch, "E2.151.1.1", {"start": v(-146.9, 191.47) * mm, "end": v(-146.9, 201.47) * mm});
            skLineSegment(sketch, "E2.152.1.1", {"start": v(-132.8, 119.5) * mm, "end": v(-132.8, 129.5) * mm});
            skLineSegment(sketch, "E2.153.1.1", {"start": v(-134.2, 167.48) * mm, "end": v(-134.2, 177.48) * mm});
            skLineSegment(sketch, "E2.154.1.1", {"start": v(-135.6, 215.46) * mm, "end": v(-135.6, 225.46) * mm});
            skLineSegment(sketch, "E2.155.1.1", {"start": v(-121.85, 155.48) * mm, "end": v(-121.85, 165.48) * mm});
            skLineSegment(sketch, "E2.156.1.1", {"start": v(-123.25, 203.46) * mm, "end": v(-123.25, 213.46) * mm});
            skLineSegment(sketch, "E2.157.1.1", {"start": v(-110.55, 179.47) * mm, "end": v(-110.55, 189.47) * mm});
            skLineSegment(sketch, "E2.158.1.1", {"start": v(-219.25, 203.46) * mm, "end": v(-209.25, 203.46) * mm});
            skLineSegment(sketch, "E2.159.1.1", {"start": v(-206.2, 167.48) * mm, "end": v(-196.2, 167.48) * mm});
            skLineSegment(sketch, "E2.160.1.1", {"start": v(-207.6, 215.46) * mm, "end": v(-197.6, 215.46) * mm});
            skLineSegment(sketch, "E2.161.1.1", {"start": v(-193.85, 155.48) * mm, "end": v(-183.85, 155.48) * mm});
            skLineSegment(sketch, "E2.162.1.1", {"start": v(-195.25, 203.46) * mm, "end": v(-185.25, 203.46) * mm});
            skLineSegment(sketch, "E2.163.1.1", {"start": v(-181.15, 131.5) * mm, "end": v(-171.15, 131.5) * mm});
            skLineSegment(sketch, "E2.164.1.1", {"start": v(-182.55, 179.47) * mm, "end": v(-172.55, 179.47) * mm});
            skLineSegment(sketch, "E2.165.1.1", {"start": v(-183.96, 227.45) * mm, "end": v(-173.96, 227.45) * mm});
            skLineSegment(sketch, "E2.166.1.1", {"start": v(-169.85, 155.48) * mm, "end": v(-159.85, 155.48) * mm});
            skLineSegment(sketch, "E2.167.1.1", {"start": v(-171.25, 203.46) * mm, "end": v(-161.25, 203.46) * mm});
            skLineSegment(sketch, "E2.168.1.1", {"start": v(-157.15, 131.5) * mm, "end": v(-147.15, 131.5) * mm});
            skLineSegment(sketch, "E2.169.1.1", {"start": v(-158.55, 179.47) * mm, "end": v(-148.55, 179.47) * mm});
            skLineSegment(sketch, "E2.170.1.1", {"start": v(-159.96, 227.45) * mm, "end": v(-149.96, 227.45) * mm});
            skLineSegment(sketch, "E2.171.1.1", {"start": v(-145.85, 155.48) * mm, "end": v(-135.85, 155.48) * mm});
            skLineSegment(sketch, "E2.172.1.1", {"start": v(-147.25, 203.46) * mm, "end": v(-137.25, 203.46) * mm});
            skLineSegment(sketch, "E2.173.1.1", {"start": v(-133.15, 131.5) * mm, "end": v(-123.15, 131.5) * mm});
            skLineSegment(sketch, "E2.174.1.1", {"start": v(-134.55, 179.47) * mm, "end": v(-124.55, 179.47) * mm});
            skLineSegment(sketch, "E2.175.1.1", {"start": v(-135.96, 227.45) * mm, "end": v(-125.96, 227.45) * mm});
            skLineSegment(sketch, "E2.176.1.1", {"start": v(-122.2, 167.48) * mm, "end": v(-112.2, 167.48) * mm});
            skLineSegment(sketch, "E2.177.1.1", {"start": v(-123.6, 215.46) * mm, "end": v(-113.6, 215.46) * mm});
            skLineSegment(sketch, "E2.178.1.1", {"start": v(-110.9, 191.47) * mm, "end": v(-100.9, 191.47) * mm});
            skLineSegment(sketch, "E2.179.1.1", {"start": v(-209.25, 203.46) * mm, "end": v(-209.25, 213.46) * mm});
            skLineSegment(sketch, "E2.180.1.1", {"start": v(-196.2, 167.48) * mm, "end": v(-196.2, 177.48) * mm});
            skLineSegment(sketch, "E2.181.1.1", {"start": v(-197.6, 215.46) * mm, "end": v(-197.6, 225.46) * mm});
            skLineSegment(sketch, "E2.182.1.1", {"start": v(-183.85, 155.48) * mm, "end": v(-183.85, 165.48) * mm});
            skLineSegment(sketch, "E2.183.1.1", {"start": v(-185.25, 203.46) * mm, "end": v(-185.25, 213.46) * mm});
            skLineSegment(sketch, "E2.184.1.1", {"start": v(-171.15, 131.5) * mm, "end": v(-171.15, 141.5) * mm});
            skLineSegment(sketch, "E2.185.1.1", {"start": v(-172.55, 179.47) * mm, "end": v(-172.55, 189.47) * mm});
            skLineSegment(sketch, "E2.186.1.1", {"start": v(-173.96, 227.45) * mm, "end": v(-173.96, 237.45) * mm});
            skLineSegment(sketch, "E2.187.1.1", {"start": v(-159.85, 155.48) * mm, "end": v(-159.85, 165.48) * mm});
            skLineSegment(sketch, "E2.188.1.1", {"start": v(-161.25, 203.46) * mm, "end": v(-161.25, 213.46) * mm});
            skLineSegment(sketch, "E2.189.1.1", {"start": v(-147.15, 131.5) * mm, "end": v(-147.15, 141.5) * mm});
            skLineSegment(sketch, "E2.190.1.1", {"start": v(-148.55, 179.47) * mm, "end": v(-148.55, 189.47) * mm});
            skLineSegment(sketch, "E2.191.1.1", {"start": v(-149.96, 227.45) * mm, "end": v(-149.96, 237.45) * mm});
            skLineSegment(sketch, "E2.192.1.1", {"start": v(-135.85, 155.48) * mm, "end": v(-135.85, 165.48) * mm});
            skLineSegment(sketch, "E2.193.1.1", {"start": v(-137.25, 203.46) * mm, "end": v(-137.25, 213.46) * mm});
            skLineSegment(sketch, "E2.194.1.1", {"start": v(-123.15, 131.5) * mm, "end": v(-123.15, 141.5) * mm});
            skLineSegment(sketch, "E2.195.1.1", {"start": v(-124.55, 179.47) * mm, "end": v(-124.55, 189.47) * mm});
            skLineSegment(sketch, "E2.196.1.1", {"start": v(-125.96, 227.45) * mm, "end": v(-125.96, 237.45) * mm});
            skLineSegment(sketch, "E2.197.1.1", {"start": v(-112.2, 167.48) * mm, "end": v(-112.2, 177.48) * mm});
            skLineSegment(sketch, "E2.198.1.1", {"start": v(-113.6, 215.46) * mm, "end": v(-113.6, 225.46) * mm});
            skLineSegment(sketch, "E2.199.1.1", {"start": v(-100.9, 191.47) * mm, "end": v(-100.9, 201.47) * mm});
            skLineSegment(sketch, "E2.200.1.1", {"start": v(-219.25, 213.46) * mm, "end": v(-209.25, 213.46) * mm});
            skLineSegment(sketch, "E2.201.1.1", {"start": v(-206.2, 177.48) * mm, "end": v(-196.2, 177.48) * mm});
            skLineSegment(sketch, "E2.202.1.1", {"start": v(-207.6, 225.46) * mm, "end": v(-197.6, 225.46) * mm});
            skLineSegment(sketch, "E2.203.1.1", {"start": v(-193.85, 165.48) * mm, "end": v(-183.85, 165.48) * mm});
            skLineSegment(sketch, "E2.204.1.1", {"start": v(-195.25, 213.46) * mm, "end": v(-185.25, 213.46) * mm});
            skLineSegment(sketch, "E2.205.1.1", {"start": v(-181.15, 141.5) * mm, "end": v(-171.15, 141.5) * mm});
            skLineSegment(sketch, "E2.206.1.1", {"start": v(-182.55, 189.47) * mm, "end": v(-172.55, 189.47) * mm});
            skLineSegment(sketch, "E2.207.1.1", {"start": v(-183.96, 237.45) * mm, "end": v(-173.96, 237.45) * mm});
            skLineSegment(sketch, "E2.208.1.1", {"start": v(-169.85, 165.48) * mm, "end": v(-159.85, 165.48) * mm});
            skLineSegment(sketch, "E2.209.1.1", {"start": v(-171.25, 213.46) * mm, "end": v(-161.25, 213.46) * mm});
            skLineSegment(sketch, "E2.210.1.1", {"start": v(-157.15, 141.5) * mm, "end": v(-147.15, 141.5) * mm});
            skLineSegment(sketch, "E2.211.1.1", {"start": v(-158.55, 189.47) * mm, "end": v(-148.55, 189.47) * mm});
            skLineSegment(sketch, "E2.212.1.1", {"start": v(-159.96, 237.45) * mm, "end": v(-149.96, 237.45) * mm});
            skLineSegment(sketch, "E2.213.1.1", {"start": v(-145.85, 165.48) * mm, "end": v(-135.85, 165.48) * mm});
            skLineSegment(sketch, "E2.214.1.1", {"start": v(-147.25, 213.46) * mm, "end": v(-137.25, 213.46) * mm});
            skLineSegment(sketch, "E2.215.1.1", {"start": v(-133.15, 141.5) * mm, "end": v(-123.15, 141.5) * mm});
            skLineSegment(sketch, "E2.216.1.1", {"start": v(-134.55, 189.47) * mm, "end": v(-124.55, 189.47) * mm});
            skLineSegment(sketch, "E2.217.1.1", {"start": v(-135.96, 237.45) * mm, "end": v(-125.96, 237.45) * mm});
            skLineSegment(sketch, "E2.218.1.1", {"start": v(-122.2, 177.48) * mm, "end": v(-112.2, 177.48) * mm});
            skLineSegment(sketch, "E2.219.1.1", {"start": v(-123.6, 225.46) * mm, "end": v(-113.6, 225.46) * mm});
            skLineSegment(sketch, "E2.220.1.1", {"start": v(-110.9, 201.47) * mm, "end": v(-100.9, 201.47) * mm});
            skLineSegment(sketch, "E2.221.1.1", {"start": v(-219.25, 203.46) * mm, "end": v(-219.25, 213.46) * mm});
            skLineSegment(sketch, "E2.222.1.1", {"start": v(-206.2, 167.48) * mm, "end": v(-206.2, 177.48) * mm});
            skLineSegment(sketch, "E2.223.1.1", {"start": v(-207.6, 215.46) * mm, "end": v(-207.6, 225.46) * mm});
            skLineSegment(sketch, "E2.224.1.1", {"start": v(-193.85, 155.48) * mm, "end": v(-193.85, 165.48) * mm});
            skLineSegment(sketch, "E2.225.1.1", {"start": v(-195.25, 203.46) * mm, "end": v(-195.25, 213.46) * mm});
            skLineSegment(sketch, "E2.226.1.1", {"start": v(-181.15, 131.5) * mm, "end": v(-181.15, 141.5) * mm});
            skLineSegment(sketch, "E2.227.1.1", {"start": v(-182.55, 179.47) * mm, "end": v(-182.55, 189.47) * mm});
            skLineSegment(sketch, "E2.228.1.1", {"start": v(-183.96, 227.45) * mm, "end": v(-183.96, 237.45) * mm});
            skLineSegment(sketch, "E2.229.1.1", {"start": v(-169.85, 155.48) * mm, "end": v(-169.85, 165.48) * mm});
            skLineSegment(sketch, "E2.230.1.1", {"start": v(-171.25, 203.46) * mm, "end": v(-171.25, 213.46) * mm});
            skLineSegment(sketch, "E2.231.1.1", {"start": v(-157.15, 131.5) * mm, "end": v(-157.15, 141.5) * mm});
            skLineSegment(sketch, "E2.232.1.1", {"start": v(-158.55, 179.47) * mm, "end": v(-158.55, 189.47) * mm});
            skLineSegment(sketch, "E2.233.1.1", {"start": v(-159.96, 227.45) * mm, "end": v(-159.96, 237.45) * mm});
            skLineSegment(sketch, "E2.234.1.1", {"start": v(-145.85, 155.48) * mm, "end": v(-145.85, 165.48) * mm});
            skLineSegment(sketch, "E2.235.1.1", {"start": v(-147.25, 203.46) * mm, "end": v(-147.25, 213.46) * mm});
            skLineSegment(sketch, "E2.236.1.1", {"start": v(-133.15, 131.5) * mm, "end": v(-133.15, 141.5) * mm});
            skLineSegment(sketch, "E2.237.1.1", {"start": v(-134.55, 179.47) * mm, "end": v(-134.55, 189.47) * mm});
            skLineSegment(sketch, "E2.238.1.1", {"start": v(-135.96, 227.45) * mm, "end": v(-135.96, 237.45) * mm});
            skLineSegment(sketch, "E2.239.1.1", {"start": v(-122.2, 167.48) * mm, "end": v(-122.2, 177.48) * mm});
            skLineSegment(sketch, "E2.240.1.1", {"start": v(-123.6, 215.46) * mm, "end": v(-123.6, 225.46) * mm});
            skLineSegment(sketch, "E2.241.1.1", {"start": v(-110.9, 191.47) * mm, "end": v(-110.9, 201.47) * mm});
            skLineSegment(sketch, "E2.242.1.1", {"start": v(-205.15, 131.5) * mm, "end": v(-195.15, 131.5) * mm});
            skLineSegment(sketch, "E2.243.1.1", {"start": v(-206.55, 179.47) * mm, "end": v(-196.55, 179.47) * mm});
            skLineSegment(sketch, "E2.244.1.1", {"start": v(-192.8, 119.5) * mm, "end": v(-182.8, 119.5) * mm});
            skLineSegment(sketch, "E2.245.1.1", {"start": v(-194.2, 167.48) * mm, "end": v(-184.2, 167.48) * mm});
            skLineSegment(sketch, "E2.246.1.1", {"start": v(-195.6, 215.46) * mm, "end": v(-185.6, 215.46) * mm});
            skLineSegment(sketch, "E2.247.1.1", {"start": v(-181.5, 143.49) * mm, "end": v(-171.5, 143.49) * mm});
            skLineSegment(sketch, "E2.248.1.1", {"start": v(-182.9, 191.47) * mm, "end": v(-172.9, 191.47) * mm});
            skLineSegment(sketch, "E2.249.1.1", {"start": v(-168.8, 119.5) * mm, "end": v(-158.8, 119.5) * mm});
            skLineSegment(sketch, "E2.250.1.1", {"start": v(-170.2, 167.48) * mm, "end": v(-160.2, 167.48) * mm});
            skLineSegment(sketch, "E2.251.1.1", {"start": v(-171.6, 215.46) * mm, "end": v(-161.6, 215.46) * mm});
            skLineSegment(sketch, "E2.252.1.1", {"start": v(-157.5, 143.49) * mm, "end": v(-147.5, 143.49) * mm});
            skLineSegment(sketch, "E2.253.1.1", {"start": v(-158.9, 191.47) * mm, "end": v(-148.9, 191.47) * mm});
            skLineSegment(sketch, "E2.254.1.1", {"start": v(-144.8, 119.5) * mm, "end": v(-134.8, 119.5) * mm});
            skLineSegment(sketch, "E2.255.1.1", {"start": v(-146.2, 167.48) * mm, "end": v(-136.2, 167.48) * mm});
            skLineSegment(sketch, "E2.256.1.1", {"start": v(-147.6, 215.46) * mm, "end": v(-137.6, 215.46) * mm});
            skLineSegment(sketch, "E2.257.1.1", {"start": v(-133.5, 143.49) * mm, "end": v(-123.5, 143.49) * mm});
            skLineSegment(sketch, "E2.258.1.1", {"start": v(-134.9, 191.47) * mm, "end": v(-124.9, 191.47) * mm});
            skLineSegment(sketch, "E2.259.1.1", {"start": v(-121.15, 131.5) * mm, "end": v(-111.15, 131.5) * mm});
            skLineSegment(sketch, "E2.260.1.1", {"start": v(-122.55, 179.47) * mm, "end": v(-112.55, 179.47) * mm});
            skLineSegment(sketch, "E2.261.1.1", {"start": v(-109.85, 155.48) * mm, "end": v(-99.85, 155.48) * mm});
            skLineSegment(sketch, "E2.262.1.1", {"start": v(-111.25, 203.46) * mm, "end": v(-101.25, 203.46) * mm});
            skLineSegment(sketch, "E2.263.1.1", {"start": v(-195.15, 131.5) * mm, "end": v(-195.15, 141.5) * mm});
            skLineSegment(sketch, "E2.264.1.1", {"start": v(-196.55, 179.47) * mm, "end": v(-196.55, 189.47) * mm});
            skLineSegment(sketch, "E2.265.1.1", {"start": v(-182.8, 119.5) * mm, "end": v(-182.8, 129.5) * mm});
            skLineSegment(sketch, "E2.266.1.1", {"start": v(-184.2, 167.48) * mm, "end": v(-184.2, 177.48) * mm});
            skLineSegment(sketch, "E2.267.1.1", {"start": v(-185.6, 215.46) * mm, "end": v(-185.6, 225.46) * mm});
            skLineSegment(sketch, "E2.268.1.1", {"start": v(-171.5, 143.49) * mm, "end": v(-171.5, 153.49) * mm});
            skLineSegment(sketch, "E2.269.1.1", {"start": v(-172.9, 191.47) * mm, "end": v(-172.9, 201.47) * mm});
            skLineSegment(sketch, "E2.270.1.1", {"start": v(-158.8, 119.5) * mm, "end": v(-158.8, 129.5) * mm});
            skLineSegment(sketch, "E2.271.1.1", {"start": v(-160.2, 167.48) * mm, "end": v(-160.2, 177.48) * mm});
            skLineSegment(sketch, "E2.272.1.1", {"start": v(-161.6, 215.46) * mm, "end": v(-161.6, 225.46) * mm});
            skLineSegment(sketch, "E2.273.1.1", {"start": v(-147.5, 143.49) * mm, "end": v(-147.5, 153.49) * mm});
            skLineSegment(sketch, "E2.274.1.1", {"start": v(-148.9, 191.47) * mm, "end": v(-148.9, 201.47) * mm});
            skLineSegment(sketch, "E2.275.1.1", {"start": v(-134.8, 119.5) * mm, "end": v(-134.8, 129.5) * mm});
            skLineSegment(sketch, "E2.276.1.1", {"start": v(-136.2, 167.48) * mm, "end": v(-136.2, 177.48) * mm});
            skLineSegment(sketch, "E2.277.1.1", {"start": v(-137.6, 215.46) * mm, "end": v(-137.6, 225.46) * mm});
            skLineSegment(sketch, "E2.278.1.1", {"start": v(-123.5, 143.49) * mm, "end": v(-123.5, 153.49) * mm});
            skLineSegment(sketch, "E2.279.1.1", {"start": v(-124.9, 191.47) * mm, "end": v(-124.9, 201.47) * mm});
            skLineSegment(sketch, "E2.280.1.1", {"start": v(-111.15, 131.5) * mm, "end": v(-111.15, 141.5) * mm});
            skLineSegment(sketch, "E2.281.1.1", {"start": v(-112.55, 179.47) * mm, "end": v(-112.55, 189.47) * mm});
            skLineSegment(sketch, "E2.282.1.1", {"start": v(-99.85, 155.48) * mm, "end": v(-99.85, 165.48) * mm});
            skLineSegment(sketch, "E2.283.1.1", {"start": v(-101.25, 203.46) * mm, "end": v(-101.25, 213.46) * mm});
            skLineSegment(sketch, "E2.284.1.1", {"start": v(-205.15, 141.5) * mm, "end": v(-195.15, 141.5) * mm});
            skLineSegment(sketch, "E2.285.1.1", {"start": v(-206.55, 189.47) * mm, "end": v(-196.55, 189.47) * mm});
            skLineSegment(sketch, "E2.286.1.1", {"start": v(-192.8, 129.5) * mm, "end": v(-182.8, 129.5) * mm});
            skLineSegment(sketch, "E2.287.1.1", {"start": v(-194.2, 177.48) * mm, "end": v(-184.2, 177.48) * mm});
            skLineSegment(sketch, "E2.288.1.1", {"start": v(-195.6, 225.46) * mm, "end": v(-185.6, 225.46) * mm});
            skLineSegment(sketch, "E2.289.1.1", {"start": v(-181.5, 153.49) * mm, "end": v(-171.5, 153.49) * mm});
            skLineSegment(sketch, "E2.290.1.1", {"start": v(-182.9, 201.47) * mm, "end": v(-172.9, 201.47) * mm});
            skLineSegment(sketch, "E2.291.1.1", {"start": v(-168.8, 129.5) * mm, "end": v(-158.8, 129.5) * mm});
            skLineSegment(sketch, "E2.292.1.1", {"start": v(-170.2, 177.48) * mm, "end": v(-160.2, 177.48) * mm});
            skLineSegment(sketch, "E2.293.1.1", {"start": v(-171.6, 225.46) * mm, "end": v(-161.6, 225.46) * mm});
            skLineSegment(sketch, "E2.294.1.1", {"start": v(-157.5, 153.49) * mm, "end": v(-147.5, 153.49) * mm});
            skLineSegment(sketch, "E2.295.1.1", {"start": v(-158.9, 201.47) * mm, "end": v(-148.9, 201.47) * mm});
            skLineSegment(sketch, "E2.296.1.1", {"start": v(-144.8, 129.5) * mm, "end": v(-134.8, 129.5) * mm});
            skLineSegment(sketch, "E2.297.1.1", {"start": v(-146.2, 177.48) * mm, "end": v(-136.2, 177.48) * mm});
            skLineSegment(sketch, "E2.298.1.1", {"start": v(-147.6, 225.46) * mm, "end": v(-137.6, 225.46) * mm});
            skLineSegment(sketch, "E2.299.1.1", {"start": v(-133.5, 153.49) * mm, "end": v(-123.5, 153.49) * mm});
            skLineSegment(sketch, "E2.300.1.1", {"start": v(-134.9, 201.47) * mm, "end": v(-124.9, 201.47) * mm});
            skLineSegment(sketch, "E2.301.1.1", {"start": v(-121.15, 141.5) * mm, "end": v(-111.15, 141.5) * mm});
            skLineSegment(sketch, "E2.302.1.1", {"start": v(-122.55, 189.47) * mm, "end": v(-112.55, 189.47) * mm});
            skLineSegment(sketch, "E2.303.1.1", {"start": v(-109.85, 165.48) * mm, "end": v(-99.85, 165.48) * mm});
            skLineSegment(sketch, "E2.304.1.1", {"start": v(-111.25, 213.46) * mm, "end": v(-101.25, 213.46) * mm});
            skLineSegment(sketch, "E2.305.1.1", {"start": v(-205.15, 131.5) * mm, "end": v(-205.15, 141.5) * mm});
            skLineSegment(sketch, "E2.306.1.1", {"start": v(-206.55, 179.47) * mm, "end": v(-206.55, 189.47) * mm});
            skLineSegment(sketch, "E2.307.1.1", {"start": v(-192.8, 119.5) * mm, "end": v(-192.8, 129.5) * mm});
            skLineSegment(sketch, "E2.308.1.1", {"start": v(-194.2, 167.48) * mm, "end": v(-194.2, 177.48) * mm});
            skLineSegment(sketch, "E2.309.1.1", {"start": v(-195.6, 215.46) * mm, "end": v(-195.6, 225.46) * mm});
            skLineSegment(sketch, "E2.310.1.1", {"start": v(-181.5, 143.49) * mm, "end": v(-181.5, 153.49) * mm});
            skLineSegment(sketch, "E2.311.1.1", {"start": v(-182.9, 191.47) * mm, "end": v(-182.9, 201.47) * mm});
            skLineSegment(sketch, "E2.312.1.1", {"start": v(-168.8, 119.5) * mm, "end": v(-168.8, 129.5) * mm});
            skLineSegment(sketch, "E2.313.1.1", {"start": v(-170.2, 167.48) * mm, "end": v(-170.2, 177.48) * mm});
            skLineSegment(sketch, "E2.314.1.1", {"start": v(-171.6, 215.46) * mm, "end": v(-171.6, 225.46) * mm});
            skLineSegment(sketch, "E2.315.1.1", {"start": v(-157.5, 143.49) * mm, "end": v(-157.5, 153.49) * mm});
            skLineSegment(sketch, "E2.316.1.1", {"start": v(-158.9, 191.47) * mm, "end": v(-158.9, 201.47) * mm});
            skLineSegment(sketch, "E2.317.1.1", {"start": v(-144.8, 119.5) * mm, "end": v(-144.8, 129.5) * mm});
            skLineSegment(sketch, "E2.318.1.1", {"start": v(-146.2, 167.48) * mm, "end": v(-146.2, 177.48) * mm});
            skLineSegment(sketch, "E2.319.1.1", {"start": v(-147.6, 215.46) * mm, "end": v(-147.6, 225.46) * mm});
            skLineSegment(sketch, "E2.320.1.1", {"start": v(-133.5, 143.49) * mm, "end": v(-133.5, 153.49) * mm});
            skLineSegment(sketch, "E2.321.1.1", {"start": v(-134.9, 191.47) * mm, "end": v(-134.9, 201.47) * mm});
            skLineSegment(sketch, "E2.322.1.1", {"start": v(-121.15, 131.5) * mm, "end": v(-121.15, 141.5) * mm});
            skLineSegment(sketch, "E2.323.1.1", {"start": v(-122.55, 179.47) * mm, "end": v(-122.55, 189.47) * mm});
            skLineSegment(sketch, "E2.324.1.1", {"start": v(-109.85, 155.48) * mm, "end": v(-109.85, 165.48) * mm});
            skLineSegment(sketch, "E2.325.1.1", {"start": v(-111.25, 203.46) * mm, "end": v(-111.25, 213.46) * mm});
            skLineSegment(sketch, "E2.326.1.1", {"start": v(-205.5, 143.49) * mm, "end": v(-195.5, 143.49) * mm});
            skLineSegment(sketch, "E2.327.1.1", {"start": v(-206.9, 191.47) * mm, "end": v(-196.9, 191.47) * mm});
            skLineSegment(sketch, "E2.328.1.1", {"start": v(-193.15, 131.5) * mm, "end": v(-183.15, 131.5) * mm});
            skLineSegment(sketch, "E2.329.1.1", {"start": v(-194.55, 179.47) * mm, "end": v(-184.55, 179.47) * mm});
            skLineSegment(sketch, "E2.330.1.1", {"start": v(-195.96, 227.45) * mm, "end": v(-185.96, 227.45) * mm});
            skLineSegment(sketch, "E2.331.1.1", {"start": v(-181.85, 155.48) * mm, "end": v(-171.85, 155.48) * mm});
            skLineSegment(sketch, "E2.332.1.1", {"start": v(-183.25, 203.46) * mm, "end": v(-173.25, 203.46) * mm});
            skLineSegment(sketch, "E2.333.1.1", {"start": v(-169.15, 131.5) * mm, "end": v(-159.15, 131.5) * mm});
            skLineSegment(sketch, "E2.334.1.1", {"start": v(-170.55, 179.47) * mm, "end": v(-160.55, 179.47) * mm});
            skLineSegment(sketch, "E2.335.1.1", {"start": v(-171.96, 227.45) * mm, "end": v(-161.96, 227.45) * mm});
            skLineSegment(sketch, "E2.336.1.1", {"start": v(-157.85, 155.48) * mm, "end": v(-147.85, 155.48) * mm});
            skLineSegment(sketch, "E2.337.1.1", {"start": v(-159.25, 203.46) * mm, "end": v(-149.25, 203.46) * mm});
            skLineSegment(sketch, "E2.338.1.1", {"start": v(-145.15, 131.5) * mm, "end": v(-135.15, 131.5) * mm});
            skLineSegment(sketch, "E2.339.1.1", {"start": v(-146.55, 179.47) * mm, "end": v(-136.55, 179.47) * mm});
            skLineSegment(sketch, "E2.340.1.1", {"start": v(-147.96, 227.45) * mm, "end": v(-137.96, 227.45) * mm});
            skLineSegment(sketch, "E2.341.1.1", {"start": v(-133.85, 155.48) * mm, "end": v(-123.85, 155.48) * mm});
            skLineSegment(sketch, "E2.342.1.1", {"start": v(-135.25, 203.46) * mm, "end": v(-125.25, 203.46) * mm});
            skLineSegment(sketch, "E2.343.1.1", {"start": v(-121.5, 143.49) * mm, "end": v(-111.5, 143.49) * mm});
            skLineSegment(sketch, "E2.344.1.1", {"start": v(-122.9, 191.47) * mm, "end": v(-112.9, 191.47) * mm});
            skLineSegment(sketch, "E2.345.1.1", {"start": v(-110.2, 167.48) * mm, "end": v(-100.2, 167.48) * mm});
            skLineSegment(sketch, "E2.346.1.1", {"start": v(-133.85, 165.48) * mm, "end": v(-123.85, 165.48) * mm});
            skLineSegment(sketch, "E2.347.1.1", {"start": v(-134.2, 167.48) * mm, "end": v(-124.2, 167.48) * mm});
            skLineSegment(sketch, "E2.0.2.0", {"start": v(-335.55, 55.47) * mm, "end": v(-335.55, 65.47) * mm});
            skLineSegment(sketch, "E2.1.2.0", {"start": v(-325.55, 55.47) * mm, "end": v(-325.55, 65.47) * mm});
            skLineSegment(sketch, "E2.2.2.0", {"start": v(-335.55, 65.47) * mm, "end": v(-325.55, 65.47) * mm});
            skLineSegment(sketch, "E2.3.2.0", {"start": v(-334.5, 19.49) * mm, "end": v(-324.5, 19.49) * mm});
            skLineSegment(sketch, "E2.4.2.0", {"start": v(-324.5, 19.49) * mm, "end": v(-324.5, 29.49) * mm});
            skLineSegment(sketch, "E2.5.2.0", {"start": v(-334.5, 29.49) * mm, "end": v(-324.5, 29.49) * mm});
            skLineSegment(sketch, "E2.6.2.0", {"start": v(-334.5, 19.49) * mm, "end": v(-334.5, 29.49) * mm});
            skLineSegment(sketch, "E2.7.2.0", {"start": v(-334.85, 31.48) * mm, "end": v(-324.85, 31.48) * mm});
            skLineSegment(sketch, "E2.8.2.0", {"start": v(-324.85, 31.48) * mm, "end": v(-324.85, 41.48) * mm});
            skLineSegment(sketch, "E2.9.2.0", {"start": v(-334.85, 41.48) * mm, "end": v(-324.85, 41.48) * mm});
            skLineSegment(sketch, "E2.10.2.0", {"start": v(-334.85, 31.48) * mm, "end": v(-334.85, 41.48) * mm});
            skLineSegment(sketch, "E2.11.2.0", {"start": v(-335.2, 43.48) * mm, "end": v(-325.2, 43.48) * mm});
            skLineSegment(sketch, "E2.12.2.0", {"start": v(-325.2, 43.48) * mm, "end": v(-325.2, 53.48) * mm});
            skLineSegment(sketch, "E2.13.2.0", {"start": v(-335.2, 53.48) * mm, "end": v(-325.2, 53.48) * mm});
            skLineSegment(sketch, "E2.14.2.0", {"start": v(-335.2, 43.48) * mm, "end": v(-335.2, 53.48) * mm});
            skLineSegment(sketch, "E2.15.2.0", {"start": v(-335.55, 55.47) * mm, "end": v(-325.55, 55.47) * mm});
            skLineSegment(sketch, "E2.16.2.0", {"start": v(-322.5, 19.49) * mm, "end": v(-322.5, 29.49) * mm});
            skLineSegment(sketch, "E2.17.2.0", {"start": v(-323.9, 67.47) * mm, "end": v(-323.9, 77.47) * mm});
            skLineSegment(sketch, "E2.18.2.0", {"start": v(-310.15, 7.5) * mm, "end": v(-310.15, 17.5) * mm});
            skLineSegment(sketch, "E2.19.2.0", {"start": v(-311.55, 55.47) * mm, "end": v(-311.55, 65.47) * mm});
            skLineSegment(sketch, "E2.20.2.0", {"start": v(-312.96, 103.45) * mm, "end": v(-312.96, 113.45) * mm});
            skLineSegment(sketch, "E2.21.2.0", {"start": v(-298.85, 31.48) * mm, "end": v(-298.85, 41.48) * mm});
            skLineSegment(sketch, "E2.22.2.0", {"start": v(-300.25, 79.46) * mm, "end": v(-300.25, 89.46) * mm});
            skLineSegment(sketch, "E2.23.2.0", {"start": v(-286.15, 7.5) * mm, "end": v(-286.15, 17.5) * mm});
            skLineSegment(sketch, "E2.24.2.0", {"start": v(-287.55, 55.47) * mm, "end": v(-287.55, 65.47) * mm});
            skLineSegment(sketch, "E2.25.2.0", {"start": v(-288.96, 103.45) * mm, "end": v(-288.96, 113.45) * mm});
            skLineSegment(sketch, "E2.26.2.0", {"start": v(-274.85, 31.48) * mm, "end": v(-274.85, 41.48) * mm});
            skLineSegment(sketch, "E2.27.2.0", {"start": v(-276.25, 79.46) * mm, "end": v(-276.25, 89.46) * mm});
            skLineSegment(sketch, "E2.28.2.0", {"start": v(-262.15, 7.5) * mm, "end": v(-262.15, 17.5) * mm});
            skLineSegment(sketch, "E2.29.2.0", {"start": v(-263.55, 55.47) * mm, "end": v(-263.55, 65.47) * mm});
            skLineSegment(sketch, "E2.30.2.0", {"start": v(-264.96, 103.45) * mm, "end": v(-264.96, 113.45) * mm});
            skLineSegment(sketch, "E2.31.2.0", {"start": v(-250.85, 31.48) * mm, "end": v(-250.85, 41.48) * mm});
            skLineSegment(sketch, "E2.32.2.0", {"start": v(-252.25, 79.46) * mm, "end": v(-252.25, 89.46) * mm});
            skLineSegment(sketch, "E2.33.2.0", {"start": v(-238.5, 19.49) * mm, "end": v(-238.5, 29.49) * mm});
            skLineSegment(sketch, "E2.34.2.0", {"start": v(-239.9, 67.47) * mm, "end": v(-239.9, 77.47) * mm});
            skLineSegment(sketch, "E2.35.2.0", {"start": v(-227.2, 43.48) * mm, "end": v(-227.2, 53.48) * mm});
            skLineSegment(sketch, "E2.36.2.0", {"start": v(-312.5, 19.49) * mm, "end": v(-312.5, 29.49) * mm});
            skLineSegment(sketch, "E2.37.2.0", {"start": v(-313.9, 67.47) * mm, "end": v(-313.9, 77.47) * mm});
            skLineSegment(sketch, "E2.38.2.0", {"start": v(-300.15, 7.5) * mm, "end": v(-300.15, 17.5) * mm});
            skLineSegment(sketch, "E2.39.2.0", {"start": v(-301.55, 55.47) * mm, "end": v(-301.55, 65.47) * mm});
            skLineSegment(sketch, "E2.40.2.0", {"start": v(-302.96, 103.45) * mm, "end": v(-302.96, 113.45) * mm});
            skLineSegment(sketch, "E2.41.2.0", {"start": v(-288.85, 31.48) * mm, "end": v(-288.85, 41.48) * mm});
            skLineSegment(sketch, "E2.42.2.0", {"start": v(-290.25, 79.46) * mm, "end": v(-290.25, 89.46) * mm});
            skLineSegment(sketch, "E2.43.2.0", {"start": v(-276.15, 7.5) * mm, "end": v(-276.15, 17.5) * mm});
            skLineSegment(sketch, "E2.44.2.0", {"start": v(-277.55, 55.47) * mm, "end": v(-277.55, 65.47) * mm});
            skLineSegment(sketch, "E2.45.2.0", {"start": v(-278.96, 103.45) * mm, "end": v(-278.96, 113.45) * mm});
            skLineSegment(sketch, "E2.46.2.0", {"start": v(-264.85, 31.48) * mm, "end": v(-264.85, 41.48) * mm});
            skLineSegment(sketch, "E2.47.2.0", {"start": v(-266.25, 79.46) * mm, "end": v(-266.25, 89.46) * mm});
            skLineSegment(sketch, "E2.48.2.0", {"start": v(-252.15, 7.5) * mm, "end": v(-252.15, 17.5) * mm});
            skLineSegment(sketch, "E2.49.2.0", {"start": v(-253.55, 55.47) * mm, "end": v(-253.55, 65.47) * mm});
            skLineSegment(sketch, "E2.50.2.0", {"start": v(-254.96, 103.45) * mm, "end": v(-254.96, 113.45) * mm});
            skLineSegment(sketch, "E2.51.2.0", {"start": v(-240.85, 31.48) * mm, "end": v(-240.85, 41.48) * mm});
            skLineSegment(sketch, "E2.52.2.0", {"start": v(-242.25, 79.46) * mm, "end": v(-242.25, 89.46) * mm});
            skLineSegment(sketch, "E2.53.2.0", {"start": v(-228.5, 19.49) * mm, "end": v(-228.5, 29.49) * mm});
            skLineSegment(sketch, "E2.54.2.0", {"start": v(-229.9, 67.47) * mm, "end": v(-229.9, 77.47) * mm});
            skLineSegment(sketch, "E2.55.2.0", {"start": v(-217.2, 43.48) * mm, "end": v(-217.2, 53.48) * mm});
            skLineSegment(sketch, "E2.56.2.0", {"start": v(-322.5, 29.49) * mm, "end": v(-312.5, 29.49) * mm});
            skLineSegment(sketch, "E2.57.2.0", {"start": v(-323.9, 77.47) * mm, "end": v(-313.9, 77.47) * mm});
            skLineSegment(sketch, "E2.58.2.0", {"start": v(-310.15, 17.5) * mm, "end": v(-300.15, 17.5) * mm});
            skLineSegment(sketch, "E2.59.2.0", {"start": v(-311.55, 65.47) * mm, "end": v(-301.55, 65.47) * mm});
            skLineSegment(sketch, "E2.60.2.0", {"start": v(-312.96, 113.45) * mm, "end": v(-302.96, 113.45) * mm});
            skLineSegment(sketch, "E2.61.2.0", {"start": v(-298.85, 41.48) * mm, "end": v(-288.85, 41.48) * mm});
            skLineSegment(sketch, "E2.62.2.0", {"start": v(-300.25, 89.46) * mm, "end": v(-290.25, 89.46) * mm});
            skLineSegment(sketch, "E2.63.2.0", {"start": v(-286.15, 17.5) * mm, "end": v(-276.15, 17.5) * mm});
            skLineSegment(sketch, "E2.64.2.0", {"start": v(-287.55, 65.47) * mm, "end": v(-277.55, 65.47) * mm});
            skLineSegment(sketch, "E2.65.2.0", {"start": v(-288.96, 113.45) * mm, "end": v(-278.96, 113.45) * mm});
            skLineSegment(sketch, "E2.66.2.0", {"start": v(-274.85, 41.48) * mm, "end": v(-264.85, 41.48) * mm});
            skLineSegment(sketch, "E2.67.2.0", {"start": v(-276.25, 89.46) * mm, "end": v(-266.25, 89.46) * mm});
            skLineSegment(sketch, "E2.68.2.0", {"start": v(-262.15, 17.5) * mm, "end": v(-252.15, 17.5) * mm});
            skLineSegment(sketch, "E2.69.2.0", {"start": v(-263.55, 65.47) * mm, "end": v(-253.55, 65.47) * mm});
            skLineSegment(sketch, "E2.70.2.0", {"start": v(-264.96, 113.45) * mm, "end": v(-254.96, 113.45) * mm});
            skLineSegment(sketch, "E2.71.2.0", {"start": v(-252.25, 89.46) * mm, "end": v(-242.25, 89.46) * mm});
            skLineSegment(sketch, "E2.72.2.0", {"start": v(-238.5, 29.49) * mm, "end": v(-228.5, 29.49) * mm});
            skLineSegment(sketch, "E2.73.2.0", {"start": v(-239.9, 77.47) * mm, "end": v(-229.9, 77.47) * mm});
            skLineSegment(sketch, "E2.74.2.0", {"start": v(-227.2, 53.48) * mm, "end": v(-217.2, 53.48) * mm});
            skLineSegment(sketch, "E2.75.2.0", {"start": v(-335.9, 67.47) * mm, "end": v(-325.9, 67.47) * mm});
            skLineSegment(sketch, "E2.76.2.0", {"start": v(-322.85, 31.48) * mm, "end": v(-312.85, 31.48) * mm});
            skLineSegment(sketch, "E2.77.2.0", {"start": v(-324.25, 79.46) * mm, "end": v(-314.25, 79.46) * mm});
            skLineSegment(sketch, "E2.78.2.0", {"start": v(-310.5, 19.49) * mm, "end": v(-300.5, 19.49) * mm});
            skLineSegment(sketch, "E2.79.2.0", {"start": v(-311.9, 67.47) * mm, "end": v(-301.9, 67.47) * mm});
            skLineSegment(sketch, "E2.80.2.0", {"start": v(-297.8, -4.5) * mm, "end": v(-287.8, -4.5) * mm});
            skLineSegment(sketch, "E2.81.2.0", {"start": v(-299.2, 43.48) * mm, "end": v(-289.2, 43.48) * mm});
            skLineSegment(sketch, "E2.82.2.0", {"start": v(-300.6, 91.46) * mm, "end": v(-290.6, 91.46) * mm});
            skLineSegment(sketch, "E2.83.2.0", {"start": v(-286.5, 19.49) * mm, "end": v(-276.5, 19.49) * mm});
            skLineSegment(sketch, "E2.84.2.0", {"start": v(-287.9, 67.47) * mm, "end": v(-277.9, 67.47) * mm});
            skLineSegment(sketch, "E2.85.2.0", {"start": v(-273.8, -4.5) * mm, "end": v(-263.8, -4.5) * mm});
            skLineSegment(sketch, "E2.86.2.0", {"start": v(-275.2, 43.48) * mm, "end": v(-265.2, 43.48) * mm});
            skLineSegment(sketch, "E2.87.2.0", {"start": v(-276.6, 91.46) * mm, "end": v(-266.6, 91.46) * mm});
            skLineSegment(sketch, "E2.88.2.0", {"start": v(-262.5, 19.49) * mm, "end": v(-252.5, 19.49) * mm});
            skLineSegment(sketch, "E2.89.2.0", {"start": v(-263.9, 67.47) * mm, "end": v(-253.9, 67.47) * mm});
            skLineSegment(sketch, "E2.90.2.0", {"start": v(-249.8, -4.5) * mm, "end": v(-239.8, -4.5) * mm});
            skLineSegment(sketch, "E2.91.2.0", {"start": v(-252.6, 91.46) * mm, "end": v(-242.6, 91.46) * mm});
            skLineSegment(sketch, "E2.92.2.0", {"start": v(-238.85, 31.48) * mm, "end": v(-228.85, 31.48) * mm});
            skLineSegment(sketch, "E2.93.2.0", {"start": v(-240.25, 79.46) * mm, "end": v(-230.25, 79.46) * mm});
            skLineSegment(sketch, "E2.94.2.0", {"start": v(-227.55, 55.47) * mm, "end": v(-217.55, 55.47) * mm});
            skLineSegment(sketch, "E2.95.2.0", {"start": v(-325.9, 67.47) * mm, "end": v(-325.9, 77.47) * mm});
            skLineSegment(sketch, "E2.96.2.0", {"start": v(-312.85, 31.48) * mm, "end": v(-312.85, 41.48) * mm});
            skLineSegment(sketch, "E2.97.2.0", {"start": v(-314.25, 79.46) * mm, "end": v(-314.25, 89.46) * mm});
            skLineSegment(sketch, "E2.98.2.0", {"start": v(-300.5, 19.49) * mm, "end": v(-300.5, 29.49) * mm});
            skLineSegment(sketch, "E2.99.2.0", {"start": v(-301.9, 67.47) * mm, "end": v(-301.9, 77.47) * mm});
            skLineSegment(sketch, "E2.100.2.0", {"start": v(-287.8, -4.5) * mm, "end": v(-287.8, 5.5) * mm});
            skLineSegment(sketch, "E2.101.2.0", {"start": v(-289.2, 43.48) * mm, "end": v(-289.2, 53.48) * mm});
            skLineSegment(sketch, "E2.102.2.0", {"start": v(-290.6, 91.46) * mm, "end": v(-290.6, 101.46) * mm});
            skLineSegment(sketch, "E2.103.2.0", {"start": v(-276.5, 19.49) * mm, "end": v(-276.5, 29.49) * mm});
            skLineSegment(sketch, "E2.104.2.0", {"start": v(-277.9, 67.47) * mm, "end": v(-277.9, 77.47) * mm});
            skLineSegment(sketch, "E2.105.2.0", {"start": v(-263.8, -4.5) * mm, "end": v(-263.8, 5.5) * mm});
            skLineSegment(sketch, "E2.106.2.0", {"start": v(-265.2, 43.48) * mm, "end": v(-265.2, 53.48) * mm});
            skLineSegment(sketch, "E2.107.2.0", {"start": v(-266.6, 91.46) * mm, "end": v(-266.6, 101.46) * mm});
            skLineSegment(sketch, "E2.108.2.0", {"start": v(-252.5, 19.49) * mm, "end": v(-252.5, 29.49) * mm});
            skLineSegment(sketch, "E2.109.2.0", {"start": v(-253.9, 67.47) * mm, "end": v(-253.9, 77.47) * mm});
            skLineSegment(sketch, "E2.110.2.0", {"start": v(-239.8, -4.5) * mm, "end": v(-239.8, 5.5) * mm});
            skLineSegment(sketch, "E2.111.2.0", {"start": v(-241.2, 43.48) * mm, "end": v(-241.2, 53.48) * mm});
            skLineSegment(sketch, "E2.112.2.0", {"start": v(-242.6, 91.46) * mm, "end": v(-242.6, 101.46) * mm});
            skLineSegment(sketch, "E2.113.2.0", {"start": v(-228.85, 31.48) * mm, "end": v(-228.85, 41.48) * mm});
            skLineSegment(sketch, "E2.114.2.0", {"start": v(-230.25, 79.46) * mm, "end": v(-230.25, 89.46) * mm});
            skLineSegment(sketch, "E2.115.2.0", {"start": v(-217.55, 55.47) * mm, "end": v(-217.55, 65.47) * mm});
            skLineSegment(sketch, "E2.116.2.0", {"start": v(-335.9, 77.47) * mm, "end": v(-325.9, 77.47) * mm});
            skLineSegment(sketch, "E2.117.2.0", {"start": v(-322.85, 41.48) * mm, "end": v(-312.85, 41.48) * mm});
            skLineSegment(sketch, "E2.118.2.0", {"start": v(-324.25, 89.46) * mm, "end": v(-314.25, 89.46) * mm});
            skLineSegment(sketch, "E2.119.2.0", {"start": v(-310.5, 29.49) * mm, "end": v(-300.5, 29.49) * mm});
            skLineSegment(sketch, "E2.120.2.0", {"start": v(-311.9, 77.47) * mm, "end": v(-301.9, 77.47) * mm});
            skLineSegment(sketch, "E2.121.2.0", {"start": v(-297.8, 5.5) * mm, "end": v(-287.8, 5.5) * mm});
            skLineSegment(sketch, "E2.122.2.0", {"start": v(-299.2, 53.48) * mm, "end": v(-289.2, 53.48) * mm});
            skLineSegment(sketch, "E2.123.2.0", {"start": v(-300.6, 101.46) * mm, "end": v(-290.6, 101.46) * mm});
            skLineSegment(sketch, "E2.124.2.0", {"start": v(-286.5, 29.49) * mm, "end": v(-276.5, 29.49) * mm});
            skLineSegment(sketch, "E2.125.2.0", {"start": v(-287.9, 77.47) * mm, "end": v(-277.9, 77.47) * mm});
            skLineSegment(sketch, "E2.126.2.0", {"start": v(-273.8, 5.5) * mm, "end": v(-263.8, 5.5) * mm});
            skLineSegment(sketch, "E2.127.2.0", {"start": v(-275.2, 53.48) * mm, "end": v(-265.2, 53.48) * mm});
            skLineSegment(sketch, "E2.128.2.0", {"start": v(-276.6, 101.46) * mm, "end": v(-266.6, 101.46) * mm});
            skLineSegment(sketch, "E2.129.2.0", {"start": v(-262.5, 29.49) * mm, "end": v(-252.5, 29.49) * mm});
            skLineSegment(sketch, "E2.130.2.0", {"start": v(-263.9, 77.47) * mm, "end": v(-253.9, 77.47) * mm});
            skLineSegment(sketch, "E2.131.2.0", {"start": v(-249.8, 5.5) * mm, "end": v(-239.8, 5.5) * mm});
            skLineSegment(sketch, "E2.132.2.0", {"start": v(-251.2, 53.48) * mm, "end": v(-241.2, 53.48) * mm});
            skLineSegment(sketch, "E2.133.2.0", {"start": v(-252.6, 101.46) * mm, "end": v(-242.6, 101.46) * mm});
            skLineSegment(sketch, "E2.134.2.0", {"start": v(-238.85, 41.48) * mm, "end": v(-228.85, 41.48) * mm});
            skLineSegment(sketch, "E2.135.2.0", {"start": v(-240.25, 89.46) * mm, "end": v(-230.25, 89.46) * mm});
            skLineSegment(sketch, "E2.136.2.0", {"start": v(-227.55, 65.47) * mm, "end": v(-217.55, 65.47) * mm});
            skLineSegment(sketch, "E2.137.2.0", {"start": v(-335.9, 67.47) * mm, "end": v(-335.9, 77.47) * mm});
            skLineSegment(sketch, "E2.138.2.0", {"start": v(-322.85, 31.48) * mm, "end": v(-322.85, 41.48) * mm});
            skLineSegment(sketch, "E2.139.2.0", {"start": v(-324.25, 79.46) * mm, "end": v(-324.25, 89.46) * mm});
            skLineSegment(sketch, "E2.140.2.0", {"start": v(-310.5, 19.49) * mm, "end": v(-310.5, 29.49) * mm});
            skLineSegment(sketch, "E2.141.2.0", {"start": v(-311.9, 67.47) * mm, "end": v(-311.9, 77.47) * mm});
            skLineSegment(sketch, "E2.142.2.0", {"start": v(-297.8, -4.5) * mm, "end": v(-297.8, 5.5) * mm});
            skLineSegment(sketch, "E2.143.2.0", {"start": v(-299.2, 43.48) * mm, "end": v(-299.2, 53.48) * mm});
            skLineSegment(sketch, "E2.144.2.0", {"start": v(-300.6, 91.46) * mm, "end": v(-300.6, 101.46) * mm});
            skLineSegment(sketch, "E2.145.2.0", {"start": v(-286.5, 19.49) * mm, "end": v(-286.5, 29.49) * mm});
            skLineSegment(sketch, "E2.146.2.0", {"start": v(-287.9, 67.47) * mm, "end": v(-287.9, 77.47) * mm});
            skLineSegment(sketch, "E2.147.2.0", {"start": v(-273.8, -4.5) * mm, "end": v(-273.8, 5.5) * mm});
            skLineSegment(sketch, "E2.148.2.0", {"start": v(-275.2, 43.48) * mm, "end": v(-275.2, 53.48) * mm});
            skLineSegment(sketch, "E2.149.2.0", {"start": v(-276.6, 91.46) * mm, "end": v(-276.6, 101.46) * mm});
            skLineSegment(sketch, "E2.150.2.0", {"start": v(-262.5, 19.49) * mm, "end": v(-262.5, 29.49) * mm});
            skLineSegment(sketch, "E2.151.2.0", {"start": v(-263.9, 67.47) * mm, "end": v(-263.9, 77.47) * mm});
            skLineSegment(sketch, "E2.152.2.0", {"start": v(-249.8, -4.5) * mm, "end": v(-249.8, 5.5) * mm});
            skLineSegment(sketch, "E2.153.2.0", {"start": v(-251.2, 43.48) * mm, "end": v(-251.2, 53.48) * mm});
            skLineSegment(sketch, "E2.154.2.0", {"start": v(-252.6, 91.46) * mm, "end": v(-252.6, 101.46) * mm});
            skLineSegment(sketch, "E2.155.2.0", {"start": v(-238.85, 31.48) * mm, "end": v(-238.85, 41.48) * mm});
            skLineSegment(sketch, "E2.156.2.0", {"start": v(-240.25, 79.46) * mm, "end": v(-240.25, 89.46) * mm});
            skLineSegment(sketch, "E2.157.2.0", {"start": v(-227.55, 55.47) * mm, "end": v(-227.55, 65.47) * mm});
            skLineSegment(sketch, "E2.158.2.0", {"start": v(-336.25, 79.46) * mm, "end": v(-326.25, 79.46) * mm});
            skLineSegment(sketch, "E2.159.2.0", {"start": v(-323.2, 43.48) * mm, "end": v(-313.2, 43.48) * mm});
            skLineSegment(sketch, "E2.160.2.0", {"start": v(-324.6, 91.46) * mm, "end": v(-314.6, 91.46) * mm});
            skLineSegment(sketch, "E2.161.2.0", {"start": v(-310.85, 31.48) * mm, "end": v(-300.85, 31.48) * mm});
            skLineSegment(sketch, "E2.162.2.0", {"start": v(-312.25, 79.46) * mm, "end": v(-302.25, 79.46) * mm});
            skLineSegment(sketch, "E2.163.2.0", {"start": v(-298.15, 7.5) * mm, "end": v(-288.15, 7.5) * mm});
            skLineSegment(sketch, "E2.164.2.0", {"start": v(-299.55, 55.47) * mm, "end": v(-289.55, 55.47) * mm});
            skLineSegment(sketch, "E2.165.2.0", {"start": v(-300.96, 103.45) * mm, "end": v(-290.96, 103.45) * mm});
            skLineSegment(sketch, "E2.166.2.0", {"start": v(-286.85, 31.48) * mm, "end": v(-276.85, 31.48) * mm});
            skLineSegment(sketch, "E2.167.2.0", {"start": v(-288.25, 79.46) * mm, "end": v(-278.25, 79.46) * mm});
            skLineSegment(sketch, "E2.168.2.0", {"start": v(-274.15, 7.5) * mm, "end": v(-264.15, 7.5) * mm});
            skLineSegment(sketch, "E2.169.2.0", {"start": v(-275.55, 55.47) * mm, "end": v(-265.55, 55.47) * mm});
            skLineSegment(sketch, "E2.170.2.0", {"start": v(-276.96, 103.45) * mm, "end": v(-266.96, 103.45) * mm});
            skLineSegment(sketch, "E2.171.2.0", {"start": v(-262.85, 31.48) * mm, "end": v(-252.85, 31.48) * mm});
            skLineSegment(sketch, "E2.172.2.0", {"start": v(-264.25, 79.46) * mm, "end": v(-254.25, 79.46) * mm});
            skLineSegment(sketch, "E2.173.2.0", {"start": v(-250.15, 7.5) * mm, "end": v(-240.15, 7.5) * mm});
            skLineSegment(sketch, "E2.174.2.0", {"start": v(-251.55, 55.47) * mm, "end": v(-241.55, 55.47) * mm});
            skLineSegment(sketch, "E2.175.2.0", {"start": v(-252.96, 103.45) * mm, "end": v(-242.96, 103.45) * mm});
            skLineSegment(sketch, "E2.176.2.0", {"start": v(-239.2, 43.48) * mm, "end": v(-229.2, 43.48) * mm});
            skLineSegment(sketch, "E2.177.2.0", {"start": v(-240.6, 91.46) * mm, "end": v(-230.6, 91.46) * mm});
            skLineSegment(sketch, "E2.178.2.0", {"start": v(-227.9, 67.47) * mm, "end": v(-217.9, 67.47) * mm});
            skLineSegment(sketch, "E2.179.2.0", {"start": v(-326.25, 79.46) * mm, "end": v(-326.25, 89.46) * mm});
            skLineSegment(sketch, "E2.180.2.0", {"start": v(-313.2, 43.48) * mm, "end": v(-313.2, 53.48) * mm});
            skLineSegment(sketch, "E2.181.2.0", {"start": v(-314.6, 91.46) * mm, "end": v(-314.6, 101.46) * mm});
            skLineSegment(sketch, "E2.182.2.0", {"start": v(-300.85, 31.48) * mm, "end": v(-300.85, 41.48) * mm});
            skLineSegment(sketch, "E2.183.2.0", {"start": v(-302.25, 79.46) * mm, "end": v(-302.25, 89.46) * mm});
            skLineSegment(sketch, "E2.184.2.0", {"start": v(-288.15, 7.5) * mm, "end": v(-288.15, 17.5) * mm});
            skLineSegment(sketch, "E2.185.2.0", {"start": v(-289.55, 55.47) * mm, "end": v(-289.55, 65.47) * mm});
            skLineSegment(sketch, "E2.186.2.0", {"start": v(-290.96, 103.45) * mm, "end": v(-290.96, 113.45) * mm});
            skLineSegment(sketch, "E2.187.2.0", {"start": v(-276.85, 31.48) * mm, "end": v(-276.85, 41.48) * mm});
            skLineSegment(sketch, "E2.188.2.0", {"start": v(-278.25, 79.46) * mm, "end": v(-278.25, 89.46) * mm});
            skLineSegment(sketch, "E2.189.2.0", {"start": v(-264.15, 7.5) * mm, "end": v(-264.15, 17.5) * mm});
            skLineSegment(sketch, "E2.190.2.0", {"start": v(-265.55, 55.47) * mm, "end": v(-265.55, 65.47) * mm});
            skLineSegment(sketch, "E2.191.2.0", {"start": v(-266.96, 103.45) * mm, "end": v(-266.96, 113.45) * mm});
            skLineSegment(sketch, "E2.192.2.0", {"start": v(-252.85, 31.48) * mm, "end": v(-252.85, 41.48) * mm});
            skLineSegment(sketch, "E2.193.2.0", {"start": v(-254.25, 79.46) * mm, "end": v(-254.25, 89.46) * mm});
            skLineSegment(sketch, "E2.194.2.0", {"start": v(-240.15, 7.5) * mm, "end": v(-240.15, 17.5) * mm});
            skLineSegment(sketch, "E2.195.2.0", {"start": v(-241.55, 55.47) * mm, "end": v(-241.55, 65.47) * mm});
            skLineSegment(sketch, "E2.196.2.0", {"start": v(-242.96, 103.45) * mm, "end": v(-242.96, 113.45) * mm});
            skLineSegment(sketch, "E2.197.2.0", {"start": v(-229.2, 43.48) * mm, "end": v(-229.2, 53.48) * mm});
            skLineSegment(sketch, "E2.198.2.0", {"start": v(-230.6, 91.46) * mm, "end": v(-230.6, 101.46) * mm});
            skLineSegment(sketch, "E2.199.2.0", {"start": v(-217.9, 67.47) * mm, "end": v(-217.9, 77.47) * mm});
            skLineSegment(sketch, "E2.200.2.0", {"start": v(-336.25, 89.46) * mm, "end": v(-326.25, 89.46) * mm});
            skLineSegment(sketch, "E2.201.2.0", {"start": v(-323.2, 53.48) * mm, "end": v(-313.2, 53.48) * mm});
            skLineSegment(sketch, "E2.202.2.0", {"start": v(-324.6, 101.46) * mm, "end": v(-314.6, 101.46) * mm});
            skLineSegment(sketch, "E2.203.2.0", {"start": v(-310.85, 41.48) * mm, "end": v(-300.85, 41.48) * mm});
            skLineSegment(sketch, "E2.204.2.0", {"start": v(-312.25, 89.46) * mm, "end": v(-302.25, 89.46) * mm});
            skLineSegment(sketch, "E2.205.2.0", {"start": v(-298.15, 17.5) * mm, "end": v(-288.15, 17.5) * mm});
            skLineSegment(sketch, "E2.206.2.0", {"start": v(-299.55, 65.47) * mm, "end": v(-289.55, 65.47) * mm});
            skLineSegment(sketch, "E2.207.2.0", {"start": v(-300.96, 113.45) * mm, "end": v(-290.96, 113.45) * mm});
            skLineSegment(sketch, "E2.208.2.0", {"start": v(-286.85, 41.48) * mm, "end": v(-276.85, 41.48) * mm});
            skLineSegment(sketch, "E2.209.2.0", {"start": v(-288.25, 89.46) * mm, "end": v(-278.25, 89.46) * mm});
            skLineSegment(sketch, "E2.210.2.0", {"start": v(-274.15, 17.5) * mm, "end": v(-264.15, 17.5) * mm});
            skLineSegment(sketch, "E2.211.2.0", {"start": v(-275.55, 65.47) * mm, "end": v(-265.55, 65.47) * mm});
            skLineSegment(sketch, "E2.212.2.0", {"start": v(-276.96, 113.45) * mm, "end": v(-266.96, 113.45) * mm});
            skLineSegment(sketch, "E2.213.2.0", {"start": v(-262.85, 41.48) * mm, "end": v(-252.85, 41.48) * mm});
            skLineSegment(sketch, "E2.214.2.0", {"start": v(-264.25, 89.46) * mm, "end": v(-254.25, 89.46) * mm});
            skLineSegment(sketch, "E2.215.2.0", {"start": v(-250.15, 17.5) * mm, "end": v(-240.15, 17.5) * mm});
            skLineSegment(sketch, "E2.216.2.0", {"start": v(-251.55, 65.47) * mm, "end": v(-241.55, 65.47) * mm});
            skLineSegment(sketch, "E2.217.2.0", {"start": v(-252.96, 113.45) * mm, "end": v(-242.96, 113.45) * mm});
            skLineSegment(sketch, "E2.218.2.0", {"start": v(-239.2, 53.48) * mm, "end": v(-229.2, 53.48) * mm});
            skLineSegment(sketch, "E2.219.2.0", {"start": v(-240.6, 101.46) * mm, "end": v(-230.6, 101.46) * mm});
            skLineSegment(sketch, "E2.220.2.0", {"start": v(-227.9, 77.47) * mm, "end": v(-217.9, 77.47) * mm});
            skLineSegment(sketch, "E2.221.2.0", {"start": v(-336.25, 79.46) * mm, "end": v(-336.25, 89.46) * mm});
            skLineSegment(sketch, "E2.222.2.0", {"start": v(-323.2, 43.48) * mm, "end": v(-323.2, 53.48) * mm});
            skLineSegment(sketch, "E2.223.2.0", {"start": v(-324.6, 91.46) * mm, "end": v(-324.6, 101.46) * mm});
            skLineSegment(sketch, "E2.224.2.0", {"start": v(-310.85, 31.48) * mm, "end": v(-310.85, 41.48) * mm});
            skLineSegment(sketch, "E2.225.2.0", {"start": v(-312.25, 79.46) * mm, "end": v(-312.25, 89.46) * mm});
            skLineSegment(sketch, "E2.226.2.0", {"start": v(-298.15, 7.5) * mm, "end": v(-298.15, 17.5) * mm});
            skLineSegment(sketch, "E2.227.2.0", {"start": v(-299.55, 55.47) * mm, "end": v(-299.55, 65.47) * mm});
            skLineSegment(sketch, "E2.228.2.0", {"start": v(-300.96, 103.45) * mm, "end": v(-300.96, 113.45) * mm});
            skLineSegment(sketch, "E2.229.2.0", {"start": v(-286.85, 31.48) * mm, "end": v(-286.85, 41.48) * mm});
            skLineSegment(sketch, "E2.230.2.0", {"start": v(-288.25, 79.46) * mm, "end": v(-288.25, 89.46) * mm});
            skLineSegment(sketch, "E2.231.2.0", {"start": v(-274.15, 7.5) * mm, "end": v(-274.15, 17.5) * mm});
            skLineSegment(sketch, "E2.232.2.0", {"start": v(-275.55, 55.47) * mm, "end": v(-275.55, 65.47) * mm});
            skLineSegment(sketch, "E2.233.2.0", {"start": v(-276.96, 103.45) * mm, "end": v(-276.96, 113.45) * mm});
            skLineSegment(sketch, "E2.234.2.0", {"start": v(-262.85, 31.48) * mm, "end": v(-262.85, 41.48) * mm});
            skLineSegment(sketch, "E2.235.2.0", {"start": v(-264.25, 79.46) * mm, "end": v(-264.25, 89.46) * mm});
            skLineSegment(sketch, "E2.236.2.0", {"start": v(-250.15, 7.5) * mm, "end": v(-250.15, 17.5) * mm});
            skLineSegment(sketch, "E2.237.2.0", {"start": v(-251.55, 55.47) * mm, "end": v(-251.55, 65.47) * mm});
            skLineSegment(sketch, "E2.238.2.0", {"start": v(-252.96, 103.45) * mm, "end": v(-252.96, 113.45) * mm});
            skLineSegment(sketch, "E2.239.2.0", {"start": v(-239.2, 43.48) * mm, "end": v(-239.2, 53.48) * mm});
            skLineSegment(sketch, "E2.240.2.0", {"start": v(-240.6, 91.46) * mm, "end": v(-240.6, 101.46) * mm});
            skLineSegment(sketch, "E2.241.2.0", {"start": v(-227.9, 67.47) * mm, "end": v(-227.9, 77.47) * mm});
            skLineSegment(sketch, "E2.242.2.0", {"start": v(-322.15, 7.5) * mm, "end": v(-312.15, 7.5) * mm});
            skLineSegment(sketch, "E2.243.2.0", {"start": v(-323.55, 55.47) * mm, "end": v(-313.55, 55.47) * mm});
            skLineSegment(sketch, "E2.244.2.0", {"start": v(-309.8, -4.5) * mm, "end": v(-299.8, -4.5) * mm});
            skLineSegment(sketch, "E2.245.2.0", {"start": v(-311.2, 43.48) * mm, "end": v(-301.2, 43.48) * mm});
            skLineSegment(sketch, "E2.246.2.0", {"start": v(-312.6, 91.46) * mm, "end": v(-302.6, 91.46) * mm});
            skLineSegment(sketch, "E2.247.2.0", {"start": v(-298.5, 19.49) * mm, "end": v(-288.5, 19.49) * mm});
            skLineSegment(sketch, "E2.248.2.0", {"start": v(-299.9, 67.47) * mm, "end": v(-289.9, 67.47) * mm});
            skLineSegment(sketch, "E2.249.2.0", {"start": v(-285.8, -4.5) * mm, "end": v(-275.8, -4.5) * mm});
            skLineSegment(sketch, "E2.250.2.0", {"start": v(-287.2, 43.48) * mm, "end": v(-277.2, 43.48) * mm});
            skLineSegment(sketch, "E2.251.2.0", {"start": v(-288.6, 91.46) * mm, "end": v(-278.6, 91.46) * mm});
            skLineSegment(sketch, "E2.252.2.0", {"start": v(-274.5, 19.49) * mm, "end": v(-264.5, 19.49) * mm});
            skLineSegment(sketch, "E2.253.2.0", {"start": v(-275.9, 67.47) * mm, "end": v(-265.9, 67.47) * mm});
            skLineSegment(sketch, "E2.254.2.0", {"start": v(-261.8, -4.5) * mm, "end": v(-251.8, -4.5) * mm});
            skLineSegment(sketch, "E2.255.2.0", {"start": v(-263.2, 43.48) * mm, "end": v(-253.2, 43.48) * mm});
            skLineSegment(sketch, "E2.256.2.0", {"start": v(-264.6, 91.46) * mm, "end": v(-254.6, 91.46) * mm});
            skLineSegment(sketch, "E2.257.2.0", {"start": v(-250.5, 19.49) * mm, "end": v(-240.5, 19.49) * mm});
            skLineSegment(sketch, "E2.258.2.0", {"start": v(-251.9, 67.47) * mm, "end": v(-241.9, 67.47) * mm});
            skLineSegment(sketch, "E2.259.2.0", {"start": v(-238.15, 7.5) * mm, "end": v(-228.15, 7.5) * mm});
            skLineSegment(sketch, "E2.260.2.0", {"start": v(-239.55, 55.47) * mm, "end": v(-229.55, 55.47) * mm});
            skLineSegment(sketch, "E2.261.2.0", {"start": v(-226.85, 31.48) * mm, "end": v(-216.85, 31.48) * mm});
            skLineSegment(sketch, "E2.262.2.0", {"start": v(-228.25, 79.46) * mm, "end": v(-218.25, 79.46) * mm});
            skLineSegment(sketch, "E2.263.2.0", {"start": v(-312.15, 7.5) * mm, "end": v(-312.15, 17.5) * mm});
            skLineSegment(sketch, "E2.264.2.0", {"start": v(-313.55, 55.47) * mm, "end": v(-313.55, 65.47) * mm});
            skLineSegment(sketch, "E2.265.2.0", {"start": v(-299.8, -4.5) * mm, "end": v(-299.8, 5.5) * mm});
            skLineSegment(sketch, "E2.266.2.0", {"start": v(-301.2, 43.48) * mm, "end": v(-301.2, 53.48) * mm});
            skLineSegment(sketch, "E2.267.2.0", {"start": v(-302.6, 91.46) * mm, "end": v(-302.6, 101.46) * mm});
            skLineSegment(sketch, "E2.268.2.0", {"start": v(-288.5, 19.49) * mm, "end": v(-288.5, 29.49) * mm});
            skLineSegment(sketch, "E2.269.2.0", {"start": v(-289.9, 67.47) * mm, "end": v(-289.9, 77.47) * mm});
            skLineSegment(sketch, "E2.270.2.0", {"start": v(-275.8, -4.5) * mm, "end": v(-275.8, 5.5) * mm});
            skLineSegment(sketch, "E2.271.2.0", {"start": v(-277.2, 43.48) * mm, "end": v(-277.2, 53.48) * mm});
            skLineSegment(sketch, "E2.272.2.0", {"start": v(-278.6, 91.46) * mm, "end": v(-278.6, 101.46) * mm});
            skLineSegment(sketch, "E2.273.2.0", {"start": v(-264.5, 19.49) * mm, "end": v(-264.5, 29.49) * mm});
            skLineSegment(sketch, "E2.274.2.0", {"start": v(-265.9, 67.47) * mm, "end": v(-265.9, 77.47) * mm});
            skLineSegment(sketch, "E2.275.2.0", {"start": v(-251.8, -4.5) * mm, "end": v(-251.8, 5.5) * mm});
            skLineSegment(sketch, "E2.276.2.0", {"start": v(-253.2, 43.48) * mm, "end": v(-253.2, 53.48) * mm});
            skLineSegment(sketch, "E2.277.2.0", {"start": v(-254.6, 91.46) * mm, "end": v(-254.6, 101.46) * mm});
            skLineSegment(sketch, "E2.278.2.0", {"start": v(-240.5, 19.49) * mm, "end": v(-240.5, 29.49) * mm});
            skLineSegment(sketch, "E2.279.2.0", {"start": v(-241.9, 67.47) * mm, "end": v(-241.9, 77.47) * mm});
            skLineSegment(sketch, "E2.280.2.0", {"start": v(-228.15, 7.5) * mm, "end": v(-228.15, 17.5) * mm});
            skLineSegment(sketch, "E2.281.2.0", {"start": v(-229.55, 55.47) * mm, "end": v(-229.55, 65.47) * mm});
            skLineSegment(sketch, "E2.282.2.0", {"start": v(-216.85, 31.48) * mm, "end": v(-216.85, 41.48) * mm});
            skLineSegment(sketch, "E2.283.2.0", {"start": v(-218.25, 79.46) * mm, "end": v(-218.25, 89.46) * mm});
            skLineSegment(sketch, "E2.284.2.0", {"start": v(-322.15, 17.5) * mm, "end": v(-312.15, 17.5) * mm});
            skLineSegment(sketch, "E2.285.2.0", {"start": v(-323.55, 65.47) * mm, "end": v(-313.55, 65.47) * mm});
            skLineSegment(sketch, "E2.286.2.0", {"start": v(-309.8, 5.5) * mm, "end": v(-299.8, 5.5) * mm});
            skLineSegment(sketch, "E2.287.2.0", {"start": v(-311.2, 53.48) * mm, "end": v(-301.2, 53.48) * mm});
            skLineSegment(sketch, "E2.288.2.0", {"start": v(-312.6, 101.46) * mm, "end": v(-302.6, 101.46) * mm});
            skLineSegment(sketch, "E2.289.2.0", {"start": v(-298.5, 29.49) * mm, "end": v(-288.5, 29.49) * mm});
            skLineSegment(sketch, "E2.290.2.0", {"start": v(-299.9, 77.47) * mm, "end": v(-289.9, 77.47) * mm});
            skLineSegment(sketch, "E2.291.2.0", {"start": v(-285.8, 5.5) * mm, "end": v(-275.8, 5.5) * mm});
            skLineSegment(sketch, "E2.292.2.0", {"start": v(-287.2, 53.48) * mm, "end": v(-277.2, 53.48) * mm});
            skLineSegment(sketch, "E2.293.2.0", {"start": v(-288.6, 101.46) * mm, "end": v(-278.6, 101.46) * mm});
            skLineSegment(sketch, "E2.294.2.0", {"start": v(-274.5, 29.49) * mm, "end": v(-264.5, 29.49) * mm});
            skLineSegment(sketch, "E2.295.2.0", {"start": v(-275.9, 77.47) * mm, "end": v(-265.9, 77.47) * mm});
            skLineSegment(sketch, "E2.296.2.0", {"start": v(-261.8, 5.5) * mm, "end": v(-251.8, 5.5) * mm});
            skLineSegment(sketch, "E2.297.2.0", {"start": v(-263.2, 53.48) * mm, "end": v(-253.2, 53.48) * mm});
            skLineSegment(sketch, "E2.298.2.0", {"start": v(-264.6, 101.46) * mm, "end": v(-254.6, 101.46) * mm});
            skLineSegment(sketch, "E2.299.2.0", {"start": v(-250.5, 29.49) * mm, "end": v(-240.5, 29.49) * mm});
            skLineSegment(sketch, "E2.300.2.0", {"start": v(-251.9, 77.47) * mm, "end": v(-241.9, 77.47) * mm});
            skLineSegment(sketch, "E2.301.2.0", {"start": v(-238.15, 17.5) * mm, "end": v(-228.15, 17.5) * mm});
            skLineSegment(sketch, "E2.302.2.0", {"start": v(-239.55, 65.47) * mm, "end": v(-229.55, 65.47) * mm});
            skLineSegment(sketch, "E2.303.2.0", {"start": v(-226.85, 41.48) * mm, "end": v(-216.85, 41.48) * mm});
            skLineSegment(sketch, "E2.304.2.0", {"start": v(-228.25, 89.46) * mm, "end": v(-218.25, 89.46) * mm});
            skLineSegment(sketch, "E2.305.2.0", {"start": v(-322.15, 7.5) * mm, "end": v(-322.15, 17.5) * mm});
            skLineSegment(sketch, "E2.306.2.0", {"start": v(-323.55, 55.47) * mm, "end": v(-323.55, 65.47) * mm});
            skLineSegment(sketch, "E2.307.2.0", {"start": v(-309.8, -4.5) * mm, "end": v(-309.8, 5.5) * mm});
            skLineSegment(sketch, "E2.308.2.0", {"start": v(-311.2, 43.48) * mm, "end": v(-311.2, 53.48) * mm});
            skLineSegment(sketch, "E2.309.2.0", {"start": v(-312.6, 91.46) * mm, "end": v(-312.6, 101.46) * mm});
            skLineSegment(sketch, "E2.310.2.0", {"start": v(-298.5, 19.49) * mm, "end": v(-298.5, 29.49) * mm});
            skLineSegment(sketch, "E2.311.2.0", {"start": v(-299.9, 67.47) * mm, "end": v(-299.9, 77.47) * mm});
            skLineSegment(sketch, "E2.312.2.0", {"start": v(-285.8, -4.5) * mm, "end": v(-285.8, 5.5) * mm});
            skLineSegment(sketch, "E2.313.2.0", {"start": v(-287.2, 43.48) * mm, "end": v(-287.2, 53.48) * mm});
            skLineSegment(sketch, "E2.314.2.0", {"start": v(-288.6, 91.46) * mm, "end": v(-288.6, 101.46) * mm});
            skLineSegment(sketch, "E2.315.2.0", {"start": v(-274.5, 19.49) * mm, "end": v(-274.5, 29.49) * mm});
            skLineSegment(sketch, "E2.316.2.0", {"start": v(-275.9, 67.47) * mm, "end": v(-275.9, 77.47) * mm});
            skLineSegment(sketch, "E2.317.2.0", {"start": v(-261.8, -4.5) * mm, "end": v(-261.8, 5.5) * mm});
            skLineSegment(sketch, "E2.318.2.0", {"start": v(-263.2, 43.48) * mm, "end": v(-263.2, 53.48) * mm});
            skLineSegment(sketch, "E2.319.2.0", {"start": v(-264.6, 91.46) * mm, "end": v(-264.6, 101.46) * mm});
            skLineSegment(sketch, "E2.320.2.0", {"start": v(-250.5, 19.49) * mm, "end": v(-250.5, 29.49) * mm});
            skLineSegment(sketch, "E2.321.2.0", {"start": v(-251.9, 67.47) * mm, "end": v(-251.9, 77.47) * mm});
            skLineSegment(sketch, "E2.322.2.0", {"start": v(-238.15, 7.5) * mm, "end": v(-238.15, 17.5) * mm});
            skLineSegment(sketch, "E2.323.2.0", {"start": v(-239.55, 55.47) * mm, "end": v(-239.55, 65.47) * mm});
            skLineSegment(sketch, "E2.324.2.0", {"start": v(-226.85, 31.48) * mm, "end": v(-226.85, 41.48) * mm});
            skLineSegment(sketch, "E2.325.2.0", {"start": v(-228.25, 79.46) * mm, "end": v(-228.25, 89.46) * mm});
            skLineSegment(sketch, "E2.326.2.0", {"start": v(-322.5, 19.49) * mm, "end": v(-312.5, 19.49) * mm});
            skLineSegment(sketch, "E2.327.2.0", {"start": v(-323.9, 67.47) * mm, "end": v(-313.9, 67.47) * mm});
            skLineSegment(sketch, "E2.328.2.0", {"start": v(-310.15, 7.5) * mm, "end": v(-300.15, 7.5) * mm});
            skLineSegment(sketch, "E2.329.2.0", {"start": v(-311.55, 55.47) * mm, "end": v(-301.55, 55.47) * mm});
            skLineSegment(sketch, "E2.330.2.0", {"start": v(-312.96, 103.45) * mm, "end": v(-302.96, 103.45) * mm});
            skLineSegment(sketch, "E2.331.2.0", {"start": v(-298.85, 31.48) * mm, "end": v(-288.85, 31.48) * mm});
            skLineSegment(sketch, "E2.332.2.0", {"start": v(-300.25, 79.46) * mm, "end": v(-290.25, 79.46) * mm});
            skLineSegment(sketch, "E2.333.2.0", {"start": v(-286.15, 7.5) * mm, "end": v(-276.15, 7.5) * mm});
            skLineSegment(sketch, "E2.334.2.0", {"start": v(-287.55, 55.47) * mm, "end": v(-277.55, 55.47) * mm});
            skLineSegment(sketch, "E2.335.2.0", {"start": v(-288.96, 103.45) * mm, "end": v(-278.96, 103.45) * mm});
            skLineSegment(sketch, "E2.336.2.0", {"start": v(-274.85, 31.48) * mm, "end": v(-264.85, 31.48) * mm});
            skLineSegment(sketch, "E2.337.2.0", {"start": v(-276.25, 79.46) * mm, "end": v(-266.25, 79.46) * mm});
            skLineSegment(sketch, "E2.338.2.0", {"start": v(-262.15, 7.5) * mm, "end": v(-252.15, 7.5) * mm});
            skLineSegment(sketch, "E2.339.2.0", {"start": v(-263.55, 55.47) * mm, "end": v(-253.55, 55.47) * mm});
            skLineSegment(sketch, "E2.340.2.0", {"start": v(-264.96, 103.45) * mm, "end": v(-254.96, 103.45) * mm});
            skLineSegment(sketch, "E2.341.2.0", {"start": v(-250.85, 31.48) * mm, "end": v(-240.85, 31.48) * mm});
            skLineSegment(sketch, "E2.342.2.0", {"start": v(-252.25, 79.46) * mm, "end": v(-242.25, 79.46) * mm});
            skLineSegment(sketch, "E2.343.2.0", {"start": v(-238.5, 19.49) * mm, "end": v(-228.5, 19.49) * mm});
            skLineSegment(sketch, "E2.344.2.0", {"start": v(-239.9, 67.47) * mm, "end": v(-229.9, 67.47) * mm});
            skLineSegment(sketch, "E2.345.2.0", {"start": v(-227.2, 43.48) * mm, "end": v(-217.2, 43.48) * mm});
            skLineSegment(sketch, "E2.346.2.0", {"start": v(-250.85, 41.48) * mm, "end": v(-240.85, 41.48) * mm});
            skLineSegment(sketch, "E2.347.2.0", {"start": v(-251.2, 43.48) * mm, "end": v(-241.2, 43.48) * mm});
            skLineSegment(sketch, "E2.18.2.1", {"start": v(-310.15, 131.5) * mm, "end": v(-310.15, 141.5) * mm});
            skLineSegment(sketch, "E2.21.2.1", {"start": v(-298.85, 155.48) * mm, "end": v(-298.85, 165.48) * mm});
            skLineSegment(sketch, "E2.23.2.1", {"start": v(-286.15, 131.5) * mm, "end": v(-286.15, 141.5) * mm});
            skLineSegment(sketch, "E2.24.2.1", {"start": v(-287.55, 179.47) * mm, "end": v(-287.55, 189.47) * mm});
            skLineSegment(sketch, "E2.26.2.1", {"start": v(-274.85, 155.48) * mm, "end": v(-274.85, 165.48) * mm});
            skLineSegment(sketch, "E2.27.2.1", {"start": v(-276.25, 203.46) * mm, "end": v(-276.25, 213.46) * mm});
            skLineSegment(sketch, "E2.28.2.1", {"start": v(-262.15, 131.5) * mm, "end": v(-262.15, 141.5) * mm});
            skLineSegment(sketch, "E2.29.2.1", {"start": v(-263.55, 179.47) * mm, "end": v(-263.55, 189.47) * mm});
            skLineSegment(sketch, "E2.30.2.1", {"start": v(-264.96, 227.45) * mm, "end": v(-264.96, 237.45) * mm});
            skLineSegment(sketch, "E2.31.2.1", {"start": v(-250.85, 155.48) * mm, "end": v(-250.85, 165.48) * mm});
            skLineSegment(sketch, "E2.32.2.1", {"start": v(-252.25, 203.46) * mm, "end": v(-252.25, 213.46) * mm});
            skLineSegment(sketch, "E2.33.2.1", {"start": v(-238.5, 143.49) * mm, "end": v(-238.5, 153.49) * mm});
            skLineSegment(sketch, "E2.34.2.1", {"start": v(-239.9, 191.47) * mm, "end": v(-239.9, 201.47) * mm});
            skLineSegment(sketch, "E2.35.2.1", {"start": v(-227.2, 167.48) * mm, "end": v(-227.2, 177.48) * mm});
            skLineSegment(sketch, "E2.38.2.1", {"start": v(-300.15, 131.5) * mm, "end": v(-300.15, 141.5) * mm});
            skLineSegment(sketch, "E2.41.2.1", {"start": v(-288.85, 155.48) * mm, "end": v(-288.85, 165.48) * mm});
            skLineSegment(sketch, "E2.43.2.1", {"start": v(-276.15, 131.5) * mm, "end": v(-276.15, 141.5) * mm});
            skLineSegment(sketch, "E2.44.2.1", {"start": v(-277.55, 179.47) * mm, "end": v(-277.55, 189.47) * mm});
            skLineSegment(sketch, "E2.46.2.1", {"start": v(-264.85, 155.48) * mm, "end": v(-264.85, 165.48) * mm});
            skLineSegment(sketch, "E2.47.2.1", {"start": v(-266.25, 203.46) * mm, "end": v(-266.25, 213.46) * mm});
            skLineSegment(sketch, "E2.48.2.1", {"start": v(-252.15, 131.5) * mm, "end": v(-252.15, 141.5) * mm});
            skLineSegment(sketch, "E2.49.2.1", {"start": v(-253.55, 179.47) * mm, "end": v(-253.55, 189.47) * mm});
            skLineSegment(sketch, "E2.50.2.1", {"start": v(-254.96, 227.45) * mm, "end": v(-254.96, 237.45) * mm});
            skLineSegment(sketch, "E2.51.2.1", {"start": v(-240.85, 155.48) * mm, "end": v(-240.85, 165.48) * mm});
            skLineSegment(sketch, "E2.52.2.1", {"start": v(-242.25, 203.46) * mm, "end": v(-242.25, 213.46) * mm});
            skLineSegment(sketch, "E2.53.2.1", {"start": v(-228.5, 143.49) * mm, "end": v(-228.5, 153.49) * mm});
            skLineSegment(sketch, "E2.54.2.1", {"start": v(-229.9, 191.47) * mm, "end": v(-229.9, 201.47) * mm});
            skLineSegment(sketch, "E2.55.2.1", {"start": v(-217.2, 167.48) * mm, "end": v(-217.2, 177.48) * mm});
            skLineSegment(sketch, "E2.58.2.1", {"start": v(-310.15, 141.5) * mm, "end": v(-300.15, 141.5) * mm});
            skLineSegment(sketch, "E2.61.2.1", {"start": v(-298.85, 165.48) * mm, "end": v(-288.85, 165.48) * mm});
            skLineSegment(sketch, "E2.63.2.1", {"start": v(-286.15, 141.5) * mm, "end": v(-276.15, 141.5) * mm});
            skLineSegment(sketch, "E2.64.2.1", {"start": v(-287.55, 189.47) * mm, "end": v(-277.55, 189.47) * mm});
            skLineSegment(sketch, "E2.66.2.1", {"start": v(-274.85, 165.48) * mm, "end": v(-264.85, 165.48) * mm});
            skLineSegment(sketch, "E2.67.2.1", {"start": v(-276.25, 213.46) * mm, "end": v(-266.25, 213.46) * mm});
            skLineSegment(sketch, "E2.68.2.1", {"start": v(-262.15, 141.5) * mm, "end": v(-252.15, 141.5) * mm});
            skLineSegment(sketch, "E2.69.2.1", {"start": v(-263.55, 189.47) * mm, "end": v(-253.55, 189.47) * mm});
            skLineSegment(sketch, "E2.70.2.1", {"start": v(-264.96, 237.45) * mm, "end": v(-254.96, 237.45) * mm});
            skLineSegment(sketch, "E2.71.2.1", {"start": v(-252.25, 213.46) * mm, "end": v(-242.25, 213.46) * mm});
            skLineSegment(sketch, "E2.72.2.1", {"start": v(-238.5, 153.49) * mm, "end": v(-228.5, 153.49) * mm});
            skLineSegment(sketch, "E2.73.2.1", {"start": v(-239.9, 201.47) * mm, "end": v(-229.9, 201.47) * mm});
            skLineSegment(sketch, "E2.74.2.1", {"start": v(-227.2, 177.48) * mm, "end": v(-217.2, 177.48) * mm});
            skLineSegment(sketch, "E2.78.2.1", {"start": v(-310.5, 143.49) * mm, "end": v(-300.5, 143.49) * mm});
            skLineSegment(sketch, "E2.80.2.1", {"start": v(-297.8, 119.5) * mm, "end": v(-287.8, 119.5) * mm});
            skLineSegment(sketch, "E2.81.2.1", {"start": v(-299.2, 167.48) * mm, "end": v(-289.2, 167.48) * mm});
            skLineSegment(sketch, "E2.83.2.1", {"start": v(-286.5, 143.49) * mm, "end": v(-276.5, 143.49) * mm});
            skLineSegment(sketch, "E2.84.2.1", {"start": v(-287.9, 191.47) * mm, "end": v(-277.9, 191.47) * mm});
            skLineSegment(sketch, "E2.85.2.1", {"start": v(-273.8, 119.5) * mm, "end": v(-263.8, 119.5) * mm});
            skLineSegment(sketch, "E2.86.2.1", {"start": v(-275.2, 167.48) * mm, "end": v(-265.2, 167.48) * mm});
            skLineSegment(sketch, "E2.87.2.1", {"start": v(-276.6, 215.46) * mm, "end": v(-266.6, 215.46) * mm});
            skLineSegment(sketch, "E2.88.2.1", {"start": v(-262.5, 143.49) * mm, "end": v(-252.5, 143.49) * mm});
            skLineSegment(sketch, "E2.89.2.1", {"start": v(-263.9, 191.47) * mm, "end": v(-253.9, 191.47) * mm});
            skLineSegment(sketch, "E2.90.2.1", {"start": v(-249.8, 119.5) * mm, "end": v(-239.8, 119.5) * mm});
            skLineSegment(sketch, "E2.91.2.1", {"start": v(-252.6, 215.46) * mm, "end": v(-242.6, 215.46) * mm});
            skLineSegment(sketch, "E2.92.2.1", {"start": v(-238.85, 155.48) * mm, "end": v(-228.85, 155.48) * mm});
            skLineSegment(sketch, "E2.93.2.1", {"start": v(-240.25, 203.46) * mm, "end": v(-230.25, 203.46) * mm});
            skLineSegment(sketch, "E2.94.2.1", {"start": v(-227.55, 179.47) * mm, "end": v(-217.55, 179.47) * mm});
            skLineSegment(sketch, "E2.98.2.1", {"start": v(-300.5, 143.49) * mm, "end": v(-300.5, 153.49) * mm});
            skLineSegment(sketch, "E2.100.2.1", {"start": v(-287.8, 119.5) * mm, "end": v(-287.8, 129.5) * mm});
            skLineSegment(sketch, "E2.101.2.1", {"start": v(-289.2, 167.48) * mm, "end": v(-289.2, 177.48) * mm});
            skLineSegment(sketch, "E2.103.2.1", {"start": v(-276.5, 143.49) * mm, "end": v(-276.5, 153.49) * mm});
            skLineSegment(sketch, "E2.104.2.1", {"start": v(-277.9, 191.47) * mm, "end": v(-277.9, 201.47) * mm});
            skLineSegment(sketch, "E2.105.2.1", {"start": v(-263.8, 119.5) * mm, "end": v(-263.8, 129.5) * mm});
            skLineSegment(sketch, "E2.106.2.1", {"start": v(-265.2, 167.48) * mm, "end": v(-265.2, 177.48) * mm});
            skLineSegment(sketch, "E2.107.2.1", {"start": v(-266.6, 215.46) * mm, "end": v(-266.6, 225.46) * mm});
            skLineSegment(sketch, "E2.108.2.1", {"start": v(-252.5, 143.49) * mm, "end": v(-252.5, 153.49) * mm});
            skLineSegment(sketch, "E2.109.2.1", {"start": v(-253.9, 191.47) * mm, "end": v(-253.9, 201.47) * mm});
            skLineSegment(sketch, "E2.110.2.1", {"start": v(-239.8, 119.5) * mm, "end": v(-239.8, 129.5) * mm});
            skLineSegment(sketch, "E2.111.2.1", {"start": v(-241.2, 167.48) * mm, "end": v(-241.2, 177.48) * mm});
            skLineSegment(sketch, "E2.112.2.1", {"start": v(-242.6, 215.46) * mm, "end": v(-242.6, 225.46) * mm});
            skLineSegment(sketch, "E2.113.2.1", {"start": v(-228.85, 155.48) * mm, "end": v(-228.85, 165.48) * mm});
            skLineSegment(sketch, "E2.114.2.1", {"start": v(-230.25, 203.46) * mm, "end": v(-230.25, 213.46) * mm});
            skLineSegment(sketch, "E2.115.2.1", {"start": v(-217.55, 179.47) * mm, "end": v(-217.55, 189.47) * mm});
            skLineSegment(sketch, "E2.119.2.1", {"start": v(-310.5, 153.49) * mm, "end": v(-300.5, 153.49) * mm});
            skLineSegment(sketch, "E2.121.2.1", {"start": v(-297.8, 129.5) * mm, "end": v(-287.8, 129.5) * mm});
            skLineSegment(sketch, "E2.122.2.1", {"start": v(-299.2, 177.48) * mm, "end": v(-289.2, 177.48) * mm});
            skLineSegment(sketch, "E2.124.2.1", {"start": v(-286.5, 153.49) * mm, "end": v(-276.5, 153.49) * mm});
            skLineSegment(sketch, "E2.125.2.1", {"start": v(-287.9, 201.47) * mm, "end": v(-277.9, 201.47) * mm});
            skLineSegment(sketch, "E2.126.2.1", {"start": v(-273.8, 129.5) * mm, "end": v(-263.8, 129.5) * mm});
            skLineSegment(sketch, "E2.127.2.1", {"start": v(-275.2, 177.48) * mm, "end": v(-265.2, 177.48) * mm});
            skLineSegment(sketch, "E2.128.2.1", {"start": v(-276.6, 225.46) * mm, "end": v(-266.6, 225.46) * mm});
            skLineSegment(sketch, "E2.129.2.1", {"start": v(-262.5, 153.49) * mm, "end": v(-252.5, 153.49) * mm});
            skLineSegment(sketch, "E2.130.2.1", {"start": v(-263.9, 201.47) * mm, "end": v(-253.9, 201.47) * mm});
            skLineSegment(sketch, "E2.131.2.1", {"start": v(-249.8, 129.5) * mm, "end": v(-239.8, 129.5) * mm});
            skLineSegment(sketch, "E2.132.2.1", {"start": v(-251.2, 177.48) * mm, "end": v(-241.2, 177.48) * mm});
            skLineSegment(sketch, "E2.133.2.1", {"start": v(-252.6, 225.46) * mm, "end": v(-242.6, 225.46) * mm});
            skLineSegment(sketch, "E2.134.2.1", {"start": v(-238.85, 165.48) * mm, "end": v(-228.85, 165.48) * mm});
            skLineSegment(sketch, "E2.135.2.1", {"start": v(-240.25, 213.46) * mm, "end": v(-230.25, 213.46) * mm});
            skLineSegment(sketch, "E2.136.2.1", {"start": v(-227.55, 189.47) * mm, "end": v(-217.55, 189.47) * mm});
            skLineSegment(sketch, "E2.140.2.1", {"start": v(-310.5, 143.49) * mm, "end": v(-310.5, 153.49) * mm});
            skLineSegment(sketch, "E2.142.2.1", {"start": v(-297.8, 119.5) * mm, "end": v(-297.8, 129.5) * mm});
            skLineSegment(sketch, "E2.143.2.1", {"start": v(-299.2, 167.48) * mm, "end": v(-299.2, 177.48) * mm});
            skLineSegment(sketch, "E2.145.2.1", {"start": v(-286.5, 143.49) * mm, "end": v(-286.5, 153.49) * mm});
            skLineSegment(sketch, "E2.146.2.1", {"start": v(-287.9, 191.47) * mm, "end": v(-287.9, 201.47) * mm});
            skLineSegment(sketch, "E2.147.2.1", {"start": v(-273.8, 119.5) * mm, "end": v(-273.8, 129.5) * mm});
            skLineSegment(sketch, "E2.148.2.1", {"start": v(-275.2, 167.48) * mm, "end": v(-275.2, 177.48) * mm});
            skLineSegment(sketch, "E2.149.2.1", {"start": v(-276.6, 215.46) * mm, "end": v(-276.6, 225.46) * mm});
            skLineSegment(sketch, "E2.150.2.1", {"start": v(-262.5, 143.49) * mm, "end": v(-262.5, 153.49) * mm});
            skLineSegment(sketch, "E2.151.2.1", {"start": v(-263.9, 191.47) * mm, "end": v(-263.9, 201.47) * mm});
            skLineSegment(sketch, "E2.152.2.1", {"start": v(-249.8, 119.5) * mm, "end": v(-249.8, 129.5) * mm});
            skLineSegment(sketch, "E2.153.2.1", {"start": v(-251.2, 167.48) * mm, "end": v(-251.2, 177.48) * mm});
            skLineSegment(sketch, "E2.154.2.1", {"start": v(-252.6, 215.46) * mm, "end": v(-252.6, 225.46) * mm});
            skLineSegment(sketch, "E2.155.2.1", {"start": v(-238.85, 155.48) * mm, "end": v(-238.85, 165.48) * mm});
            skLineSegment(sketch, "E2.156.2.1", {"start": v(-240.25, 203.46) * mm, "end": v(-240.25, 213.46) * mm});
            skLineSegment(sketch, "E2.157.2.1", {"start": v(-227.55, 179.47) * mm, "end": v(-227.55, 189.47) * mm});
            skLineSegment(sketch, "E2.161.2.1", {"start": v(-310.85, 155.48) * mm, "end": v(-300.85, 155.48) * mm});
            skLineSegment(sketch, "E2.163.2.1", {"start": v(-298.15, 131.5) * mm, "end": v(-288.15, 131.5) * mm});
            skLineSegment(sketch, "E2.164.2.1", {"start": v(-299.55, 179.47) * mm, "end": v(-289.55, 179.47) * mm});
            skLineSegment(sketch, "E2.166.2.1", {"start": v(-286.85, 155.48) * mm, "end": v(-276.85, 155.48) * mm});
            skLineSegment(sketch, "E2.167.2.1", {"start": v(-288.25, 203.46) * mm, "end": v(-278.25, 203.46) * mm});
            skLineSegment(sketch, "E2.168.2.1", {"start": v(-274.15, 131.5) * mm, "end": v(-264.15, 131.5) * mm});
            skLineSegment(sketch, "E2.169.2.1", {"start": v(-275.55, 179.47) * mm, "end": v(-265.55, 179.47) * mm});
            skLineSegment(sketch, "E2.170.2.1", {"start": v(-276.96, 227.45) * mm, "end": v(-266.96, 227.45) * mm});
            skLineSegment(sketch, "E2.171.2.1", {"start": v(-262.85, 155.48) * mm, "end": v(-252.85, 155.48) * mm});
            skLineSegment(sketch, "E2.172.2.1", {"start": v(-264.25, 203.46) * mm, "end": v(-254.25, 203.46) * mm});
            skLineSegment(sketch, "E2.173.2.1", {"start": v(-250.15, 131.5) * mm, "end": v(-240.15, 131.5) * mm});
            skLineSegment(sketch, "E2.174.2.1", {"start": v(-251.55, 179.47) * mm, "end": v(-241.55, 179.47) * mm});
            skLineSegment(sketch, "E2.175.2.1", {"start": v(-252.96, 227.45) * mm, "end": v(-242.96, 227.45) * mm});
            skLineSegment(sketch, "E2.176.2.1", {"start": v(-239.2, 167.48) * mm, "end": v(-229.2, 167.48) * mm});
            skLineSegment(sketch, "E2.177.2.1", {"start": v(-240.6, 215.46) * mm, "end": v(-230.6, 215.46) * mm});
            skLineSegment(sketch, "E2.178.2.1", {"start": v(-227.9, 191.47) * mm, "end": v(-217.9, 191.47) * mm});
            skLineSegment(sketch, "E2.182.2.1", {"start": v(-300.85, 155.48) * mm, "end": v(-300.85, 165.48) * mm});
            skLineSegment(sketch, "E2.184.2.1", {"start": v(-288.15, 131.5) * mm, "end": v(-288.15, 141.5) * mm});
            skLineSegment(sketch, "E2.185.2.1", {"start": v(-289.55, 179.47) * mm, "end": v(-289.55, 189.47) * mm});
            skLineSegment(sketch, "E2.187.2.1", {"start": v(-276.85, 155.48) * mm, "end": v(-276.85, 165.48) * mm});
            skLineSegment(sketch, "E2.188.2.1", {"start": v(-278.25, 203.46) * mm, "end": v(-278.25, 213.46) * mm});
            skLineSegment(sketch, "E2.189.2.1", {"start": v(-264.15, 131.5) * mm, "end": v(-264.15, 141.5) * mm});
            skLineSegment(sketch, "E2.190.2.1", {"start": v(-265.55, 179.47) * mm, "end": v(-265.55, 189.47) * mm});
            skLineSegment(sketch, "E2.191.2.1", {"start": v(-266.96, 227.45) * mm, "end": v(-266.96, 237.45) * mm});
            skLineSegment(sketch, "E2.192.2.1", {"start": v(-252.85, 155.48) * mm, "end": v(-252.85, 165.48) * mm});
            skLineSegment(sketch, "E2.193.2.1", {"start": v(-254.25, 203.46) * mm, "end": v(-254.25, 213.46) * mm});
            skLineSegment(sketch, "E2.194.2.1", {"start": v(-240.15, 131.5) * mm, "end": v(-240.15, 141.5) * mm});
            skLineSegment(sketch, "E2.195.2.1", {"start": v(-241.55, 179.47) * mm, "end": v(-241.55, 189.47) * mm});
            skLineSegment(sketch, "E2.196.2.1", {"start": v(-242.96, 227.45) * mm, "end": v(-242.96, 237.45) * mm});
            skLineSegment(sketch, "E2.197.2.1", {"start": v(-229.2, 167.48) * mm, "end": v(-229.2, 177.48) * mm});
            skLineSegment(sketch, "E2.198.2.1", {"start": v(-230.6, 215.46) * mm, "end": v(-230.6, 225.46) * mm});
            skLineSegment(sketch, "E2.199.2.1", {"start": v(-217.9, 191.47) * mm, "end": v(-217.9, 201.47) * mm});
            skLineSegment(sketch, "E2.205.2.1", {"start": v(-298.15, 141.5) * mm, "end": v(-288.15, 141.5) * mm});
            skLineSegment(sketch, "E2.208.2.1", {"start": v(-286.85, 165.48) * mm, "end": v(-276.85, 165.48) * mm});
            skLineSegment(sketch, "E2.210.2.1", {"start": v(-274.15, 141.5) * mm, "end": v(-264.15, 141.5) * mm});
            skLineSegment(sketch, "E2.211.2.1", {"start": v(-275.55, 189.47) * mm, "end": v(-265.55, 189.47) * mm});
            skLineSegment(sketch, "E2.213.2.1", {"start": v(-262.85, 165.48) * mm, "end": v(-252.85, 165.48) * mm});
            skLineSegment(sketch, "E2.214.2.1", {"start": v(-264.25, 213.46) * mm, "end": v(-254.25, 213.46) * mm});
            skLineSegment(sketch, "E2.215.2.1", {"start": v(-250.15, 141.5) * mm, "end": v(-240.15, 141.5) * mm});
            skLineSegment(sketch, "E2.216.2.1", {"start": v(-251.55, 189.47) * mm, "end": v(-241.55, 189.47) * mm});
            skLineSegment(sketch, "E2.217.2.1", {"start": v(-252.96, 237.45) * mm, "end": v(-242.96, 237.45) * mm});
            skLineSegment(sketch, "E2.218.2.1", {"start": v(-239.2, 177.48) * mm, "end": v(-229.2, 177.48) * mm});
            skLineSegment(sketch, "E2.219.2.1", {"start": v(-240.6, 225.46) * mm, "end": v(-230.6, 225.46) * mm});
            skLineSegment(sketch, "E2.220.2.1", {"start": v(-227.9, 201.47) * mm, "end": v(-217.9, 201.47) * mm});
            skLineSegment(sketch, "E2.226.2.1", {"start": v(-298.15, 131.5) * mm, "end": v(-298.15, 141.5) * mm});
            skLineSegment(sketch, "E2.229.2.1", {"start": v(-286.85, 155.48) * mm, "end": v(-286.85, 165.48) * mm});
            skLineSegment(sketch, "E2.231.2.1", {"start": v(-274.15, 131.5) * mm, "end": v(-274.15, 141.5) * mm});
            skLineSegment(sketch, "E2.232.2.1", {"start": v(-275.55, 179.47) * mm, "end": v(-275.55, 189.47) * mm});
            skLineSegment(sketch, "E2.234.2.1", {"start": v(-262.85, 155.48) * mm, "end": v(-262.85, 165.48) * mm});
            skLineSegment(sketch, "E2.235.2.1", {"start": v(-264.25, 203.46) * mm, "end": v(-264.25, 213.46) * mm});
            skLineSegment(sketch, "E2.236.2.1", {"start": v(-250.15, 131.5) * mm, "end": v(-250.15, 141.5) * mm});
            skLineSegment(sketch, "E2.237.2.1", {"start": v(-251.55, 179.47) * mm, "end": v(-251.55, 189.47) * mm});
            skLineSegment(sketch, "E2.238.2.1", {"start": v(-252.96, 227.45) * mm, "end": v(-252.96, 237.45) * mm});
            skLineSegment(sketch, "E2.239.2.1", {"start": v(-239.2, 167.48) * mm, "end": v(-239.2, 177.48) * mm});
            skLineSegment(sketch, "E2.240.2.1", {"start": v(-240.6, 215.46) * mm, "end": v(-240.6, 225.46) * mm});
            skLineSegment(sketch, "E2.241.2.1", {"start": v(-227.9, 191.47) * mm, "end": v(-227.9, 201.47) * mm});
            skLineSegment(sketch, "E2.244.2.1", {"start": v(-309.8, 119.5) * mm, "end": v(-299.8, 119.5) * mm});
            skLineSegment(sketch, "E2.247.2.1", {"start": v(-298.5, 143.49) * mm, "end": v(-288.5, 143.49) * mm});
            skLineSegment(sketch, "E2.249.2.1", {"start": v(-285.8, 119.5) * mm, "end": v(-275.8, 119.5) * mm});
            skLineSegment(sketch, "E2.250.2.1", {"start": v(-287.2, 167.48) * mm, "end": v(-277.2, 167.48) * mm});
            skLineSegment(sketch, "E2.252.2.1", {"start": v(-274.5, 143.49) * mm, "end": v(-264.5, 143.49) * mm});
            skLineSegment(sketch, "E2.253.2.1", {"start": v(-275.9, 191.47) * mm, "end": v(-265.9, 191.47) * mm});
            skLineSegment(sketch, "E2.254.2.1", {"start": v(-261.8, 119.5) * mm, "end": v(-251.8, 119.5) * mm});
            skLineSegment(sketch, "E2.255.2.1", {"start": v(-263.2, 167.48) * mm, "end": v(-253.2, 167.48) * mm});
            skLineSegment(sketch, "E2.256.2.1", {"start": v(-264.6, 215.46) * mm, "end": v(-254.6, 215.46) * mm});
            skLineSegment(sketch, "E2.257.2.1", {"start": v(-250.5, 143.49) * mm, "end": v(-240.5, 143.49) * mm});
            skLineSegment(sketch, "E2.258.2.1", {"start": v(-251.9, 191.47) * mm, "end": v(-241.9, 191.47) * mm});
            skLineSegment(sketch, "E2.259.2.1", {"start": v(-238.15, 131.5) * mm, "end": v(-228.15, 131.5) * mm});
            skLineSegment(sketch, "E2.260.2.1", {"start": v(-239.55, 179.47) * mm, "end": v(-229.55, 179.47) * mm});
            skLineSegment(sketch, "E2.261.2.1", {"start": v(-226.85, 155.48) * mm, "end": v(-216.85, 155.48) * mm});
            skLineSegment(sketch, "E2.262.2.1", {"start": v(-228.25, 203.46) * mm, "end": v(-218.25, 203.46) * mm});
            skLineSegment(sketch, "E2.263.2.1", {"start": v(-312.15, 131.5) * mm, "end": v(-312.15, 141.5) * mm});
            skLineSegment(sketch, "E2.265.2.1", {"start": v(-299.8, 119.5) * mm, "end": v(-299.8, 129.5) * mm});
            skLineSegment(sketch, "E2.268.2.1", {"start": v(-288.5, 143.49) * mm, "end": v(-288.5, 153.49) * mm});
            skLineSegment(sketch, "E2.269.2.1", {"start": v(-289.9, 191.47) * mm, "end": v(-289.9, 201.47) * mm});
            skLineSegment(sketch, "E2.270.2.1", {"start": v(-275.8, 119.5) * mm, "end": v(-275.8, 129.5) * mm});
            skLineSegment(sketch, "E2.271.2.1", {"start": v(-277.2, 167.48) * mm, "end": v(-277.2, 177.48) * mm});
            skLineSegment(sketch, "E2.272.2.1", {"start": v(-278.6, 215.46) * mm, "end": v(-278.6, 225.46) * mm});
            skLineSegment(sketch, "E2.273.2.1", {"start": v(-264.5, 143.49) * mm, "end": v(-264.5, 153.49) * mm});
            skLineSegment(sketch, "E2.274.2.1", {"start": v(-265.9, 191.47) * mm, "end": v(-265.9, 201.47) * mm});
            skLineSegment(sketch, "E2.275.2.1", {"start": v(-251.8, 119.5) * mm, "end": v(-251.8, 129.5) * mm});
            skLineSegment(sketch, "E2.276.2.1", {"start": v(-253.2, 167.48) * mm, "end": v(-253.2, 177.48) * mm});
            skLineSegment(sketch, "E2.277.2.1", {"start": v(-254.6, 215.46) * mm, "end": v(-254.6, 225.46) * mm});
            skLineSegment(sketch, "E2.278.2.1", {"start": v(-240.5, 143.49) * mm, "end": v(-240.5, 153.49) * mm});
            skLineSegment(sketch, "E2.279.2.1", {"start": v(-241.9, 191.47) * mm, "end": v(-241.9, 201.47) * mm});
            skLineSegment(sketch, "E2.280.2.1", {"start": v(-228.15, 131.5) * mm, "end": v(-228.15, 141.5) * mm});
            skLineSegment(sketch, "E2.281.2.1", {"start": v(-229.55, 179.47) * mm, "end": v(-229.55, 189.47) * mm});
            skLineSegment(sketch, "E2.282.2.1", {"start": v(-216.85, 155.48) * mm, "end": v(-216.85, 165.48) * mm});
            skLineSegment(sketch, "E2.283.2.1", {"start": v(-218.25, 203.46) * mm, "end": v(-218.25, 213.46) * mm});
            skLineSegment(sketch, "E2.286.2.1", {"start": v(-309.8, 129.5) * mm, "end": v(-299.8, 129.5) * mm});
            skLineSegment(sketch, "E2.289.2.1", {"start": v(-298.5, 153.49) * mm, "end": v(-288.5, 153.49) * mm});
            skLineSegment(sketch, "E2.291.2.1", {"start": v(-285.8, 129.5) * mm, "end": v(-275.8, 129.5) * mm});
            skLineSegment(sketch, "E2.292.2.1", {"start": v(-287.2, 177.48) * mm, "end": v(-277.2, 177.48) * mm});
            skLineSegment(sketch, "E2.294.2.1", {"start": v(-274.5, 153.49) * mm, "end": v(-264.5, 153.49) * mm});
            skLineSegment(sketch, "E2.295.2.1", {"start": v(-275.9, 201.47) * mm, "end": v(-265.9, 201.47) * mm});
            skLineSegment(sketch, "E2.296.2.1", {"start": v(-261.8, 129.5) * mm, "end": v(-251.8, 129.5) * mm});
            skLineSegment(sketch, "E2.297.2.1", {"start": v(-263.2, 177.48) * mm, "end": v(-253.2, 177.48) * mm});
            skLineSegment(sketch, "E2.298.2.1", {"start": v(-264.6, 225.46) * mm, "end": v(-254.6, 225.46) * mm});
            skLineSegment(sketch, "E2.299.2.1", {"start": v(-250.5, 153.49) * mm, "end": v(-240.5, 153.49) * mm});
            skLineSegment(sketch, "E2.300.2.1", {"start": v(-251.9, 201.47) * mm, "end": v(-241.9, 201.47) * mm});
            skLineSegment(sketch, "E2.301.2.1", {"start": v(-238.15, 141.5) * mm, "end": v(-228.15, 141.5) * mm});
            skLineSegment(sketch, "E2.302.2.1", {"start": v(-239.55, 189.47) * mm, "end": v(-229.55, 189.47) * mm});
            skLineSegment(sketch, "E2.303.2.1", {"start": v(-226.85, 165.48) * mm, "end": v(-216.85, 165.48) * mm});
            skLineSegment(sketch, "E2.304.2.1", {"start": v(-228.25, 213.46) * mm, "end": v(-218.25, 213.46) * mm});
            skLineSegment(sketch, "E2.307.2.1", {"start": v(-309.8, 119.5) * mm, "end": v(-309.8, 129.5) * mm});
            skLineSegment(sketch, "E2.310.2.1", {"start": v(-298.5, 143.49) * mm, "end": v(-298.5, 153.49) * mm});
            skLineSegment(sketch, "E2.312.2.1", {"start": v(-285.8, 119.5) * mm, "end": v(-285.8, 129.5) * mm});
            skLineSegment(sketch, "E2.313.2.1", {"start": v(-287.2, 167.48) * mm, "end": v(-287.2, 177.48) * mm});
            skLineSegment(sketch, "E2.315.2.1", {"start": v(-274.5, 143.49) * mm, "end": v(-274.5, 153.49) * mm});
            skLineSegment(sketch, "E2.316.2.1", {"start": v(-275.9, 191.47) * mm, "end": v(-275.9, 201.47) * mm});
            skLineSegment(sketch, "E2.317.2.1", {"start": v(-261.8, 119.5) * mm, "end": v(-261.8, 129.5) * mm});
            skLineSegment(sketch, "E2.318.2.1", {"start": v(-263.2, 167.48) * mm, "end": v(-263.2, 177.48) * mm});
            skLineSegment(sketch, "E2.319.2.1", {"start": v(-264.6, 215.46) * mm, "end": v(-264.6, 225.46) * mm});
            skLineSegment(sketch, "E2.320.2.1", {"start": v(-250.5, 143.49) * mm, "end": v(-250.5, 153.49) * mm});
            skLineSegment(sketch, "E2.321.2.1", {"start": v(-251.9, 191.47) * mm, "end": v(-251.9, 201.47) * mm});
            skLineSegment(sketch, "E2.322.2.1", {"start": v(-238.15, 131.5) * mm, "end": v(-238.15, 141.5) * mm});
            skLineSegment(sketch, "E2.323.2.1", {"start": v(-239.55, 179.47) * mm, "end": v(-239.55, 189.47) * mm});
            skLineSegment(sketch, "E2.324.2.1", {"start": v(-226.85, 155.48) * mm, "end": v(-226.85, 165.48) * mm});
            skLineSegment(sketch, "E2.325.2.1", {"start": v(-228.25, 203.46) * mm, "end": v(-228.25, 213.46) * mm});
            skLineSegment(sketch, "E2.328.2.1", {"start": v(-310.15, 131.5) * mm, "end": v(-300.15, 131.5) * mm});
            skLineSegment(sketch, "E2.331.2.1", {"start": v(-298.85, 155.48) * mm, "end": v(-288.85, 155.48) * mm});
            skLineSegment(sketch, "E2.333.2.1", {"start": v(-286.15, 131.5) * mm, "end": v(-276.15, 131.5) * mm});
            skLineSegment(sketch, "E2.334.2.1", {"start": v(-287.55, 179.47) * mm, "end": v(-277.55, 179.47) * mm});
            skLineSegment(sketch, "E2.336.2.1", {"start": v(-274.85, 155.48) * mm, "end": v(-264.85, 155.48) * mm});
            skLineSegment(sketch, "E2.337.2.1", {"start": v(-276.25, 203.46) * mm, "end": v(-266.25, 203.46) * mm});
            skLineSegment(sketch, "E2.338.2.1", {"start": v(-262.15, 131.5) * mm, "end": v(-252.15, 131.5) * mm});
            skLineSegment(sketch, "E2.339.2.1", {"start": v(-263.55, 179.47) * mm, "end": v(-253.55, 179.47) * mm});
            skLineSegment(sketch, "E2.340.2.1", {"start": v(-264.96, 227.45) * mm, "end": v(-254.96, 227.45) * mm});
            skLineSegment(sketch, "E2.341.2.1", {"start": v(-250.85, 155.48) * mm, "end": v(-240.85, 155.48) * mm});
            skLineSegment(sketch, "E2.342.2.1", {"start": v(-252.25, 203.46) * mm, "end": v(-242.25, 203.46) * mm});
            skLineSegment(sketch, "E2.343.2.1", {"start": v(-238.5, 143.49) * mm, "end": v(-228.5, 143.49) * mm});
            skLineSegment(sketch, "E2.344.2.1", {"start": v(-239.9, 191.47) * mm, "end": v(-229.9, 191.47) * mm});
            skLineSegment(sketch, "E2.345.2.1", {"start": v(-227.2, 167.48) * mm, "end": v(-217.2, 167.48) * mm});
            skLineSegment(sketch, "E2.346.2.1", {"start": v(-250.85, 165.48) * mm, "end": v(-240.85, 165.48) * mm});
            skLineSegment(sketch, "E2.347.2.1", {"start": v(-251.2, 167.48) * mm, "end": v(-241.2, 167.48) * mm});
            skLineSegment(sketch, "E2.direction1", {"start": v(-100.5, 19.49) * mm, "end": v(-217.5, 19.49) * mm, "construction": true});
            skLineSegment(sketch, "E2.direction2", {"start": v(-100.5, 19.49) * mm, "end": v(-100.5, 143.49) * mm, "construction": true});
            skSolve(sketch);
        }
        {
            var Q0;
            Q0 = qSketchRegion(id + "F2", true);
            extrude(context, id + "F3", {"entities" : qUnion([Q0]), "operationType" : NewBodyOperationType.REMOVE, "oppositeDirection" : true, "depth" : 182.8 * mm});
        }
    });
